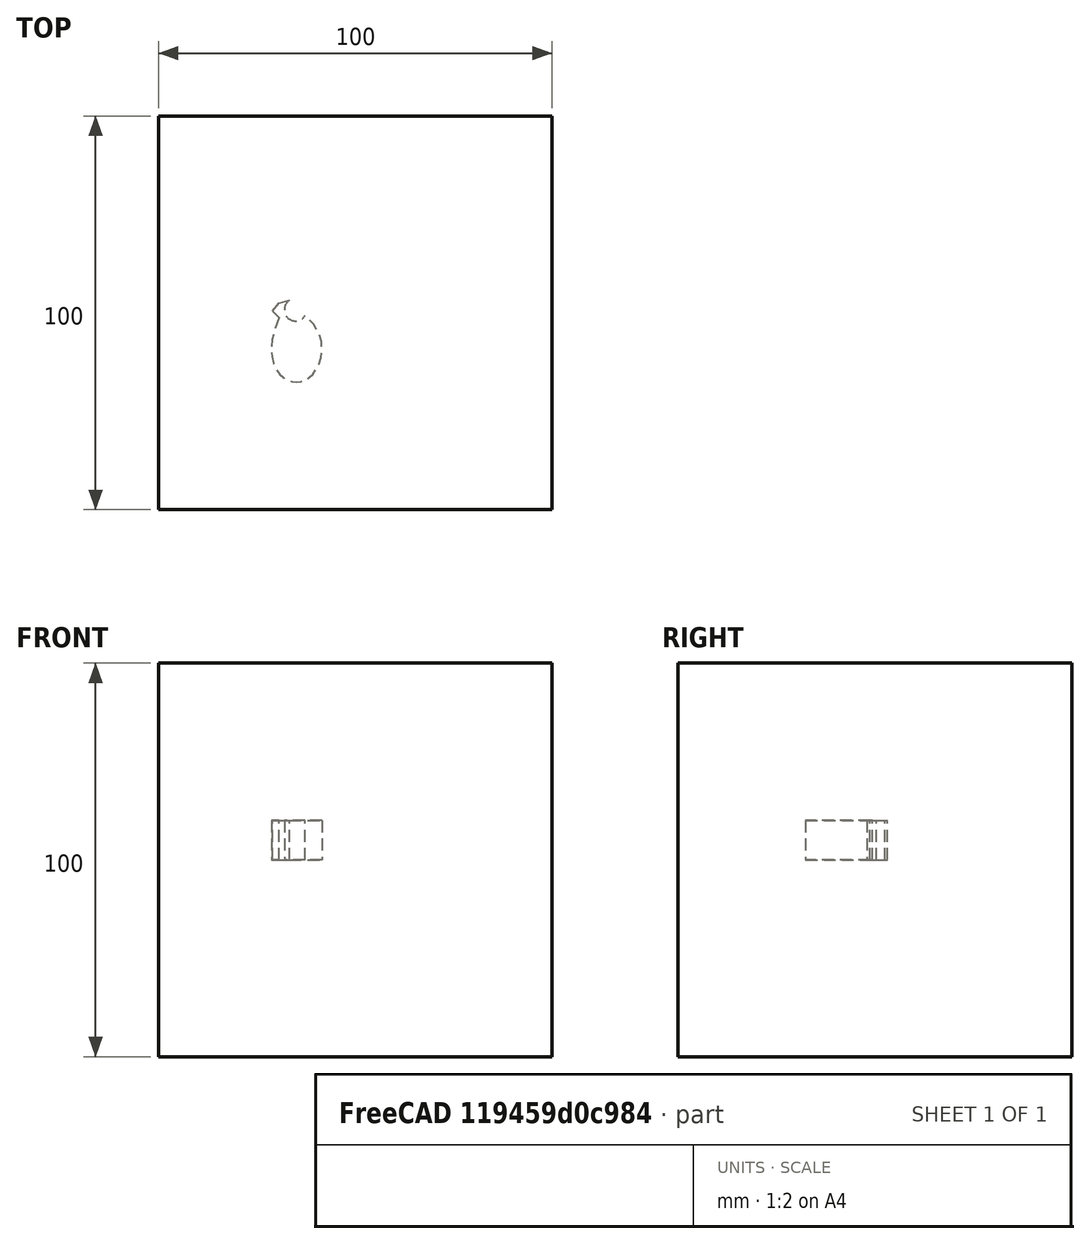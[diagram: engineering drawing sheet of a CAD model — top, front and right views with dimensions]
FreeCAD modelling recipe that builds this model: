
FCSTD DOCUMENT  (FreeCAD 1.0R39109 (Git))
Label: mirrorTest-1c
License: All rights reserved
LicenseURL: http://en.wikipedia.org/wiki/All_rights_reserved
objects: App::DocumentObjectGroupPython×1248, App::Part×2, Part::FeaturePython×1, Sketcher::SketchObject×1, Part::Extrusion×1, Part::Mirroring×1
note: 5 computed .brp shape members not serialized (recipe doc carries the construction recipe); baked Part::Feature solids carry a one-line shape summary decoded from their .brp

FEATURE [App::DocumentObjectGroupPython] HALFPI  # scripted group (container) (typed FeaturePython)
  name = HALFPI
  value = pi/2.
FEATURE [App::DocumentObjectGroupPython] PI  # scripted group (container) (typed FeaturePython)
  name = PI
  value = 1.*pi
FEATURE [App::DocumentObjectGroupPython] TWOPI  # scripted group (container) (typed FeaturePython)
  name = TWOPI
  value = 2.*pi
FEATURE [App::DocumentObjectGroupPython] Constants  # scripted group (container) (typed FeaturePython)
  Group = -> [HALFPI,PI,TWOPI]
FEATURE [App::DocumentObjectGroupPython] Variables  # scripted group (container) (typed FeaturePython)
FEATURE [App::DocumentObjectGroupPython] Quantities  # scripted group (container) (typed FeaturePython)
FEATURE [App::DocumentObjectGroupPython] Isotopes  # scripted group (container) (typed FeaturePython)
FEATURE [App::DocumentObjectGroupPython] Elements  # scripted group (container) (typed FeaturePython)
FEATURE [App::DocumentObjectGroupPython] G4Isotopes  # scripted group (container) (typed FeaturePython)
FEATURE [App::DocumentObjectGroupPython] H_element  # scripted group (container) (typed FeaturePython)
  Z = 1
  atom_value = 1.008
  formula = H
  name = H_element
FEATURE [App::DocumentObjectGroupPython] He_element  # scripted group (container) (typed FeaturePython)
  Z = 2
  atom_value = 4.0026
  formula = He
  name = He_element
FEATURE [App::DocumentObjectGroupPython] Li_element  # scripted group (container) (typed FeaturePython)
  Z = 3
  atom_value = 6.94
  formula = Li
  name = Li_element
FEATURE [App::DocumentObjectGroupPython] Be_element  # scripted group (container) (typed FeaturePython)
  Z = 4
  atom_value = 9.01218
  formula = Be
  name = Be_element
FEATURE [App::DocumentObjectGroupPython] B_element  # scripted group (container) (typed FeaturePython)
  Z = 5
  atom_value = 10.81
  formula = B
  name = B_element
FEATURE [App::DocumentObjectGroupPython] C_element  # scripted group (container) (typed FeaturePython)
  Z = 6
  atom_value = 12.011
  formula = C
  name = C_element
FEATURE [App::DocumentObjectGroupPython] N_element  # scripted group (container) (typed FeaturePython)
  Z = 7
  atom_value = 14.007
  formula = N
  name = N_element
FEATURE [App::DocumentObjectGroupPython] O_element  # scripted group (container) (typed FeaturePython)
  Z = 8
  atom_value = 15.999
  formula = O
  name = O_element
FEATURE [App::DocumentObjectGroupPython] F_element  # scripted group (container) (typed FeaturePython)
  Z = 9
  atom_value = 18.9984
  formula = F
  name = F_element
FEATURE [App::DocumentObjectGroupPython] Ne_element  # scripted group (container) (typed FeaturePython)
  Z = 10
  atom_value = 20.1797
  formula = Ne
  name = Ne_element
FEATURE [App::DocumentObjectGroupPython] Na_element  # scripted group (container) (typed FeaturePython)
  Z = 11
  atom_value = 22.9898
  formula = Na
  name = Na_element
FEATURE [App::DocumentObjectGroupPython] Mg_element  # scripted group (container) (typed FeaturePython)
  Z = 12
  atom_value = 24.305
  formula = Mg
  name = Mg_element
FEATURE [App::DocumentObjectGroupPython] Al_element  # scripted group (container) (typed FeaturePython)
  Z = 13
  atom_value = 26.9815
  formula = Al
  name = Al_element
FEATURE [App::DocumentObjectGroupPython] Si_element  # scripted group (container) (typed FeaturePython)
  Z = 14
  atom_value = 28.085
  formula = Si
  name = Si_element
FEATURE [App::DocumentObjectGroupPython] P_element  # scripted group (container) (typed FeaturePython)
  Z = 15
  atom_value = 30.9738
  formula = P
  name = P_element
FEATURE [App::DocumentObjectGroupPython] S_element  # scripted group (container) (typed FeaturePython)
  Z = 16
  atom_value = 32.06
  formula = S
  name = S_element
FEATURE [App::DocumentObjectGroupPython] Cl_element  # scripted group (container) (typed FeaturePython)
  Z = 17
  atom_value = 35.45
  formula = Cl
  name = Cl_element
FEATURE [App::DocumentObjectGroupPython] Ar_element  # scripted group (container) (typed FeaturePython)
  Z = 18
  atom_value = 39.95
  formula = Ar
  name = Ar_element
FEATURE [App::DocumentObjectGroupPython] K_element  # scripted group (container) (typed FeaturePython)
  Z = 19
  atom_value = 39.0983
  formula = K
  name = K_element
FEATURE [App::DocumentObjectGroupPython] Ca_element  # scripted group (container) (typed FeaturePython)
  Z = 20
  atom_value = 40.078
  formula = Ca
  name = Ca_element
FEATURE [App::DocumentObjectGroupPython] Sc_element  # scripted group (container) (typed FeaturePython)
  Z = 21
  atom_value = 44.9559
  formula = Sc
  name = Sc_element
FEATURE [App::DocumentObjectGroupPython] Ti_element  # scripted group (container) (typed FeaturePython)
  Z = 22
  atom_value = 47.867
  formula = Ti
  name = Ti_element
FEATURE [App::DocumentObjectGroupPython] V_element  # scripted group (container) (typed FeaturePython)
  Z = 23
  atom_value = 50.9415
  formula = V
  name = V_element
FEATURE [App::DocumentObjectGroupPython] Cr_element  # scripted group (container) (typed FeaturePython)
  Z = 24
  atom_value = 51.9961
  formula = Cr
  name = Cr_element
FEATURE [App::DocumentObjectGroupPython] Mn_element  # scripted group (container) (typed FeaturePython)
  Z = 25
  atom_value = 54.938
  formula = Mn
  name = Mn_element
FEATURE [App::DocumentObjectGroupPython] Fe_element  # scripted group (container) (typed FeaturePython)
  Z = 26
  atom_value = 55.845
  formula = Fe
  name = Fe_element
FEATURE [App::DocumentObjectGroupPython] Co_element  # scripted group (container) (typed FeaturePython)
  Z = 27
  atom_value = 58.9332
  formula = Co
  name = Co_element
FEATURE [App::DocumentObjectGroupPython] Ni_element  # scripted group (container) (typed FeaturePython)
  Z = 28
  atom_value = 58.6934
  formula = Ni
  name = Ni_element
FEATURE [App::DocumentObjectGroupPython] Cu_element  # scripted group (container) (typed FeaturePython)
  Z = 29
  atom_value = 63.546
  formula = Cu
  name = Cu_element
FEATURE [App::DocumentObjectGroupPython] Zn_element  # scripted group (container) (typed FeaturePython)
  Z = 30
  atom_value = 65.38
  formula = Zn
  name = Zn_element
FEATURE [App::DocumentObjectGroupPython] Ga_element  # scripted group (container) (typed FeaturePython)
  Z = 31
  atom_value = 69.723
  formula = Ga
  name = Ga_element
FEATURE [App::DocumentObjectGroupPython] Ge_element  # scripted group (container) (typed FeaturePython)
  Z = 32
  atom_value = 72.63
  formula = Ge
  name = Ge_element
FEATURE [App::DocumentObjectGroupPython] As_element  # scripted group (container) (typed FeaturePython)
  Z = 33
  atom_value = 74.9216
  formula = As
  name = As_element
FEATURE [App::DocumentObjectGroupPython] Se_element  # scripted group (container) (typed FeaturePython)
  Z = 34
  atom_value = 78.971
  formula = Se
  name = Se_element
FEATURE [App::DocumentObjectGroupPython] Br_element  # scripted group (container) (typed FeaturePython)
  Z = 35
  atom_value = 79.904
  formula = Br
  name = Br_element
FEATURE [App::DocumentObjectGroupPython] Kr_element  # scripted group (container) (typed FeaturePython)
  Z = 36
  atom_value = 83.798
  formula = Kr
  name = Kr_element
FEATURE [App::DocumentObjectGroupPython] Rb_element  # scripted group (container) (typed FeaturePython)
  Z = 37
  atom_value = 85.4678
  formula = Rb
  name = Rb_element
FEATURE [App::DocumentObjectGroupPython] Sr_element  # scripted group (container) (typed FeaturePython)
  Z = 38
  atom_value = 87.62
  formula = Sr
  name = Sr_element
FEATURE [App::DocumentObjectGroupPython] Y_element  # scripted group (container) (typed FeaturePython)
  Z = 39
  atom_value = 88.9058
  formula = Y
  name = Y_element
FEATURE [App::DocumentObjectGroupPython] Zr_element  # scripted group (container) (typed FeaturePython)
  Z = 40
  atom_value = 91.224
  formula = Zr
  name = Zr_element
FEATURE [App::DocumentObjectGroupPython] Nb_element  # scripted group (container) (typed FeaturePython)
  Z = 41
  atom_value = 92.9064
  formula = Nb
  name = Nb_element
FEATURE [App::DocumentObjectGroupPython] Mo_element  # scripted group (container) (typed FeaturePython)
  Z = 42
  atom_value = 95.95
  formula = Mo
  name = Mo_element
FEATURE [App::DocumentObjectGroupPython] Tc_element  # scripted group (container) (typed FeaturePython)
  Z = 43
  atom_value = 97
  formula = Tc
  name = Tc_element
FEATURE [App::DocumentObjectGroupPython] Ru_element  # scripted group (container) (typed FeaturePython)
  Z = 44
  atom_value = 101.07
  formula = Ru
  name = Ru_element
FEATURE [App::DocumentObjectGroupPython] Rh_element  # scripted group (container) (typed FeaturePython)
  Z = 45
  atom_value = 102.905
  formula = Rh
  name = Rh_element
FEATURE [App::DocumentObjectGroupPython] Pd_element  # scripted group (container) (typed FeaturePython)
  Z = 46
  atom_value = 106.42
  formula = Pd
  name = Pd_element
FEATURE [App::DocumentObjectGroupPython] Ag_element  # scripted group (container) (typed FeaturePython)
  Z = 47
  atom_value = 107.868
  formula = Ag
  name = Ag_element
FEATURE [App::DocumentObjectGroupPython] Cd_element  # scripted group (container) (typed FeaturePython)
  Z = 48
  atom_value = 112.414
  formula = Cd
  name = Cd_element
FEATURE [App::DocumentObjectGroupPython] In_element  # scripted group (container) (typed FeaturePython)
  Z = 49
  atom_value = 114.818
  formula = In
  name = In_element
FEATURE [App::DocumentObjectGroupPython] Sn_element  # scripted group (container) (typed FeaturePython)
  Z = 50
  atom_value = 118.71
  formula = Sn
  name = Sn_element
FEATURE [App::DocumentObjectGroupPython] Sb_element  # scripted group (container) (typed FeaturePython)
  Z = 51
  atom_value = 121.76
  formula = Sb
  name = Sb_element
FEATURE [App::DocumentObjectGroupPython] Te_element  # scripted group (container) (typed FeaturePython)
  Z = 52
  atom_value = 127.6
  formula = Te
  name = Te_element
FEATURE [App::DocumentObjectGroupPython] I_element  # scripted group (container) (typed FeaturePython)
  Z = 53
  atom_value = 126.904
  formula = I
  name = I_element
FEATURE [App::DocumentObjectGroupPython] Xe_element  # scripted group (container) (typed FeaturePython)
  Z = 54
  atom_value = 131.293
  formula = Xe
  name = Xe_element
FEATURE [App::DocumentObjectGroupPython] Cs_element  # scripted group (container) (typed FeaturePython)
  Z = 55
  atom_value = 132.905
  formula = Cs
  name = Cs_element
FEATURE [App::DocumentObjectGroupPython] Ba_element  # scripted group (container) (typed FeaturePython)
  Z = 56
  atom_value = 137.327
  formula = Ba
  name = Ba_element
FEATURE [App::DocumentObjectGroupPython] La_element  # scripted group (container) (typed FeaturePython)
  Z = 57
  atom_value = 138.905
  formula = La
  name = La_element
FEATURE [App::DocumentObjectGroupPython] Ce_element  # scripted group (container) (typed FeaturePython)
  Z = 58
  atom_value = 140.116
  formula = Ce
  name = Ce_element
FEATURE [App::DocumentObjectGroupPython] Pr_element  # scripted group (container) (typed FeaturePython)
  Z = 59
  atom_value = 140.908
  formula = Pr
  name = Pr_element
FEATURE [App::DocumentObjectGroupPython] Nd_element  # scripted group (container) (typed FeaturePython)
  Z = 60
  atom_value = 144.242
  formula = Nd
  name = Nd_element
FEATURE [App::DocumentObjectGroupPython] Pm_element  # scripted group (container) (typed FeaturePython)
  Z = 61
  atom_value = 145
  formula = Pm
  name = Pm_element
FEATURE [App::DocumentObjectGroupPython] Sm_element  # scripted group (container) (typed FeaturePython)
  Z = 62
  atom_value = 150.36
  formula = Sm
  name = Sm_element
FEATURE [App::DocumentObjectGroupPython] Eu_element  # scripted group (container) (typed FeaturePython)
  Z = 63
  atom_value = 151.964
  formula = Eu
  name = Eu_element
FEATURE [App::DocumentObjectGroupPython] Gd_element  # scripted group (container) (typed FeaturePython)
  Z = 64
  atom_value = 157.25
  formula = Gd
  name = Gd_element
FEATURE [App::DocumentObjectGroupPython] Tb_element  # scripted group (container) (typed FeaturePython)
  Z = 65
  atom_value = 158.925
  formula = Tb
  name = Tb_element
FEATURE [App::DocumentObjectGroupPython] Dy_element  # scripted group (container) (typed FeaturePython)
  Z = 66
  atom_value = 162.5
  formula = Dy
  name = Dy_element
FEATURE [App::DocumentObjectGroupPython] Ho_element  # scripted group (container) (typed FeaturePython)
  Z = 67
  atom_value = 164.93
  formula = Ho
  name = Ho_element
FEATURE [App::DocumentObjectGroupPython] Er_element  # scripted group (container) (typed FeaturePython)
  Z = 68
  atom_value = 167.259
  formula = Er
  name = Er_element
FEATURE [App::DocumentObjectGroupPython] Tm_element  # scripted group (container) (typed FeaturePython)
  Z = 69
  atom_value = 168.934
  formula = Tm
  name = Tm_element
FEATURE [App::DocumentObjectGroupPython] Yb_element  # scripted group (container) (typed FeaturePython)
  Z = 70
  atom_value = 173.045
  formula = Yb
  name = Yb_element
FEATURE [App::DocumentObjectGroupPython] Lu_element  # scripted group (container) (typed FeaturePython)
  Z = 71
  atom_value = 174.967
  formula = Lu
  name = Lu_element
FEATURE [App::DocumentObjectGroupPython] Hf_element  # scripted group (container) (typed FeaturePython)
  Z = 72
  atom_value = 178.49
  formula = Hf
  name = Hf_element
FEATURE [App::DocumentObjectGroupPython] Ta_element  # scripted group (container) (typed FeaturePython)
  Z = 73
  atom_value = 180.948
  formula = Ta
  name = Ta_element
FEATURE [App::DocumentObjectGroupPython] W_element  # scripted group (container) (typed FeaturePython)
  Z = 74
  atom_value = 183.84
  formula = W
  name = W_element
FEATURE [App::DocumentObjectGroupPython] Re_element  # scripted group (container) (typed FeaturePython)
  Z = 75
  atom_value = 186.207
  formula = Re
  name = Re_element
FEATURE [App::DocumentObjectGroupPython] Os_element  # scripted group (container) (typed FeaturePython)
  Z = 76
  atom_value = 190.23
  formula = Os
  name = Os_element
FEATURE [App::DocumentObjectGroupPython] Ir_element  # scripted group (container) (typed FeaturePython)
  Z = 77
  atom_value = 192.217
  formula = Ir
  name = Ir_element
FEATURE [App::DocumentObjectGroupPython] Pt_element  # scripted group (container) (typed FeaturePython)
  Z = 78
  atom_value = 195.084
  formula = Pt
  name = Pt_element
FEATURE [App::DocumentObjectGroupPython] Au_element  # scripted group (container) (typed FeaturePython)
  Z = 79
  atom_value = 196.967
  formula = Au
  name = Au_element
FEATURE [App::DocumentObjectGroupPython] Hg_element  # scripted group (container) (typed FeaturePython)
  Z = 80
  atom_value = 200.592
  formula = Hg
  name = Hg_element
FEATURE [App::DocumentObjectGroupPython] Tl_element  # scripted group (container) (typed FeaturePython)
  Z = 81
  atom_value = 204.38
  formula = Tl
  name = Tl_element
FEATURE [App::DocumentObjectGroupPython] Pb_element  # scripted group (container) (typed FeaturePython)
  Z = 82
  atom_value = 207.2
  formula = Pb
  name = Pb_element
FEATURE [App::DocumentObjectGroupPython] Bi_element  # scripted group (container) (typed FeaturePython)
  Z = 83
  atom_value = 208.98
  formula = Bi
  name = Bi_element
FEATURE [App::DocumentObjectGroupPython] Po_element  # scripted group (container) (typed FeaturePython)
  Z = 84
  atom_value = 209
  formula = Po
  name = Po_element
FEATURE [App::DocumentObjectGroupPython] At_element  # scripted group (container) (typed FeaturePython)
  Z = 85
  atom_value = 210
  formula = At
  name = At_element
FEATURE [App::DocumentObjectGroupPython] Rn_element  # scripted group (container) (typed FeaturePython)
  Z = 86
  atom_value = 222
  formula = Rn
  name = Rn_element
FEATURE [App::DocumentObjectGroupPython] Fr_element  # scripted group (container) (typed FeaturePython)
  Z = 87
  atom_value = 223
  formula = Fr
  name = Fr_element
FEATURE [App::DocumentObjectGroupPython] Ra_element  # scripted group (container) (typed FeaturePython)
  Z = 88
  atom_value = 226
  formula = Ra
  name = Ra_element
FEATURE [App::DocumentObjectGroupPython] Ac_element  # scripted group (container) (typed FeaturePython)
  Z = 89
  atom_value = 227
  formula = Ac
  name = Ac_element
FEATURE [App::DocumentObjectGroupPython] Th_element  # scripted group (container) (typed FeaturePython)
  Z = 90
  atom_value = 232.038
  formula = Th
  name = Th_element
FEATURE [App::DocumentObjectGroupPython] Pa_element  # scripted group (container) (typed FeaturePython)
  Z = 91
  atom_value = 231.036
  formula = Pa
  name = Pa_element
FEATURE [App::DocumentObjectGroupPython] U_element  # scripted group (container) (typed FeaturePython)
  Z = 92
  atom_value = 238.029
  formula = U
  name = U_element
FEATURE [App::DocumentObjectGroupPython] Np_element  # scripted group (container) (typed FeaturePython)
  Z = 93
  atom_value = 237
  formula = Np
  name = Np_element
FEATURE [App::DocumentObjectGroupPython] Pu_element  # scripted group (container) (typed FeaturePython)
  Z = 94
  atom_value = 244
  formula = Pu
  name = Pu_element
FEATURE [App::DocumentObjectGroupPython] Am_element  # scripted group (container) (typed FeaturePython)
  Z = 95
  atom_value = 243
  formula = Am
  name = Am_element
FEATURE [App::DocumentObjectGroupPython] Cm_element  # scripted group (container) (typed FeaturePython)
  Z = 96
  atom_value = 247
  formula = Cm
  name = Cm_element
FEATURE [App::DocumentObjectGroupPython] Bk_element  # scripted group (container) (typed FeaturePython)
  Z = 97
  atom_value = 247
  formula = Bk
  name = Bk_element
FEATURE [App::DocumentObjectGroupPython] Cf_element  # scripted group (container) (typed FeaturePython)
  Z = 98
  atom_value = 251
  formula = Cf
  name = Cf_element
FEATURE [App::DocumentObjectGroupPython] G4Elements  # scripted group (container) (typed FeaturePython)
  Group = -> [H_element,He_element,Li_element,Be_element,B_element,C_element,N_element,O_element,F_element,Ne_element,Na_element,Mg_element,Al_element,Si_element,P_element,S_element,Cl_element,Ar_element,K_element,Ca_element,Sc_element,Ti_element,V_element,Cr_element,Mn_element,Fe_element,Co_element,Ni_element,Cu_element,Zn_element,Ga_element,Ge_element,As_element,Se_element,Br_element,Kr_element,Rb_element,+61 more]
FEATURE [App::DocumentObjectGroupPython] H_element001  label="H_element : 0.101"  # scripted group (container) (typed FeaturePython)
  n = 0.101327
FEATURE [App::DocumentObjectGroupPython] C_element001  label="C_element : 0.775"  # scripted group (container) (typed FeaturePython)
  n = 0.7755
FEATURE [App::DocumentObjectGroupPython] N_element001  label="N_element : 0.035"  # scripted group (container) (typed FeaturePython)
  n = 0.035057
FEATURE [App::DocumentObjectGroupPython] O_element001  label="O_element : 0.052"  # scripted group (container) (typed FeaturePython)
  n = 0.0523159
FEATURE [App::DocumentObjectGroupPython] F_element001  label="F_element : 0.017"  # scripted group (container) (typed FeaturePython)
  n = 0.017422
FEATURE [App::DocumentObjectGroupPython] Ca_element001  label="Ca_element : 0.018"  # scripted group (container) (typed FeaturePython)
  n = 0.018378
FEATURE [App::DocumentObjectGroupPython] G4_A_150_TISSUE  label="G4_A-150_TISSUE"  # scripted group (container) (typed FeaturePython)
  Dunit = g/cm3
  Dvalue = 1.127
  Group = -> [H_element001,C_element001,N_element001,O_element001,F_element001,Ca_element001]
  conduct = 2
  density = 1
  expand = 3
  formula = G4_A-150_TISSUE
  name = G4_A-150_TISSUE
  specific = 4
FEATURE [App::DocumentObjectGroupPython] C_element002  label="C_element : 3"  # scripted group (container) (typed FeaturePython)
  n = 3
  ref = C_element
FEATURE [App::DocumentObjectGroupPython] H_element002  label="H_element : 6"  # scripted group (container) (typed FeaturePython)
  n = 6
  ref = H_element
FEATURE [App::DocumentObjectGroupPython] O_element002  label="O_element : 1"  # scripted group (container) (typed FeaturePython)
  n = 1
  ref = O_element
FEATURE [App::DocumentObjectGroupPython] G4_ACETONE  # scripted group (container) (typed FeaturePython)
  Dunit = g/cm3
  Dvalue = 0.7899
  Group = -> [C_element002,H_element002,O_element002]
  conduct = 2
  density = 1
  expand = 3
  formula = G4_ACETONE
  name = G4_ACETONE
  specific = 4
FEATURE [App::DocumentObjectGroupPython] C_element003  label="C_element : 2"  # scripted group (container) (typed FeaturePython)
  n = 2
  ref = C_element
FEATURE [App::DocumentObjectGroupPython] H_element003  label="H_element : 2"  # scripted group (container) (typed FeaturePython)
  n = 2
  ref = H_element
FEATURE [App::DocumentObjectGroupPython] G4_ACETYLENE  # scripted group (container) (typed FeaturePython)
  Dunit = g/cm3
  Dvalue = 0.0010967
  Group = -> [C_element003,H_element003]
  conduct = 2
  density = 1
  expand = 3
  formula = G4_ACETYLENE
  name = G4_ACETYLENE
  specific = 4
FEATURE [App::DocumentObjectGroupPython] C_element004  label="C_element : 5"  # scripted group (container) (typed FeaturePython)
  n = 5
  ref = C_element
FEATURE [App::DocumentObjectGroupPython] H_element004  label="H_element : 5"  # scripted group (container) (typed FeaturePython)
  n = 5
  ref = H_element
FEATURE [App::DocumentObjectGroupPython] N_element002  label="N_element : 5"  # scripted group (container) (typed FeaturePython)
  n = 5
  ref = N_element
FEATURE [App::DocumentObjectGroupPython] G4_ADENINE  # scripted group (container) (typed FeaturePython)
  Dunit = g/cm3
  Dvalue = 1.6
  Group = -> [C_element004,H_element004,N_element002]
  conduct = 2
  density = 1
  expand = 3
  formula = G4_ADENINE
  name = G4_ADENINE
  specific = 4
FEATURE [App::DocumentObjectGroupPython] H_element005  label="H_element : 0.114"  # scripted group (container) (typed FeaturePython)
  n = 0.114
FEATURE [App::DocumentObjectGroupPython] C_element005  label="C_element : 0.598"  # scripted group (container) (typed FeaturePython)
  n = 0.598
FEATURE [App::DocumentObjectGroupPython] N_element003  label="N_element : 0.007"  # scripted group (container) (typed FeaturePython)
  n = 0.007
FEATURE [App::DocumentObjectGroupPython] O_element003  label="O_element : 0.278"  # scripted group (container) (typed FeaturePython)
  n = 0.278
FEATURE [App::DocumentObjectGroupPython] Na_element001  label="Na_element : 0.001"  # scripted group (container) (typed FeaturePython)
  n = 0.001
FEATURE [App::DocumentObjectGroupPython] S_element001  label="S_element : 0.001"  # scripted group (container) (typed FeaturePython)
  n = 0.001
FEATURE [App::DocumentObjectGroupPython] Cl_element001  label="Cl_element : 0.001"  # scripted group (container) (typed FeaturePython)
  n = 0.001
FEATURE [App::DocumentObjectGroupPython] G4_ADIPOSE_TISSUE_ICRP  # scripted group (container) (typed FeaturePython)
  Dunit = g/cm3
  Dvalue = 0.95
  Group = -> [H_element005,C_element005,N_element003,O_element003,Na_element001,S_element001,Cl_element001]
  conduct = 2
  density = 1
  expand = 3
  formula = G4_ADIPOSE_TISSUE_ICRP
  name = G4_ADIPOSE_TISSUE_ICRP
  specific = 4
FEATURE [App::DocumentObjectGroupPython] C_element006  label="C_element : 0.000"  # scripted group (container) (typed FeaturePython)
  n = 0.000124
FEATURE [App::DocumentObjectGroupPython] N_element004  label="N_element : 0.755"  # scripted group (container) (typed FeaturePython)
  n = 0.755268
FEATURE [App::DocumentObjectGroupPython] O_element004  label="O_element : 0.232"  # scripted group (container) (typed FeaturePython)
  n = 0.231781
FEATURE [App::DocumentObjectGroupPython] Ar_element001  label="Ar_element : 0.013"  # scripted group (container) (typed FeaturePython)
  n = 0.012827
FEATURE [App::DocumentObjectGroupPython] G4_AIR  # scripted group (container) (typed FeaturePython)
  Dunit = g/cm3
  Dvalue = 0.00120479
  Group = -> [C_element006,N_element004,O_element004,Ar_element001]
  conduct = 2
  density = 1
  expand = 3
  formula = G4_AIR
  name = G4_AIR
  specific = 4
FEATURE [App::DocumentObjectGroupPython] C_element007  label="C_element : 006"  # scripted group (container) (typed FeaturePython)
  n = 3
  ref = C_element
FEATURE [App::DocumentObjectGroupPython] H_element006  label="H_element : 7"  # scripted group (container) (typed FeaturePython)
  n = 7
  ref = H_element
FEATURE [App::DocumentObjectGroupPython] N_element005  label="N_element : 1"  # scripted group (container) (typed FeaturePython)
  n = 1
  ref = N_element
FEATURE [App::DocumentObjectGroupPython] O_element005  label="O_element : 2"  # scripted group (container) (typed FeaturePython)
  n = 2
  ref = O_element
FEATURE [App::DocumentObjectGroupPython] G4_ALANINE  # scripted group (container) (typed FeaturePython)
  Dunit = g/cm3
  Dvalue = 1.42
  Group = -> [C_element007,H_element006,N_element005,O_element005]
  conduct = 2
  density = 1
  expand = 3
  formula = G4_ALANINE
  name = G4_ALANINE
  specific = 4
FEATURE [App::DocumentObjectGroupPython] Al_element001  label="Al_element : 2"  # scripted group (container) (typed FeaturePython)
  n = 2
  ref = Al_element
FEATURE [App::DocumentObjectGroupPython] O_element006  label="O_element : 3"  # scripted group (container) (typed FeaturePython)
  n = 3
  ref = O_element
FEATURE [App::DocumentObjectGroupPython] G4_ALUMINUM_OXIDE  # scripted group (container) (typed FeaturePython)
  Dunit = g/cm3
  Dvalue = 3.97
  Group = -> [Al_element001,O_element006]
  conduct = 2
  density = 1
  expand = 3
  formula = G4_ALUMINUM_OXIDE
  name = G4_ALUMINUM_OXIDE
  specific = 4
FEATURE [App::DocumentObjectGroupPython] H_element007  label="H_element : 0.106"  # scripted group (container) (typed FeaturePython)
  n = 0.10593
FEATURE [App::DocumentObjectGroupPython] C_element008  label="C_element : 0.789"  # scripted group (container) (typed FeaturePython)
  n = 0.788974
FEATURE [App::DocumentObjectGroupPython] O_element007  label="O_element : 0.105"  # scripted group (container) (typed FeaturePython)
  n = 0.105096
FEATURE [App::DocumentObjectGroupPython] G4_AMBER  # scripted group (container) (typed FeaturePython)
  Dunit = g/cm3
  Dvalue = 1.1
  Group = -> [H_element007,C_element008,O_element007]
  conduct = 2
  density = 1
  expand = 3
  formula = G4_AMBER
  name = G4_AMBER
  specific = 4
FEATURE [App::DocumentObjectGroupPython] N_element006  label="N_element : 006"  # scripted group (container) (typed FeaturePython)
  n = 1
  ref = N_element
FEATURE [App::DocumentObjectGroupPython] H_element008  label="H_element : 3"  # scripted group (container) (typed FeaturePython)
  n = 3
  ref = H_element
FEATURE [App::DocumentObjectGroupPython] G4_AMMONIA  # scripted group (container) (typed FeaturePython)
  Dunit = g/cm3
  Dvalue = 0.000826019
  Group = -> [N_element006,H_element008]
  conduct = 2
  density = 1
  expand = 3
  formula = G4_AMMONIA
  name = G4_AMMONIA
  specific = 4
FEATURE [App::DocumentObjectGroupPython] C_element009  label="C_element : 6"  # scripted group (container) (typed FeaturePython)
  n = 6
  ref = C_element
FEATURE [App::DocumentObjectGroupPython] H_element009  label="H_element : 008"  # scripted group (container) (typed FeaturePython)
  n = 7
  ref = H_element
FEATURE [App::DocumentObjectGroupPython] N_element007  label="N_element : 007"  # scripted group (container) (typed FeaturePython)
  n = 1
  ref = N_element
FEATURE [App::DocumentObjectGroupPython] G4_ANILINE  # scripted group (container) (typed FeaturePython)
  Dunit = g/cm3
  Dvalue = 1.0235
  Group = -> [C_element009,H_element009,N_element007]
  conduct = 2
  density = 1
  expand = 3
  formula = G4_ANILINE
  name = G4_ANILINE
  specific = 4
FEATURE [App::DocumentObjectGroupPython] C_element010  label="C_element : 14"  # scripted group (container) (typed FeaturePython)
  n = 14
  ref = C_element
FEATURE [App::DocumentObjectGroupPython] H_element010  label="H_element : 10"  # scripted group (container) (typed FeaturePython)
  n = 10
  ref = H_element
FEATURE [App::DocumentObjectGroupPython] G4_ANTHRACENE  # scripted group (container) (typed FeaturePython)
  Dunit = g/cm3
  Dvalue = 1.283
  Group = -> [C_element010,H_element010]
  conduct = 2
  density = 1
  expand = 3
  formula = G4_ANTHRACENE
  name = G4_ANTHRACENE
  specific = 4
FEATURE [App::DocumentObjectGroupPython] H_element011  label="H_element : 0.065"  # scripted group (container) (typed FeaturePython)
  n = 0.0654709
FEATURE [App::DocumentObjectGroupPython] C_element011  label="C_element : 0.537"  # scripted group (container) (typed FeaturePython)
  n = 0.536944
FEATURE [App::DocumentObjectGroupPython] N_element008  label="N_element : 0.021"  # scripted group (container) (typed FeaturePython)
  n = 0.0215
FEATURE [App::DocumentObjectGroupPython] O_element008  label="O_element : 0.032"  # scripted group (container) (typed FeaturePython)
  n = 0.032085
FEATURE [App::DocumentObjectGroupPython] F_element002  label="F_element : 0.167"  # scripted group (container) (typed FeaturePython)
  n = 0.167411
FEATURE [App::DocumentObjectGroupPython] Ca_element002  label="Ca_element : 0.177"  # scripted group (container) (typed FeaturePython)
  n = 0.176589
FEATURE [App::DocumentObjectGroupPython] G4_B_100_BONE  label="G4_B-100_BONE"  # scripted group (container) (typed FeaturePython)
  Dunit = g/cm3
  Dvalue = 1.45
  Group = -> [H_element011,C_element011,N_element008,O_element008,F_element002,Ca_element002]
  conduct = 2
  density = 1
  expand = 3
  formula = G4_B-100_BONE
  name = G4_B-100_BONE
  specific = 4
FEATURE [App::DocumentObjectGroupPython] H_element012  label="H_element : 0.057"  # scripted group (container) (typed FeaturePython)
  n = 0.057441
FEATURE [App::DocumentObjectGroupPython] C_element012  label="C_element : 0.790"  # scripted group (container) (typed FeaturePython)
  n = 0.774591
FEATURE [App::DocumentObjectGroupPython] O_element009  label="O_element : 0.168"  # scripted group (container) (typed FeaturePython)
  n = 0.167968
FEATURE [App::DocumentObjectGroupPython] G4_BAKELITE  # scripted group (container) (typed FeaturePython)
  Dunit = g/cm3
  Dvalue = 1.25
  Group = -> [H_element012,C_element012,O_element009]
  conduct = 2
  density = 1
  expand = 3
  formula = G4_BAKELITE
  name = G4_BAKELITE
  specific = 4
FEATURE [App::DocumentObjectGroupPython] Ba_element001  label="Ba_element : 1"  # scripted group (container) (typed FeaturePython)
  n = 1
  ref = Ba_element
FEATURE [App::DocumentObjectGroupPython] F_element003  label="F_element : 2"  # scripted group (container) (typed FeaturePython)
  n = 2
  ref = F_element
FEATURE [App::DocumentObjectGroupPython] G4_BARIUM_FLUORIDE  # scripted group (container) (typed FeaturePython)
  Dunit = g/cm3
  Dvalue = 4.89
  Group = -> [Ba_element001,F_element003]
  conduct = 2
  density = 1
  expand = 3
  formula = G4_BARIUM_FLUORIDE
  name = G4_BARIUM_FLUORIDE
  specific = 4
FEATURE [App::DocumentObjectGroupPython] Ba_element002  label="Ba_element : 002"  # scripted group (container) (typed FeaturePython)
  n = 1
  ref = Ba_element
FEATURE [App::DocumentObjectGroupPython] S_element002  label="S_element : 1"  # scripted group (container) (typed FeaturePython)
  n = 1
  ref = S_element
FEATURE [App::DocumentObjectGroupPython] O_element010  label="O_element : 4"  # scripted group (container) (typed FeaturePython)
  n = 4
  ref = O_element
FEATURE [App::DocumentObjectGroupPython] G4_BARIUM_SULFATE  # scripted group (container) (typed FeaturePython)
  Dunit = g/cm3
  Dvalue = 4.5
  Group = -> [Ba_element002,S_element002,O_element010]
  conduct = 2
  density = 1
  expand = 3
  formula = G4_BARIUM_SULFATE
  name = G4_BARIUM_SULFATE
  specific = 4
FEATURE [App::DocumentObjectGroupPython] C_element013  label="C_element : 007"  # scripted group (container) (typed FeaturePython)
  n = 6
  ref = C_element
FEATURE [App::DocumentObjectGroupPython] H_element013  label="H_element : 009"  # scripted group (container) (typed FeaturePython)
  n = 6
  ref = H_element
FEATURE [App::DocumentObjectGroupPython] G4_BENZENE  # scripted group (container) (typed FeaturePython)
  Dunit = g/cm3
  Dvalue = 0.87865
  Group = -> [C_element013,H_element013]
  conduct = 2
  density = 1
  expand = 3
  formula = G4_BENZENE
  name = G4_BENZENE
  specific = 4
FEATURE [App::DocumentObjectGroupPython] Be_element001  label="Be_element : 1"  # scripted group (container) (typed FeaturePython)
  n = 1
  ref = Be_element
FEATURE [App::DocumentObjectGroupPython] O_element011  label="O_element : 005"  # scripted group (container) (typed FeaturePython)
  n = 1
  ref = O_element
FEATURE [App::DocumentObjectGroupPython] G4_BERYLLIUM_OXIDE  # scripted group (container) (typed FeaturePython)
  Dunit = g/cm3
  Dvalue = 3.01
  Group = -> [Be_element001,O_element011]
  conduct = 2
  density = 1
  expand = 3
  formula = G4_BERYLLIUM_OXIDE
  name = G4_BERYLLIUM_OXIDE
  specific = 4
FEATURE [App::DocumentObjectGroupPython] Bi_element001  label="Bi_element : 4"  # scripted group (container) (typed FeaturePython)
  n = 4
  ref = Bi_element
FEATURE [App::DocumentObjectGroupPython] Ge_element001  label="Ge_element : 3"  # scripted group (container) (typed FeaturePython)
  n = 3
  ref = Ge_element
FEATURE [App::DocumentObjectGroupPython] O_element012  label="O_element : 12"  # scripted group (container) (typed FeaturePython)
  n = 12
  ref = O_element
FEATURE [App::DocumentObjectGroupPython] G4_BGO  # scripted group (container) (typed FeaturePython)
  Dunit = g/cm3
  Dvalue = 7.13
  Group = -> [Bi_element001,Ge_element001,O_element012]
  conduct = 2
  density = 1
  expand = 3
  formula = G4_BGO
  name = G4_BGO
  specific = 4
FEATURE [App::DocumentObjectGroupPython] H_element014  label="H_element : 0.102"  # scripted group (container) (typed FeaturePython)
  n = 0.102
FEATURE [App::DocumentObjectGroupPython] C_element014  label="C_element : 0.110"  # scripted group (container) (typed FeaturePython)
  n = 0.11
FEATURE [App::DocumentObjectGroupPython] N_element009  label="N_element : 0.033"  # scripted group (container) (typed FeaturePython)
  n = 0.033
FEATURE [App::DocumentObjectGroupPython] O_element013  label="O_element : 0.745"  # scripted group (container) (typed FeaturePython)
  n = 0.745
FEATURE [App::DocumentObjectGroupPython] Na_element002  label="Na_element : 0.002"  # scripted group (container) (typed FeaturePython)
  n = 0.001
FEATURE [App::DocumentObjectGroupPython] P_element001  label="P_element : 0.001"  # scripted group (container) (typed FeaturePython)
  n = 0.001
FEATURE [App::DocumentObjectGroupPython] S_element003  label="S_element : 0.002"  # scripted group (container) (typed FeaturePython)
  n = 0.002
FEATURE [App::DocumentObjectGroupPython] Cl_element002  label="Cl_element : 0.003"  # scripted group (container) (typed FeaturePython)
  n = 0.003
FEATURE [App::DocumentObjectGroupPython] K_element001  label="K_element : 0.002"  # scripted group (container) (typed FeaturePython)
  n = 0.002
FEATURE [App::DocumentObjectGroupPython] Fe_element001  label="Fe_element : 0.001"  # scripted group (container) (typed FeaturePython)
  n = 0.001
FEATURE [App::DocumentObjectGroupPython] G4_BLOOD_ICRP  # scripted group (container) (typed FeaturePython)
  Dunit = g/cm3
  Dvalue = 1.06
  Group = -> [H_element014,C_element014,N_element009,O_element013,Na_element002,P_element001,S_element003,Cl_element002,K_element001,Fe_element001]
  conduct = 2
  density = 1
  expand = 3
  formula = G4_BLOOD_ICRP
  name = G4_BLOOD_ICRP
  specific = 4
FEATURE [App::DocumentObjectGroupPython] H_element015  label="H_element : 0.064"  # scripted group (container) (typed FeaturePython)
  n = 0.064
FEATURE [App::DocumentObjectGroupPython] C_element015  label="C_element : 0.278"  # scripted group (container) (typed FeaturePython)
  n = 0.278
FEATURE [App::DocumentObjectGroupPython] N_element010  label="N_element : 0.027"  # scripted group (container) (typed FeaturePython)
  n = 0.027
FEATURE [App::DocumentObjectGroupPython] O_element014  label="O_element : 0.410"  # scripted group (container) (typed FeaturePython)
  n = 0.41
FEATURE [App::DocumentObjectGroupPython] Mg_element001  label="Mg_element : 0.002"  # scripted group (container) (typed FeaturePython)
  n = 0.002
FEATURE [App::DocumentObjectGroupPython] P_element002  label="P_element : 0.070"  # scripted group (container) (typed FeaturePython)
  n = 0.07
FEATURE [App::DocumentObjectGroupPython] S_element004  label="S_element : 0.003"  # scripted group (container) (typed FeaturePython)
  n = 0.002
FEATURE [App::DocumentObjectGroupPython] Ca_element003  label="Ca_element : 0.147"  # scripted group (container) (typed FeaturePython)
  n = 0.147
FEATURE [App::DocumentObjectGroupPython] G4_BONE_COMPACT_ICRU  # scripted group (container) (typed FeaturePython)
  Dunit = g/cm3
  Dvalue = 1.85
  Group = -> [H_element015,C_element015,N_element010,O_element014,Mg_element001,P_element002,S_element004,Ca_element003]
  conduct = 2
  density = 1
  expand = 3
  formula = G4_BONE_COMPACT_ICRU
  name = G4_BONE_COMPACT_ICRU
  specific = 4
FEATURE [App::DocumentObjectGroupPython] H_element016  label="H_element : 0.034"  # scripted group (container) (typed FeaturePython)
  n = 0.034
FEATURE [App::DocumentObjectGroupPython] C_element016  label="C_element : 0.155"  # scripted group (container) (typed FeaturePython)
  n = 0.155
FEATURE [App::DocumentObjectGroupPython] N_element011  label="N_element : 0.042"  # scripted group (container) (typed FeaturePython)
  n = 0.042
FEATURE [App::DocumentObjectGroupPython] O_element015  label="O_element : 0.435"  # scripted group (container) (typed FeaturePython)
  n = 0.435
FEATURE [App::DocumentObjectGroupPython] Na_element003  label="Na_element : 0.003"  # scripted group (container) (typed FeaturePython)
  n = 0.001
FEATURE [App::DocumentObjectGroupPython] Mg_element002  label="Mg_element : 0.003"  # scripted group (container) (typed FeaturePython)
  n = 0.002
FEATURE [App::DocumentObjectGroupPython] P_element003  label="P_element : 0.103"  # scripted group (container) (typed FeaturePython)
  n = 0.103
FEATURE [App::DocumentObjectGroupPython] S_element005  label="S_element : 0.004"  # scripted group (container) (typed FeaturePython)
  n = 0.003
FEATURE [App::DocumentObjectGroupPython] Ca_element004  label="Ca_element : 0.225"  # scripted group (container) (typed FeaturePython)
  n = 0.225
FEATURE [App::DocumentObjectGroupPython] G4_BONE_CORTICAL_ICRP  # scripted group (container) (typed FeaturePython)
  Dunit = g/cm3
  Dvalue = 1.92
  Group = -> [H_element016,C_element016,N_element011,O_element015,Na_element003,Mg_element002,P_element003,S_element005,Ca_element004]
  conduct = 2
  density = 1
  expand = 3
  formula = G4_BONE_CORTICAL_ICRP
  name = G4_BONE_CORTICAL_ICRP
  specific = 4
FEATURE [App::DocumentObjectGroupPython] B_element001  label="B_element : 4"  # scripted group (container) (typed FeaturePython)
  n = 4
  ref = B_element
FEATURE [App::DocumentObjectGroupPython] C_element017  label="C_element : 1"  # scripted group (container) (typed FeaturePython)
  n = 1
  ref = C_element
FEATURE [App::DocumentObjectGroupPython] G4_BORON_CARBIDE  # scripted group (container) (typed FeaturePython)
  Dunit = g/cm3
  Dvalue = 2.52
  Group = -> [B_element001,C_element017]
  conduct = 2
  density = 1
  expand = 3
  formula = G4_BORON_CARBIDE
  name = G4_BORON_CARBIDE
  specific = 4
FEATURE [App::DocumentObjectGroupPython] B_element002  label="B_element : 2"  # scripted group (container) (typed FeaturePython)
  n = 2
  ref = B_element
FEATURE [App::DocumentObjectGroupPython] O_element016  label="O_element : 006"  # scripted group (container) (typed FeaturePython)
  n = 3
  ref = O_element
FEATURE [App::DocumentObjectGroupPython] G4_BORON_OXIDE  # scripted group (container) (typed FeaturePython)
  Dunit = g/cm3
  Dvalue = 1.812
  Group = -> [B_element002,O_element016]
  conduct = 2
  density = 1
  expand = 3
  formula = G4_BORON_OXIDE
  name = G4_BORON_OXIDE
  specific = 4
FEATURE [App::DocumentObjectGroupPython] H_element017  label="H_element : 0.107"  # scripted group (container) (typed FeaturePython)
  n = 0.107
FEATURE [App::DocumentObjectGroupPython] C_element018  label="C_element : 0.145"  # scripted group (container) (typed FeaturePython)
  n = 0.145
FEATURE [App::DocumentObjectGroupPython] N_element012  label="N_element : 0.022"  # scripted group (container) (typed FeaturePython)
  n = 0.022
FEATURE [App::DocumentObjectGroupPython] O_element017  label="O_element : 0.712"  # scripted group (container) (typed FeaturePython)
  n = 0.712
FEATURE [App::DocumentObjectGroupPython] Na_element004  label="Na_element : 0.004"  # scripted group (container) (typed FeaturePython)
  n = 0.002
FEATURE [App::DocumentObjectGroupPython] P_element004  label="P_element : 0.004"  # scripted group (container) (typed FeaturePython)
  n = 0.004
FEATURE [App::DocumentObjectGroupPython] S_element006  label="S_element : 0.005"  # scripted group (container) (typed FeaturePython)
  n = 0.002
FEATURE [App::DocumentObjectGroupPython] Cl_element003  label="Cl_element : 0.004"  # scripted group (container) (typed FeaturePython)
  n = 0.003
FEATURE [App::DocumentObjectGroupPython] K_element002  label="K_element : 0.003"  # scripted group (container) (typed FeaturePython)
  n = 0.003
FEATURE [App::DocumentObjectGroupPython] G4_BRAIN_ICRP  # scripted group (container) (typed FeaturePython)
  Dunit = g/cm3
  Dvalue = 1.04
  Group = -> [H_element017,C_element018,N_element012,O_element017,Na_element004,P_element004,S_element006,Cl_element003,K_element002]
  conduct = 2
  density = 1
  expand = 3
  formula = G4_BRAIN_ICRP
  name = G4_BRAIN_ICRP
  specific = 4
FEATURE [App::DocumentObjectGroupPython] C_element019  label="C_element : 4"  # scripted group (container) (typed FeaturePython)
  n = 4
  ref = C_element
FEATURE [App::DocumentObjectGroupPython] H_element018  label="H_element : 010"  # scripted group (container) (typed FeaturePython)
  n = 10
  ref = H_element
FEATURE [App::DocumentObjectGroupPython] G4_BUTANE  # scripted group (container) (typed FeaturePython)
  Dunit = g/cm3
  Dvalue = 0.00249343
  Group = -> [C_element019,H_element018]
  conduct = 2
  density = 1
  expand = 3
  formula = G4_BUTANE
  name = G4_BUTANE
  specific = 4
FEATURE [App::DocumentObjectGroupPython] C_element020  label="C_element : 008"  # scripted group (container) (typed FeaturePython)
  n = 4
  ref = C_element
FEATURE [App::DocumentObjectGroupPython] H_element019  label="H_element : 011"  # scripted group (container) (typed FeaturePython)
  n = 10
  ref = H_element
FEATURE [App::DocumentObjectGroupPython] O_element018  label="O_element : 007"  # scripted group (container) (typed FeaturePython)
  n = 1
  ref = O_element
FEATURE [App::DocumentObjectGroupPython] G4_N_BUTYL_ALCOHOL  label="G4_N-BUTYL_ALCOHOL"  # scripted group (container) (typed FeaturePython)
  Dunit = g/cm3
  Dvalue = 0.8098
  Group = -> [C_element020,H_element019,O_element018]
  conduct = 2
  density = 1
  expand = 3
  formula = G4_N-BUTYL_ALCOHOL
  name = G4_N-BUTYL_ALCOHOL
  specific = 4
FEATURE [App::DocumentObjectGroupPython] H_element020  label="H_element : 0.025"  # scripted group (container) (typed FeaturePython)
  n = 0.02468
FEATURE [App::DocumentObjectGroupPython] C_element021  label="C_element : 0.502"  # scripted group (container) (typed FeaturePython)
  n = 0.501611
FEATURE [App::DocumentObjectGroupPython] O_element019  label="O_element : 0.005"  # scripted group (container) (typed FeaturePython)
  n = 0.004527
FEATURE [App::DocumentObjectGroupPython] F_element004  label="F_element : 0.465"  # scripted group (container) (typed FeaturePython)
  n = 0.465209
FEATURE [App::DocumentObjectGroupPython] Si_element001  label="Si_element : 0.004"  # scripted group (container) (typed FeaturePython)
  n = 0.003973
FEATURE [App::DocumentObjectGroupPython] G4_C_552  label="G4_C-552"  # scripted group (container) (typed FeaturePython)
  Dunit = g/cm3
  Dvalue = 1.76
  Group = -> [H_element020,C_element021,O_element019,F_element004,Si_element001]
  conduct = 2
  density = 1
  expand = 3
  formula = G4_C-552
  name = G4_C-552
  specific = 4
FEATURE [App::DocumentObjectGroupPython] Cd_element001  label="Cd_element : 1"  # scripted group (container) (typed FeaturePython)
  n = 1
  ref = Cd_element
FEATURE [App::DocumentObjectGroupPython] Te_element001  label="Te_element : 1"  # scripted group (container) (typed FeaturePython)
  n = 1
  ref = Te_element
FEATURE [App::DocumentObjectGroupPython] G4_CADMIUM_TELLURIDE  # scripted group (container) (typed FeaturePython)
  Dunit = g/cm3
  Dvalue = 6.2
  Group = -> [Cd_element001,Te_element001]
  conduct = 2
  density = 1
  expand = 3
  formula = G4_CADMIUM_TELLURIDE
  name = G4_CADMIUM_TELLURIDE
  specific = 4
FEATURE [App::DocumentObjectGroupPython] Cd_element002  label="Cd_element : 002"  # scripted group (container) (typed FeaturePython)
  n = 1
  ref = Cd_element
FEATURE [App::DocumentObjectGroupPython] W_element001  label="W_element : 1"  # scripted group (container) (typed FeaturePython)
  n = 1
  ref = W_element
FEATURE [App::DocumentObjectGroupPython] O_element020  label="O_element : 008"  # scripted group (container) (typed FeaturePython)
  n = 4
  ref = O_element
FEATURE [App::DocumentObjectGroupPython] G4_CADMIUM_TUNGSTATE  # scripted group (container) (typed FeaturePython)
  Dunit = g/cm3
  Dvalue = 7.9
  Group = -> [Cd_element002,W_element001,O_element020]
  conduct = 2
  density = 1
  expand = 3
  formula = G4_CADMIUM_TUNGSTATE
  name = G4_CADMIUM_TUNGSTATE
  specific = 4
FEATURE [App::DocumentObjectGroupPython] Ca_element005  label="Ca_element : 1"  # scripted group (container) (typed FeaturePython)
  n = 1
  ref = Ca_element
FEATURE [App::DocumentObjectGroupPython] C_element022  label="C_element : 009"  # scripted group (container) (typed FeaturePython)
  n = 1
  ref = C_element
FEATURE [App::DocumentObjectGroupPython] O_element021  label="O_element : 009"  # scripted group (container) (typed FeaturePython)
  n = 3
  ref = O_element
FEATURE [App::DocumentObjectGroupPython] G4_CALCIUM_CARBONATE  # scripted group (container) (typed FeaturePython)
  Dunit = g/cm3
  Dvalue = 2.8
  Group = -> [Ca_element005,C_element022,O_element021]
  conduct = 2
  density = 1
  expand = 3
  formula = G4_CALCIUM_CARBONATE
  name = G4_CALCIUM_CARBONATE
  specific = 4
FEATURE [App::DocumentObjectGroupPython] Ca_element006  label="Ca_element : 002"  # scripted group (container) (typed FeaturePython)
  n = 1
  ref = Ca_element
FEATURE [App::DocumentObjectGroupPython] F_element005  label="F_element : 003"  # scripted group (container) (typed FeaturePython)
  n = 2
  ref = F_element
FEATURE [App::DocumentObjectGroupPython] G4_CALCIUM_FLUORIDE  # scripted group (container) (typed FeaturePython)
  Dunit = g/cm3
  Dvalue = 3.18
  Group = -> [Ca_element006,F_element005]
  conduct = 2
  density = 1
  expand = 3
  formula = G4_CALCIUM_FLUORIDE
  name = G4_CALCIUM_FLUORIDE
  specific = 4
FEATURE [App::DocumentObjectGroupPython] Ca_element007  label="Ca_element : 003"  # scripted group (container) (typed FeaturePython)
  n = 1
  ref = Ca_element
FEATURE [App::DocumentObjectGroupPython] O_element022  label="O_element : 010"  # scripted group (container) (typed FeaturePython)
  n = 1
  ref = O_element
FEATURE [App::DocumentObjectGroupPython] G4_CALCIUM_OXIDE  # scripted group (container) (typed FeaturePython)
  Dunit = g/cm3
  Dvalue = 3.3
  Group = -> [Ca_element007,O_element022]
  conduct = 2
  density = 1
  expand = 3
  formula = G4_CALCIUM_OXIDE
  name = G4_CALCIUM_OXIDE
  specific = 4
FEATURE [App::DocumentObjectGroupPython] Ca_element008  label="Ca_element : 004"  # scripted group (container) (typed FeaturePython)
  n = 1
  ref = Ca_element
FEATURE [App::DocumentObjectGroupPython] S_element007  label="S_element : 002"  # scripted group (container) (typed FeaturePython)
  n = 1
  ref = S_element
FEATURE [App::DocumentObjectGroupPython] O_element023  label="O_element : 011"  # scripted group (container) (typed FeaturePython)
  n = 4
  ref = O_element
FEATURE [App::DocumentObjectGroupPython] G4_CALCIUM_SULFATE  # scripted group (container) (typed FeaturePython)
  Dunit = g/cm3
  Dvalue = 2.96
  Group = -> [Ca_element008,S_element007,O_element023]
  conduct = 2
  density = 1
  expand = 3
  formula = G4_CALCIUM_SULFATE
  name = G4_CALCIUM_SULFATE
  specific = 4
FEATURE [App::DocumentObjectGroupPython] Ca_element009  label="Ca_element : 005"  # scripted group (container) (typed FeaturePython)
  n = 1
  ref = Ca_element
FEATURE [App::DocumentObjectGroupPython] W_element002  label="W_element : 002"  # scripted group (container) (typed FeaturePython)
  n = 1
  ref = W_element
FEATURE [App::DocumentObjectGroupPython] O_element024  label="O_element : 012"  # scripted group (container) (typed FeaturePython)
  n = 4
  ref = O_element
FEATURE [App::DocumentObjectGroupPython] G4_CALCIUM_TUNGSTATE  # scripted group (container) (typed FeaturePython)
  Dunit = g/cm3
  Dvalue = 6.062
  Group = -> [Ca_element009,W_element002,O_element024]
  conduct = 2
  density = 1
  expand = 3
  formula = G4_CALCIUM_TUNGSTATE
  name = G4_CALCIUM_TUNGSTATE
  specific = 4
FEATURE [App::DocumentObjectGroupPython] C_element023  label="C_element : 010"  # scripted group (container) (typed FeaturePython)
  n = 1
  ref = C_element
FEATURE [App::DocumentObjectGroupPython] O_element025  label="O_element : 013"  # scripted group (container) (typed FeaturePython)
  n = 2
  ref = O_element
FEATURE [App::DocumentObjectGroupPython] G4_CARBON_DIOXIDE  # scripted group (container) (typed FeaturePython)
  Dunit = g/cm3
  Dvalue = 0.00184212
  Group = -> [C_element023,O_element025]
  conduct = 2
  density = 1
  expand = 3
  formula = G4_CARBON_DIOXIDE
  name = G4_CARBON_DIOXIDE
  specific = 4
FEATURE [App::DocumentObjectGroupPython] C_element024  label="C_element : 011"  # scripted group (container) (typed FeaturePython)
  n = 1
  ref = C_element
FEATURE [App::DocumentObjectGroupPython] Cl_element004  label="Cl_element : 4"  # scripted group (container) (typed FeaturePython)
  n = 4
  ref = Cl_element
FEATURE [App::DocumentObjectGroupPython] G4_CARBON_TETRACHLORIDE  # scripted group (container) (typed FeaturePython)
  Dunit = g/cm3
  Dvalue = 1.594
  Group = -> [C_element024,Cl_element004]
  conduct = 2
  density = 1
  expand = 3
  formula = G4_CARBON_TETRACHLORIDE
  name = G4_CARBON_TETRACHLORIDE
  specific = 4
FEATURE [App::DocumentObjectGroupPython] C_element025  label="C_element : 012"  # scripted group (container) (typed FeaturePython)
  n = 6
  ref = C_element
FEATURE [App::DocumentObjectGroupPython] H_element021  label="H_element : 012"  # scripted group (container) (typed FeaturePython)
  n = 10
  ref = H_element
FEATURE [App::DocumentObjectGroupPython] O_element026  label="O_element : 5"  # scripted group (container) (typed FeaturePython)
  n = 5
  ref = O_element
FEATURE [App::DocumentObjectGroupPython] G4_CELLULOSE_CELLOPHANE  # scripted group (container) (typed FeaturePython)
  Dunit = g/cm3
  Dvalue = 1.42
  Group = -> [C_element025,H_element021,O_element026]
  conduct = 2
  density = 1
  expand = 3
  formula = G4_CELLULOSE_CELLOPHANE
  name = G4_CELLULOSE_CELLOPHANE
  specific = 4
FEATURE [App::DocumentObjectGroupPython] H_element022  label="H_element : 0.067"  # scripted group (container) (typed FeaturePython)
  n = 0.067125
FEATURE [App::DocumentObjectGroupPython] C_element026  label="C_element : 0.545"  # scripted group (container) (typed FeaturePython)
  n = 0.545403
FEATURE [App::DocumentObjectGroupPython] O_element027  label="O_element : 0.387"  # scripted group (container) (typed FeaturePython)
  n = 0.387472
FEATURE [App::DocumentObjectGroupPython] G4_CELLULOSE_BUTYRATE  # scripted group (container) (typed FeaturePython)
  Dunit = g/cm3
  Dvalue = 1.2
  Group = -> [H_element022,C_element026,O_element027]
  conduct = 2
  density = 1
  expand = 3
  formula = G4_CELLULOSE_BUTYRATE
  name = G4_CELLULOSE_BUTYRATE
  specific = 4
FEATURE [App::DocumentObjectGroupPython] H_element023  label="H_element : 0.029"  # scripted group (container) (typed FeaturePython)
  n = 0.029216
FEATURE [App::DocumentObjectGroupPython] C_element027  label="C_element : 0.271"  # scripted group (container) (typed FeaturePython)
  n = 0.271296
FEATURE [App::DocumentObjectGroupPython] N_element013  label="N_element : 0.121"  # scripted group (container) (typed FeaturePython)
  n = 0.121276
FEATURE [App::DocumentObjectGroupPython] O_element028  label="O_element : 0.578"  # scripted group (container) (typed FeaturePython)
  n = 0.578212
FEATURE [App::DocumentObjectGroupPython] G4_CELLULOSE_NITRATE  # scripted group (container) (typed FeaturePython)
  Dunit = g/cm3
  Dvalue = 1.49
  Group = -> [H_element023,C_element027,N_element013,O_element028]
  conduct = 2
  density = 1
  expand = 3
  formula = G4_CELLULOSE_NITRATE
  name = G4_CELLULOSE_NITRATE
  specific = 4
FEATURE [App::DocumentObjectGroupPython] H_element024  label="H_element : 0.108"  # scripted group (container) (typed FeaturePython)
  n = 0.107596
FEATURE [App::DocumentObjectGroupPython] N_element014  label="N_element : 0.001"  # scripted group (container) (typed FeaturePython)
  n = 0.0008
FEATURE [App::DocumentObjectGroupPython] O_element029  label="O_element : 0.875"  # scripted group (container) (typed FeaturePython)
  n = 0.874976
FEATURE [App::DocumentObjectGroupPython] S_element008  label="S_element : 0.015"  # scripted group (container) (typed FeaturePython)
  n = 0.014627
FEATURE [App::DocumentObjectGroupPython] Ce_element001  label="Ce_element : 0.002"  # scripted group (container) (typed FeaturePython)
  n = 0.002001
FEATURE [App::DocumentObjectGroupPython] G4_CERIC_SULFATE  # scripted group (container) (typed FeaturePython)
  Dunit = g/cm3
  Dvalue = 1.03
  Group = -> [H_element024,N_element014,O_element029,S_element008,Ce_element001]
  conduct = 2
  density = 1
  expand = 3
  formula = G4_CERIC_SULFATE
  name = G4_CERIC_SULFATE
  specific = 4
FEATURE [App::DocumentObjectGroupPython] Cs_element001  label="Cs_element : 1"  # scripted group (container) (typed FeaturePython)
  n = 1
  ref = Cs_element
FEATURE [App::DocumentObjectGroupPython] F_element006  label="F_element : 1"  # scripted group (container) (typed FeaturePython)
  n = 1
  ref = F_element
FEATURE [App::DocumentObjectGroupPython] G4_CESIUM_FLUORIDE  # scripted group (container) (typed FeaturePython)
  Dunit = g/cm3
  Dvalue = 4.115
  Group = -> [Cs_element001,F_element006]
  conduct = 2
  density = 1
  expand = 3
  formula = G4_CESIUM_FLUORIDE
  name = G4_CESIUM_FLUORIDE
  specific = 4
FEATURE [App::DocumentObjectGroupPython] Cs_element002  label="Cs_element : 002"  # scripted group (container) (typed FeaturePython)
  n = 1
  ref = Cs_element
FEATURE [App::DocumentObjectGroupPython] I_element001  label="I_element : 1"  # scripted group (container) (typed FeaturePython)
  n = 1
  ref = I_element
FEATURE [App::DocumentObjectGroupPython] G4_CESIUM_IODIDE  # scripted group (container) (typed FeaturePython)
  Dunit = g/cm3
  Dvalue = 4.51
  Group = -> [Cs_element002,I_element001]
  conduct = 2
  density = 1
  expand = 3
  formula = G4_CESIUM_IODIDE
  name = G4_CESIUM_IODIDE
  specific = 4
FEATURE [App::DocumentObjectGroupPython] C_element028  label="C_element : 013"  # scripted group (container) (typed FeaturePython)
  n = 6
  ref = C_element
FEATURE [App::DocumentObjectGroupPython] H_element025  label="H_element : 013"  # scripted group (container) (typed FeaturePython)
  n = 5
  ref = H_element
FEATURE [App::DocumentObjectGroupPython] Cl_element005  label="Cl_element : 1"  # scripted group (container) (typed FeaturePython)
  n = 1
  ref = Cl_element
FEATURE [App::DocumentObjectGroupPython] G4_CHLOROBENZENE  # scripted group (container) (typed FeaturePython)
  Dunit = g/cm3
  Dvalue = 1.1058
  Group = -> [C_element028,H_element025,Cl_element005]
  conduct = 2
  density = 1
  expand = 3
  formula = G4_CHLOROBENZENE
  name = G4_CHLOROBENZENE
  specific = 4
FEATURE [App::DocumentObjectGroupPython] C_element029  label="C_element : 014"  # scripted group (container) (typed FeaturePython)
  n = 1
  ref = C_element
FEATURE [App::DocumentObjectGroupPython] H_element026  label="H_element : 1"  # scripted group (container) (typed FeaturePython)
  n = 1
  ref = H_element
FEATURE [App::DocumentObjectGroupPython] Cl_element006  label="Cl_element : 3"  # scripted group (container) (typed FeaturePython)
  n = 3
  ref = Cl_element
FEATURE [App::DocumentObjectGroupPython] G4_CHLOROFORM  # scripted group (container) (typed FeaturePython)
  Dunit = g/cm3
  Dvalue = 1.4832
  Group = -> [C_element029,H_element026,Cl_element006]
  conduct = 2
  density = 1
  expand = 3
  formula = G4_CHLOROFORM
  name = G4_CHLOROFORM
  specific = 4
FEATURE [App::DocumentObjectGroupPython] H_element027  label="H_element : 0.010"  # scripted group (container) (typed FeaturePython)
  n = 0.01
FEATURE [App::DocumentObjectGroupPython] C_element030  label="C_element : 0.001"  # scripted group (container) (typed FeaturePython)
  n = 0.001
FEATURE [App::DocumentObjectGroupPython] O_element030  label="O_element : 0.529"  # scripted group (container) (typed FeaturePython)
  n = 0.529107
FEATURE [App::DocumentObjectGroupPython] Na_element005  label="Na_element : 0.016"  # scripted group (container) (typed FeaturePython)
  n = 0.016
FEATURE [App::DocumentObjectGroupPython] Mg_element003  label="Mg_element : 0.004"  # scripted group (container) (typed FeaturePython)
  n = 0.002
FEATURE [App::DocumentObjectGroupPython] Al_element002  label="Al_element : 0.034"  # scripted group (container) (typed FeaturePython)
  n = 0.033872
FEATURE [App::DocumentObjectGroupPython] Si_element002  label="Si_element : 0.337"  # scripted group (container) (typed FeaturePython)
  n = 0.337021
FEATURE [App::DocumentObjectGroupPython] K_element003  label="K_element : 0.013"  # scripted group (container) (typed FeaturePython)
  n = 0.013
FEATURE [App::DocumentObjectGroupPython] Ca_element010  label="Ca_element : 0.044"  # scripted group (container) (typed FeaturePython)
  n = 0.044
FEATURE [App::DocumentObjectGroupPython] Fe_element002  label="Fe_element : 0.014"  # scripted group (container) (typed FeaturePython)
  n = 0.014
FEATURE [App::DocumentObjectGroupPython] G4_CONCRETE  # scripted group (container) (typed FeaturePython)
  Dunit = g/cm3
  Dvalue = 2.3
  Group = -> [H_element027,C_element030,O_element030,Na_element005,Mg_element003,Al_element002,Si_element002,K_element003,Ca_element010,Fe_element002]
  conduct = 2
  density = 1
  expand = 3
  formula = G4_CONCRETE
  name = G4_CONCRETE
  specific = 4
FEATURE [App::DocumentObjectGroupPython] C_element031  label="C_element : 015"  # scripted group (container) (typed FeaturePython)
  n = 6
  ref = C_element
FEATURE [App::DocumentObjectGroupPython] H_element028  label="H_element : 12"  # scripted group (container) (typed FeaturePython)
  n = 12
  ref = H_element
FEATURE [App::DocumentObjectGroupPython] G4_CYCLOHEXANE  # scripted group (container) (typed FeaturePython)
  Dunit = g/cm3
  Dvalue = 0.779
  Group = -> [C_element031,H_element028]
  conduct = 2
  density = 1
  expand = 3
  formula = G4_CYCLOHEXANE
  name = G4_CYCLOHEXANE
  specific = 4
FEATURE [App::DocumentObjectGroupPython] C_element032  label="C_element : 016"  # scripted group (container) (typed FeaturePython)
  n = 6
  ref = C_element
FEATURE [App::DocumentObjectGroupPython] H_element029  label="H_element : 4"  # scripted group (container) (typed FeaturePython)
  n = 4
  ref = H_element
FEATURE [App::DocumentObjectGroupPython] Cl_element007  label="Cl_element : 2"  # scripted group (container) (typed FeaturePython)
  n = 2
  ref = Cl_element
FEATURE [App::DocumentObjectGroupPython] G4_1_2_DICHLOROBENZENE  label="G4_1.2-DICHLOROBENZENE"  # scripted group (container) (typed FeaturePython)
  Dunit = g/cm3
  Dvalue = 1.3048
  Group = -> [C_element032,H_element029,Cl_element007]
  conduct = 2
  density = 1
  expand = 3
  formula = G4_1.2-DICHLOROBENZENE
  name = G4_1.2-DICHLOROBENZENE
  specific = 4
FEATURE [App::DocumentObjectGroupPython] C_element033  label="C_element : 017"  # scripted group (container) (typed FeaturePython)
  n = 4
  ref = C_element
FEATURE [App::DocumentObjectGroupPython] H_element030  label="H_element : 8"  # scripted group (container) (typed FeaturePython)
  n = 8
  ref = H_element
FEATURE [App::DocumentObjectGroupPython] O_element031  label="O_element : 014"  # scripted group (container) (typed FeaturePython)
  n = 1
  ref = O_element
FEATURE [App::DocumentObjectGroupPython] Cl_element008  label="Cl_element : 005"  # scripted group (container) (typed FeaturePython)
  n = 2
  ref = Cl_element
FEATURE [App::DocumentObjectGroupPython] G4_DICHLORODIETHYL_ETHER  # scripted group (container) (typed FeaturePython)
  Dunit = g/cm3
  Dvalue = 1.2199
  Group = -> [C_element033,H_element030,O_element031,Cl_element008]
  conduct = 2
  density = 1
  expand = 3
  formula = G4_DICHLORODIETHYL_ETHER
  name = G4_DICHLORODIETHYL_ETHER
  specific = 4
FEATURE [App::DocumentObjectGroupPython] C_element034  label="C_element : 018"  # scripted group (container) (typed FeaturePython)
  n = 2
  ref = C_element
FEATURE [App::DocumentObjectGroupPython] H_element031  label="H_element : 014"  # scripted group (container) (typed FeaturePython)
  n = 4
  ref = H_element
FEATURE [App::DocumentObjectGroupPython] Cl_element009  label="Cl_element : 006"  # scripted group (container) (typed FeaturePython)
  n = 2
  ref = Cl_element
FEATURE [App::DocumentObjectGroupPython] G4_1_2_DICHLOROETHANE  label="G4_1.2-DICHLOROETHANE"  # scripted group (container) (typed FeaturePython)
  Dunit = g/cm3
  Dvalue = 1.2351
  Group = -> [C_element034,H_element031,Cl_element009]
  conduct = 2
  density = 1
  expand = 3
  formula = G4_1.2-DICHLOROETHANE
  name = G4_1.2-DICHLOROETHANE
  specific = 4
FEATURE [App::DocumentObjectGroupPython] C_element035  label="C_element : 019"  # scripted group (container) (typed FeaturePython)
  n = 4
  ref = C_element
FEATURE [App::DocumentObjectGroupPython] H_element032  label="H_element : 015"  # scripted group (container) (typed FeaturePython)
  n = 10
  ref = H_element
FEATURE [App::DocumentObjectGroupPython] O_element032  label="O_element : 015"  # scripted group (container) (typed FeaturePython)
  n = 1
  ref = O_element
FEATURE [App::DocumentObjectGroupPython] G4_DIETHYL_ETHER  # scripted group (container) (typed FeaturePython)
  Dunit = g/cm3
  Dvalue = 0.71378
  Group = -> [C_element035,H_element032,O_element032]
  conduct = 2
  density = 1
  expand = 3
  formula = G4_DIETHYL_ETHER
  name = G4_DIETHYL_ETHER
  specific = 4
FEATURE [App::DocumentObjectGroupPython] C_element036  label="C_element : 020"  # scripted group (container) (typed FeaturePython)
  n = 3
  ref = C_element
FEATURE [App::DocumentObjectGroupPython] H_element033  label="H_element : 016"  # scripted group (container) (typed FeaturePython)
  n = 7
  ref = H_element
FEATURE [App::DocumentObjectGroupPython] N_element015  label="N_element : 008"  # scripted group (container) (typed FeaturePython)
  n = 1
  ref = N_element
FEATURE [App::DocumentObjectGroupPython] O_element033  label="O_element : 016"  # scripted group (container) (typed FeaturePython)
  n = 1
  ref = O_element
FEATURE [App::DocumentObjectGroupPython] G4_N_N_DIMETHYL_FORMAMIDE  label="G4_N.N-DIMETHYL_FORMAMIDE"  # scripted group (container) (typed FeaturePython)
  Dunit = g/cm3
  Dvalue = 0.9487
  Group = -> [C_element036,H_element033,N_element015,O_element033]
  conduct = 2
  density = 1
  expand = 3
  formula = G4_N.N-DIMETHYL_FORMAMIDE
  name = G4_N.N-DIMETHYL_FORMAMIDE
  specific = 4
FEATURE [App::DocumentObjectGroupPython] C_element037  label="C_element : 021"  # scripted group (container) (typed FeaturePython)
  n = 2
  ref = C_element
FEATURE [App::DocumentObjectGroupPython] H_element034  label="H_element : 017"  # scripted group (container) (typed FeaturePython)
  n = 6
  ref = H_element
FEATURE [App::DocumentObjectGroupPython] O_element034  label="O_element : 017"  # scripted group (container) (typed FeaturePython)
  n = 1
  ref = O_element
FEATURE [App::DocumentObjectGroupPython] S_element009  label="S_element : 003"  # scripted group (container) (typed FeaturePython)
  n = 1
  ref = S_element
FEATURE [App::DocumentObjectGroupPython] G4_DIMETHYL_SULFOXIDE  # scripted group (container) (typed FeaturePython)
  Dunit = g/cm3
  Dvalue = 1.1014
  Group = -> [C_element037,H_element034,O_element034,S_element009]
  conduct = 2
  density = 1
  expand = 3
  formula = G4_DIMETHYL_SULFOXIDE
  name = G4_DIMETHYL_SULFOXIDE
  specific = 4
FEATURE [App::DocumentObjectGroupPython] C_element038  label="C_element : 022"  # scripted group (container) (typed FeaturePython)
  n = 2
  ref = C_element
FEATURE [App::DocumentObjectGroupPython] H_element035  label="H_element : 018"  # scripted group (container) (typed FeaturePython)
  n = 6
  ref = H_element
FEATURE [App::DocumentObjectGroupPython] G4_ETHANE  # scripted group (container) (typed FeaturePython)
  Dunit = g/cm3
  Dvalue = 0.00125324
  Group = -> [C_element038,H_element035]
  conduct = 2
  density = 1
  expand = 3
  formula = G4_ETHANE
  name = G4_ETHANE
  specific = 4
FEATURE [App::DocumentObjectGroupPython] C_element039  label="C_element : 023"  # scripted group (container) (typed FeaturePython)
  n = 2
  ref = C_element
FEATURE [App::DocumentObjectGroupPython] H_element036  label="H_element : 019"  # scripted group (container) (typed FeaturePython)
  n = 6
  ref = H_element
FEATURE [App::DocumentObjectGroupPython] O_element035  label="O_element : 018"  # scripted group (container) (typed FeaturePython)
  n = 1
  ref = O_element
FEATURE [App::DocumentObjectGroupPython] G4_ETHYL_ALCOHOL  # scripted group (container) (typed FeaturePython)
  Dunit = g/cm3
  Dvalue = 0.7893
  Group = -> [C_element039,H_element036,O_element035]
  conduct = 2
  density = 1
  expand = 3
  formula = G4_ETHYL_ALCOHOL
  name = G4_ETHYL_ALCOHOL
  specific = 4
FEATURE [App::DocumentObjectGroupPython] H_element037  label="H_element : 0.090"  # scripted group (container) (typed FeaturePython)
  n = 0.090027
FEATURE [App::DocumentObjectGroupPython] C_element040  label="C_element : 0.585"  # scripted group (container) (typed FeaturePython)
  n = 0.585182
FEATURE [App::DocumentObjectGroupPython] O_element036  label="O_element : 0.325"  # scripted group (container) (typed FeaturePython)
  n = 0.324791
FEATURE [App::DocumentObjectGroupPython] G4_ETHYL_CELLULOSE  # scripted group (container) (typed FeaturePython)
  Dunit = g/cm3
  Dvalue = 1.13
  Group = -> [H_element037,C_element040,O_element036]
  conduct = 2
  density = 1
  expand = 3
  formula = G4_ETHYL_CELLULOSE
  name = G4_ETHYL_CELLULOSE
  specific = 4
FEATURE [App::DocumentObjectGroupPython] C_element041  label="C_element : 024"  # scripted group (container) (typed FeaturePython)
  n = 2
  ref = C_element
FEATURE [App::DocumentObjectGroupPython] H_element038  label="H_element : 020"  # scripted group (container) (typed FeaturePython)
  n = 4
  ref = H_element
FEATURE [App::DocumentObjectGroupPython] G4_ETHYLENE  # scripted group (container) (typed FeaturePython)
  Dunit = g/cm3
  Dvalue = 0.00117497
  Group = -> [C_element041,H_element038]
  conduct = 2
  density = 1
  expand = 3
  formula = G4_ETHYLENE
  name = G4_ETHYLENE
  specific = 4
FEATURE [App::DocumentObjectGroupPython] H_element039  label="H_element : 0.096"  # scripted group (container) (typed FeaturePython)
  n = 0.096
FEATURE [App::DocumentObjectGroupPython] C_element042  label="C_element : 0.195"  # scripted group (container) (typed FeaturePython)
  n = 0.195
FEATURE [App::DocumentObjectGroupPython] N_element016  label="N_element : 0.057"  # scripted group (container) (typed FeaturePython)
  n = 0.057
FEATURE [App::DocumentObjectGroupPython] O_element037  label="O_element : 0.646"  # scripted group (container) (typed FeaturePython)
  n = 0.646
FEATURE [App::DocumentObjectGroupPython] Na_element006  label="Na_element : 0.017"  # scripted group (container) (typed FeaturePython)
  n = 0.001
FEATURE [App::DocumentObjectGroupPython] P_element005  label="P_element : 0.104"  # scripted group (container) (typed FeaturePython)
  n = 0.001
FEATURE [App::DocumentObjectGroupPython] S_element010  label="S_element : 0.016"  # scripted group (container) (typed FeaturePython)
  n = 0.003
FEATURE [App::DocumentObjectGroupPython] Cl_element010  label="Cl_element : 0.005"  # scripted group (container) (typed FeaturePython)
  n = 0.001
FEATURE [App::DocumentObjectGroupPython] G4_EYE_LENS_ICRP  # scripted group (container) (typed FeaturePython)
  Dunit = g/cm3
  Dvalue = 1.07
  Group = -> [H_element039,C_element042,N_element016,O_element037,Na_element006,P_element005,S_element010,Cl_element010]
  conduct = 2
  density = 1
  expand = 3
  formula = G4_EYE_LENS_ICRP
  name = G4_EYE_LENS_ICRP
  specific = 4
FEATURE [App::DocumentObjectGroupPython] Fe_element003  label="Fe_element : 2"  # scripted group (container) (typed FeaturePython)
  n = 2
  ref = Fe_element
FEATURE [App::DocumentObjectGroupPython] O_element038  label="O_element : 019"  # scripted group (container) (typed FeaturePython)
  n = 3
  ref = O_element
FEATURE [App::DocumentObjectGroupPython] G4_FERRIC_OXIDE  # scripted group (container) (typed FeaturePython)
  Dunit = g/cm3
  Dvalue = 5.2
  Group = -> [Fe_element003,O_element038]
  conduct = 2
  density = 1
  expand = 3
  formula = G4_FERRIC_OXIDE
  name = G4_FERRIC_OXIDE
  specific = 4
FEATURE [App::DocumentObjectGroupPython] Fe_element004  label="Fe_element : 1"  # scripted group (container) (typed FeaturePython)
  n = 1
  ref = Fe_element
FEATURE [App::DocumentObjectGroupPython] B_element003  label="B_element : 1"  # scripted group (container) (typed FeaturePython)
  n = 1
  ref = B_element
FEATURE [App::DocumentObjectGroupPython] G4_FERROBORIDE  # scripted group (container) (typed FeaturePython)
  Dunit = g/cm3
  Dvalue = 7.15
  Group = -> [Fe_element004,B_element003]
  conduct = 2
  density = 1
  expand = 3
  formula = G4_FERROBORIDE
  name = G4_FERROBORIDE
  specific = 4
FEATURE [App::DocumentObjectGroupPython] Fe_element005  label="Fe_element : 003"  # scripted group (container) (typed FeaturePython)
  n = 1
  ref = Fe_element
FEATURE [App::DocumentObjectGroupPython] O_element039  label="O_element : 020"  # scripted group (container) (typed FeaturePython)
  n = 1
  ref = O_element
FEATURE [App::DocumentObjectGroupPython] G4_FERROUS_OXIDE  # scripted group (container) (typed FeaturePython)
  Dunit = g/cm3
  Dvalue = 5.7
  Group = -> [Fe_element005,O_element039]
  conduct = 2
  density = 1
  expand = 3
  formula = G4_FERROUS_OXIDE
  name = G4_FERROUS_OXIDE
  specific = 4
FEATURE [App::DocumentObjectGroupPython] H_element040  label="H_element : 0.115"  # scripted group (container) (typed FeaturePython)
  n = 0.108259
FEATURE [App::DocumentObjectGroupPython] N_element017  label="N_element : 0.000"  # scripted group (container) (typed FeaturePython)
  n = 2.7e-05
FEATURE [App::DocumentObjectGroupPython] O_element040  label="O_element : 0.879"  # scripted group (container) (typed FeaturePython)
  n = 0.878636
FEATURE [App::DocumentObjectGroupPython] Na_element007  label="Na_element : 0.000"  # scripted group (container) (typed FeaturePython)
  n = 2.2e-05
FEATURE [App::DocumentObjectGroupPython] S_element011  label="S_element : 0.013"  # scripted group (container) (typed FeaturePython)
  n = 0.012968
FEATURE [App::DocumentObjectGroupPython] Cl_element011  label="Cl_element : 0.000"  # scripted group (container) (typed FeaturePython)
  n = 3.4e-05
FEATURE [App::DocumentObjectGroupPython] Fe_element006  label="Fe_element : 0.000"  # scripted group (container) (typed FeaturePython)
  n = 5.4e-05
FEATURE [App::DocumentObjectGroupPython] G4_FERROUS_SULFATE  # scripted group (container) (typed FeaturePython)
  Dunit = g/cm3
  Dvalue = 1.024
  Group = -> [H_element040,N_element017,O_element040,Na_element007,S_element011,Cl_element011,Fe_element006]
  conduct = 2
  density = 1
  expand = 3
  formula = G4_FERROUS_SULFATE
  name = G4_FERROUS_SULFATE
  specific = 4
FEATURE [App::DocumentObjectGroupPython] C_element043  label="C_element : 0.099"  # scripted group (container) (typed FeaturePython)
  n = 0.099335
FEATURE [App::DocumentObjectGroupPython] F_element007  label="F_element : 0.314"  # scripted group (container) (typed FeaturePython)
  n = 0.314247
FEATURE [App::DocumentObjectGroupPython] Cl_element012  label="Cl_element : 0.586"  # scripted group (container) (typed FeaturePython)
  n = 0.586418
FEATURE [App::DocumentObjectGroupPython] G4_FREON_12  label="G4_FREON-12"  # scripted group (container) (typed FeaturePython)
  Dunit = g/cm3
  Dvalue = 1.12
  Group = -> [C_element043,F_element007,Cl_element012]
  conduct = 2
  density = 1
  expand = 3
  formula = G4_FREON-12
  name = G4_FREON-12
  specific = 4
FEATURE [App::DocumentObjectGroupPython] C_element044  label="C_element : 0.057"  # scripted group (container) (typed FeaturePython)
  n = 0.057245
FEATURE [App::DocumentObjectGroupPython] F_element008  label="F_element : 0.181"  # scripted group (container) (typed FeaturePython)
  n = 0.181096
FEATURE [App::DocumentObjectGroupPython] Br_element001  label="Br_element : 0.762"  # scripted group (container) (typed FeaturePython)
  n = 0.761659
FEATURE [App::DocumentObjectGroupPython] G4_FREON_12B2  label="G4_FREON-12B2"  # scripted group (container) (typed FeaturePython)
  Dunit = g/cm3
  Dvalue = 1.8
  Group = -> [C_element044,F_element008,Br_element001]
  conduct = 2
  density = 1
  expand = 3
  formula = G4_FREON-12B2
  name = G4_FREON-12B2
  specific = 4
FEATURE [App::DocumentObjectGroupPython] C_element045  label="C_element : 0.115"  # scripted group (container) (typed FeaturePython)
  n = 0.114983
FEATURE [App::DocumentObjectGroupPython] F_element009  label="F_element : 0.546"  # scripted group (container) (typed FeaturePython)
  n = 0.545621
FEATURE [App::DocumentObjectGroupPython] Cl_element013  label="Cl_element : 0.339"  # scripted group (container) (typed FeaturePython)
  n = 0.339396
FEATURE [App::DocumentObjectGroupPython] G4_FREON_13  label="G4_FREON-13"  # scripted group (container) (typed FeaturePython)
  Dunit = g/cm3
  Dvalue = 0.95
  Group = -> [C_element045,F_element009,Cl_element013]
  conduct = 2
  density = 1
  expand = 3
  formula = G4_FREON-13
  name = G4_FREON-13
  specific = 4
FEATURE [App::DocumentObjectGroupPython] C_element046  label="C_element : 025"  # scripted group (container) (typed FeaturePython)
  n = 1
  ref = C_element
FEATURE [App::DocumentObjectGroupPython] F_element010  label="F_element : 3"  # scripted group (container) (typed FeaturePython)
  n = 3
  ref = F_element
FEATURE [App::DocumentObjectGroupPython] Br_element002  label="Br_element : 1"  # scripted group (container) (typed FeaturePython)
  n = 1
  ref = Br_element
FEATURE [App::DocumentObjectGroupPython] G4_FREON_13B1  label="G4_FREON-13B1"  # scripted group (container) (typed FeaturePython)
  Dunit = g/cm3
  Dvalue = 1.5
  Group = -> [C_element046,F_element010,Br_element002]
  conduct = 2
  density = 1
  expand = 3
  formula = G4_FREON-13B1
  name = G4_FREON-13B1
  specific = 4
FEATURE [App::DocumentObjectGroupPython] C_element047  label="C_element : 0.061"  # scripted group (container) (typed FeaturePython)
  n = 0.061309
FEATURE [App::DocumentObjectGroupPython] F_element011  label="F_element : 0.291"  # scripted group (container) (typed FeaturePython)
  n = 0.290924
FEATURE [App::DocumentObjectGroupPython] I_element002  label="I_element : 0.648"  # scripted group (container) (typed FeaturePython)
  n = 0.647767
FEATURE [App::DocumentObjectGroupPython] G4_FREON_13I1  label="G4_FREON-13I1"  # scripted group (container) (typed FeaturePython)
  Dunit = g/cm3
  Dvalue = 1.8
  Group = -> [C_element047,F_element011,I_element002]
  conduct = 2
  density = 1
  expand = 3
  formula = G4_FREON-13I1
  name = G4_FREON-13I1
  specific = 4
FEATURE [App::DocumentObjectGroupPython] Gd_element001  label="Gd_element : 2"  # scripted group (container) (typed FeaturePython)
  n = 2
  ref = Gd_element
FEATURE [App::DocumentObjectGroupPython] O_element041  label="O_element : 021"  # scripted group (container) (typed FeaturePython)
  n = 2
  ref = O_element
FEATURE [App::DocumentObjectGroupPython] S_element012  label="S_element : 004"  # scripted group (container) (typed FeaturePython)
  n = 1
  ref = S_element
FEATURE [App::DocumentObjectGroupPython] G4_GADOLINIUM_OXYSULFIDE  # scripted group (container) (typed FeaturePython)
  Dunit = g/cm3
  Dvalue = 7.44
  Group = -> [Gd_element001,O_element041,S_element012]
  conduct = 2
  density = 1
  expand = 3
  formula = G4_GADOLINIUM_OXYSULFIDE
  name = G4_GADOLINIUM_OXYSULFIDE
  specific = 4
FEATURE [App::DocumentObjectGroupPython] Ga_element001  label="Ga_element : 1"  # scripted group (container) (typed FeaturePython)
  n = 1
  ref = Ga_element
FEATURE [App::DocumentObjectGroupPython] As_element001  label="As_element : 1"  # scripted group (container) (typed FeaturePython)
  n = 1
  ref = As_element
FEATURE [App::DocumentObjectGroupPython] G4_GALLIUM_ARSENIDE  # scripted group (container) (typed FeaturePython)
  Dunit = g/cm3
  Dvalue = 5.31
  Group = -> [Ga_element001,As_element001]
  conduct = 2
  density = 1
  expand = 3
  formula = G4_GALLIUM_ARSENIDE
  name = G4_GALLIUM_ARSENIDE
  specific = 4
FEATURE [App::DocumentObjectGroupPython] H_element041  label="H_element : 0.081"  # scripted group (container) (typed FeaturePython)
  n = 0.08118
FEATURE [App::DocumentObjectGroupPython] C_element048  label="C_element : 0.416"  # scripted group (container) (typed FeaturePython)
  n = 0.41606
FEATURE [App::DocumentObjectGroupPython] N_element018  label="N_element : 0.111"  # scripted group (container) (typed FeaturePython)
  n = 0.11124
FEATURE [App::DocumentObjectGroupPython] O_element042  label="O_element : 0.381"  # scripted group (container) (typed FeaturePython)
  n = 0.38064
FEATURE [App::DocumentObjectGroupPython] S_element013  label="S_element : 0.011"  # scripted group (container) (typed FeaturePython)
  n = 0.01088
FEATURE [App::DocumentObjectGroupPython] G4_GEL_PHOTO_EMULSION  # scripted group (container) (typed FeaturePython)
  Dunit = g/cm3
  Dvalue = 1.2914
  Group = -> [H_element041,C_element048,N_element018,O_element042,S_element013]
  conduct = 2
  density = 1
  expand = 3
  formula = G4_GEL_PHOTO_EMULSION
  name = G4_GEL_PHOTO_EMULSION
  specific = 4
FEATURE [App::DocumentObjectGroupPython] B_element004  label="B_element : 0.040"  # scripted group (container) (typed FeaturePython)
  n = 0.0400639
FEATURE [App::DocumentObjectGroupPython] O_element043  label="O_element : 0.540"  # scripted group (container) (typed FeaturePython)
  n = 0.539561
FEATURE [App::DocumentObjectGroupPython] Na_element008  label="Na_element : 0.028"  # scripted group (container) (typed FeaturePython)
  n = 0.0281909
FEATURE [App::DocumentObjectGroupPython] Al_element003  label="Al_element : 0.012"  # scripted group (container) (typed FeaturePython)
  n = 0.011644
FEATURE [App::DocumentObjectGroupPython] Si_element003  label="Si_element : 0.377"  # scripted group (container) (typed FeaturePython)
  n = 0.377219
FEATURE [App::DocumentObjectGroupPython] K_element004  label="K_element : 0.014"  # scripted group (container) (typed FeaturePython)
  n = 0.00332099
FEATURE [App::DocumentObjectGroupPython] G4_Pyrex_Glass  # scripted group (container) (typed FeaturePython)
  Dunit = g/cm3
  Dvalue = 2.23
  Group = -> [B_element004,O_element043,Na_element008,Al_element003,Si_element003,K_element004]
  conduct = 2
  density = 1
  expand = 3
  formula = G4_Pyrex_Glass
  name = G4_Pyrex_Glass
  specific = 4
FEATURE [App::DocumentObjectGroupPython] O_element044  label="O_element : 0.156"  # scripted group (container) (typed FeaturePython)
  n = 0.156453
FEATURE [App::DocumentObjectGroupPython] Si_element004  label="Si_element : 0.081"  # scripted group (container) (typed FeaturePython)
  n = 0.080866
FEATURE [App::DocumentObjectGroupPython] Ti_element001  label="Ti_element : 0.008"  # scripted group (container) (typed FeaturePython)
  n = 0.008092
FEATURE [App::DocumentObjectGroupPython] As_element002  label="As_element : 0.003"  # scripted group (container) (typed FeaturePython)
  n = 0.002651
FEATURE [App::DocumentObjectGroupPython] Pb_element001  label="Pb_element : 0.752"  # scripted group (container) (typed FeaturePython)
  n = 0.751938
FEATURE [App::DocumentObjectGroupPython] G4_GLASS_LEAD  # scripted group (container) (typed FeaturePython)
  Dunit = g/cm3
  Dvalue = 6.22
  Group = -> [O_element044,Si_element004,Ti_element001,As_element002,Pb_element001]
  conduct = 2
  density = 1
  expand = 3
  formula = G4_GLASS_LEAD
  name = G4_GLASS_LEAD
  specific = 4
FEATURE [App::DocumentObjectGroupPython] O_element045  label="O_element : 0.460"  # scripted group (container) (typed FeaturePython)
  n = 0.4598
FEATURE [App::DocumentObjectGroupPython] Na_element009  label="Na_element : 0.096"  # scripted group (container) (typed FeaturePython)
  n = 0.0964411
FEATURE [App::DocumentObjectGroupPython] Si_element005  label="Si_element : 0.378"  # scripted group (container) (typed FeaturePython)
  n = 0.336553
FEATURE [App::DocumentObjectGroupPython] Ca_element011  label="Ca_element : 0.107"  # scripted group (container) (typed FeaturePython)
  n = 0.107205
FEATURE [App::DocumentObjectGroupPython] G4_GLASS_PLATE  # scripted group (container) (typed FeaturePython)
  Dunit = g/cm3
  Dvalue = 2.4
  Group = -> [O_element045,Na_element009,Si_element005,Ca_element011]
  conduct = 2
  density = 1
  expand = 3
  formula = G4_GLASS_PLATE
  name = G4_GLASS_PLATE
  specific = 4
FEATURE [App::DocumentObjectGroupPython] C_element049  label="C_element : 026"  # scripted group (container) (typed FeaturePython)
  n = 5
  ref = C_element
FEATURE [App::DocumentObjectGroupPython] H_element042  label="H_element : 021"  # scripted group (container) (typed FeaturePython)
  n = 10
  ref = H_element
FEATURE [App::DocumentObjectGroupPython] N_element019  label="N_element : 2"  # scripted group (container) (typed FeaturePython)
  n = 2
  ref = N_element
FEATURE [App::DocumentObjectGroupPython] O_element046  label="O_element : 022"  # scripted group (container) (typed FeaturePython)
  n = 3
  ref = O_element
FEATURE [App::DocumentObjectGroupPython] G4_GLUTAMINE  # scripted group (container) (typed FeaturePython)
  Dunit = g/cm3
  Dvalue = 1.46
  Group = -> [C_element049,H_element042,N_element019,O_element046]
  conduct = 2
  density = 1
  expand = 3
  formula = G4_GLUTAMINE
  name = G4_GLUTAMINE
  specific = 4
FEATURE [App::DocumentObjectGroupPython] C_element050  label="C_element : 027"  # scripted group (container) (typed FeaturePython)
  n = 3
  ref = C_element
FEATURE [App::DocumentObjectGroupPython] H_element043  label="H_element : 022"  # scripted group (container) (typed FeaturePython)
  n = 8
  ref = H_element
FEATURE [App::DocumentObjectGroupPython] O_element047  label="O_element : 023"  # scripted group (container) (typed FeaturePython)
  n = 3
  ref = O_element
FEATURE [App::DocumentObjectGroupPython] G4_GLYCEROL  # scripted group (container) (typed FeaturePython)
  Dunit = g/cm3
  Dvalue = 1.2613
  Group = -> [C_element050,H_element043,O_element047]
  conduct = 2
  density = 1
  expand = 3
  formula = G4_GLYCEROL
  name = G4_GLYCEROL
  specific = 4
FEATURE [App::DocumentObjectGroupPython] C_element051  label="C_element : 028"  # scripted group (container) (typed FeaturePython)
  n = 5
  ref = C_element
FEATURE [App::DocumentObjectGroupPython] H_element044  label="H_element : 023"  # scripted group (container) (typed FeaturePython)
  n = 5
  ref = H_element
FEATURE [App::DocumentObjectGroupPython] N_element020  label="N_element : 009"  # scripted group (container) (typed FeaturePython)
  n = 5
  ref = N_element
FEATURE [App::DocumentObjectGroupPython] O_element048  label="O_element : 024"  # scripted group (container) (typed FeaturePython)
  n = 1
  ref = O_element
FEATURE [App::DocumentObjectGroupPython] G4_GUANINE  # scripted group (container) (typed FeaturePython)
  Dunit = g/cm3
  Dvalue = 2.2
  Group = -> [C_element051,H_element044,N_element020,O_element048]
  conduct = 2
  density = 1
  expand = 3
  formula = G4_GUANINE
  name = G4_GUANINE
  specific = 4
FEATURE [App::DocumentObjectGroupPython] Ca_element012  label="Ca_element : 006"  # scripted group (container) (typed FeaturePython)
  n = 1
  ref = Ca_element
FEATURE [App::DocumentObjectGroupPython] S_element014  label="S_element : 005"  # scripted group (container) (typed FeaturePython)
  n = 1
  ref = S_element
FEATURE [App::DocumentObjectGroupPython] O_element049  label="O_element : 6"  # scripted group (container) (typed FeaturePython)
  n = 6
  ref = O_element
FEATURE [App::DocumentObjectGroupPython] H_element045  label="H_element : 024"  # scripted group (container) (typed FeaturePython)
  n = 4
  ref = H_element
FEATURE [App::DocumentObjectGroupPython] G4_GYPSUM  # scripted group (container) (typed FeaturePython)
  Dunit = g/cm3
  Dvalue = 2.32
  Group = -> [Ca_element012,S_element014,O_element049,H_element045]
  conduct = 2
  density = 1
  expand = 3
  formula = G4_GYPSUM
  name = G4_GYPSUM
  specific = 4
FEATURE [App::DocumentObjectGroupPython] C_element052  label="C_element : 7"  # scripted group (container) (typed FeaturePython)
  n = 7
  ref = C_element
FEATURE [App::DocumentObjectGroupPython] H_element046  label="H_element : 16"  # scripted group (container) (typed FeaturePython)
  n = 16
  ref = H_element
FEATURE [App::DocumentObjectGroupPython] G4_N_HEPTANE  label="G4_N-HEPTANE"  # scripted group (container) (typed FeaturePython)
  Dunit = g/cm3
  Dvalue = 0.68376
  Group = -> [C_element052,H_element046]
  conduct = 2
  density = 1
  expand = 3
  formula = G4_N-HEPTANE
  name = G4_N-HEPTANE
  specific = 4
FEATURE [App::DocumentObjectGroupPython] C_element053  label="C_element : 029"  # scripted group (container) (typed FeaturePython)
  n = 6
  ref = C_element
FEATURE [App::DocumentObjectGroupPython] H_element047  label="H_element : 14"  # scripted group (container) (typed FeaturePython)
  n = 14
  ref = H_element
FEATURE [App::DocumentObjectGroupPython] G4_N_HEXANE  label="G4_N-HEXANE"  # scripted group (container) (typed FeaturePython)
  Dunit = g/cm3
  Dvalue = 0.6603
  Group = -> [C_element053,H_element047]
  conduct = 2
  density = 1
  expand = 3
  formula = G4_N-HEXANE
  name = G4_N-HEXANE
  specific = 4
FEATURE [App::DocumentObjectGroupPython] C_element054  label="C_element : 22"  # scripted group (container) (typed FeaturePython)
  n = 22
  ref = C_element
FEATURE [App::DocumentObjectGroupPython] H_element048  label="H_element : 025"  # scripted group (container) (typed FeaturePython)
  n = 10
  ref = H_element
FEATURE [App::DocumentObjectGroupPython] N_element021  label="N_element : 010"  # scripted group (container) (typed FeaturePython)
  n = 2
  ref = N_element
FEATURE [App::DocumentObjectGroupPython] O_element050  label="O_element : 025"  # scripted group (container) (typed FeaturePython)
  n = 5
  ref = O_element
FEATURE [App::DocumentObjectGroupPython] G4_KAPTON  # scripted group (container) (typed FeaturePython)
  Dunit = g/cm3
  Dvalue = 1.42
  Group = -> [C_element054,H_element048,N_element021,O_element050]
  conduct = 2
  density = 1
  expand = 3
  formula = G4_KAPTON
  name = G4_KAPTON
  specific = 4
FEATURE [App::DocumentObjectGroupPython] La_element001  label="La_element : 1"  # scripted group (container) (typed FeaturePython)
  n = 1
  ref = La_element
FEATURE [App::DocumentObjectGroupPython] Br_element003  label="Br_element : 002"  # scripted group (container) (typed FeaturePython)
  n = 1
  ref = Br_element
FEATURE [App::DocumentObjectGroupPython] O_element051  label="O_element : 026"  # scripted group (container) (typed FeaturePython)
  n = 1
  ref = O_element
FEATURE [App::DocumentObjectGroupPython] G4_LANTHANUM_OXYBROMIDE  # scripted group (container) (typed FeaturePython)
  Dunit = g/cm3
  Dvalue = 6.28
  Group = -> [La_element001,Br_element003,O_element051]
  conduct = 2
  density = 1
  expand = 3
  formula = G4_LANTHANUM_OXYBROMIDE
  name = G4_LANTHANUM_OXYBROMIDE
  specific = 4
FEATURE [App::DocumentObjectGroupPython] La_element002  label="La_element : 2"  # scripted group (container) (typed FeaturePython)
  n = 2
  ref = La_element
FEATURE [App::DocumentObjectGroupPython] O_element052  label="O_element : 027"  # scripted group (container) (typed FeaturePython)
  n = 2
  ref = O_element
FEATURE [App::DocumentObjectGroupPython] S_element015  label="S_element : 006"  # scripted group (container) (typed FeaturePython)
  n = 1
  ref = S_element
FEATURE [App::DocumentObjectGroupPython] G4_LANTHANUM_OXYSULFIDE  # scripted group (container) (typed FeaturePython)
  Dunit = g/cm3
  Dvalue = 5.86
  Group = -> [La_element002,O_element052,S_element015]
  conduct = 2
  density = 1
  expand = 3
  formula = G4_LANTHANUM_OXYSULFIDE
  name = G4_LANTHANUM_OXYSULFIDE
  specific = 4
FEATURE [App::DocumentObjectGroupPython] O_element053  label="O_element : 0.072"  # scripted group (container) (typed FeaturePython)
  n = 0.071682
FEATURE [App::DocumentObjectGroupPython] Pb_element002  label="Pb_element : 0.928"  # scripted group (container) (typed FeaturePython)
  n = 0.928318
FEATURE [App::DocumentObjectGroupPython] G4_LEAD_OXIDE  # scripted group (container) (typed FeaturePython)
  Dunit = g/cm3
  Dvalue = 9.53
  Group = -> [O_element053,Pb_element002]
  conduct = 2
  density = 1
  expand = 3
  formula = G4_LEAD_OXIDE
  name = G4_LEAD_OXIDE
  specific = 4
FEATURE [App::DocumentObjectGroupPython] Li_element001  label="Li_element : 1"  # scripted group (container) (typed FeaturePython)
  n = 1
  ref = Li_element
FEATURE [App::DocumentObjectGroupPython] N_element022  label="N_element : 011"  # scripted group (container) (typed FeaturePython)
  n = 1
  ref = N_element
FEATURE [App::DocumentObjectGroupPython] H_element049  label="H_element : 026"  # scripted group (container) (typed FeaturePython)
  n = 2
  ref = H_element
FEATURE [App::DocumentObjectGroupPython] G4_LITHIUM_AMIDE  # scripted group (container) (typed FeaturePython)
  Dunit = g/cm3
  Dvalue = 1.178
  Group = -> [Li_element001,N_element022,H_element049]
  conduct = 2
  density = 1
  expand = 3
  formula = G4_LITHIUM_AMIDE
  name = G4_LITHIUM_AMIDE
  specific = 4
FEATURE [App::DocumentObjectGroupPython] Li_element002  label="Li_element : 2"  # scripted group (container) (typed FeaturePython)
  n = 2
  ref = Li_element
FEATURE [App::DocumentObjectGroupPython] C_element055  label="C_element : 030"  # scripted group (container) (typed FeaturePython)
  n = 1
  ref = C_element
FEATURE [App::DocumentObjectGroupPython] O_element054  label="O_element : 028"  # scripted group (container) (typed FeaturePython)
  n = 3
  ref = O_element
FEATURE [App::DocumentObjectGroupPython] G4_LITHIUM_CARBONATE  # scripted group (container) (typed FeaturePython)
  Dunit = g/cm3
  Dvalue = 2.11
  Group = -> [Li_element002,C_element055,O_element054]
  conduct = 2
  density = 1
  expand = 3
  formula = G4_LITHIUM_CARBONATE
  name = G4_LITHIUM_CARBONATE
  specific = 4
FEATURE [App::DocumentObjectGroupPython] Li_element003  label="Li_element : 003"  # scripted group (container) (typed FeaturePython)
  n = 1
  ref = Li_element
FEATURE [App::DocumentObjectGroupPython] F_element012  label="F_element : 004"  # scripted group (container) (typed FeaturePython)
  n = 1
  ref = F_element
FEATURE [App::DocumentObjectGroupPython] G4_LITHIUM_FLUORIDE  # scripted group (container) (typed FeaturePython)
  Dunit = g/cm3
  Dvalue = 2.635
  Group = -> [Li_element003,F_element012]
  conduct = 2
  density = 1
  expand = 3
  formula = G4_LITHIUM_FLUORIDE
  name = G4_LITHIUM_FLUORIDE
  specific = 4
FEATURE [App::DocumentObjectGroupPython] Li_element004  label="Li_element : 004"  # scripted group (container) (typed FeaturePython)
  n = 1
  ref = Li_element
FEATURE [App::DocumentObjectGroupPython] H_element050  label="H_element : 027"  # scripted group (container) (typed FeaturePython)
  n = 1
  ref = H_element
FEATURE [App::DocumentObjectGroupPython] G4_LITHIUM_HYDRIDE  # scripted group (container) (typed FeaturePython)
  Dunit = g/cm3
  Dvalue = 0.82
  Group = -> [Li_element004,H_element050]
  conduct = 2
  density = 1
  expand = 3
  formula = G4_LITHIUM_HYDRIDE
  name = G4_LITHIUM_HYDRIDE
  specific = 4
FEATURE [App::DocumentObjectGroupPython] Li_element005  label="Li_element : 005"  # scripted group (container) (typed FeaturePython)
  n = 1
  ref = Li_element
FEATURE [App::DocumentObjectGroupPython] I_element003  label="I_element : 002"  # scripted group (container) (typed FeaturePython)
  n = 1
  ref = I_element
FEATURE [App::DocumentObjectGroupPython] G4_LITHIUM_IODIDE  # scripted group (container) (typed FeaturePython)
  Dunit = g/cm3
  Dvalue = 3.494
  Group = -> [Li_element005,I_element003]
  conduct = 2
  density = 1
  expand = 3
  formula = G4_LITHIUM_IODIDE
  name = G4_LITHIUM_IODIDE
  specific = 4
FEATURE [App::DocumentObjectGroupPython] Li_element006  label="Li_element : 006"  # scripted group (container) (typed FeaturePython)
  n = 2
  ref = Li_element
FEATURE [App::DocumentObjectGroupPython] O_element055  label="O_element : 029"  # scripted group (container) (typed FeaturePython)
  n = 1
  ref = O_element
FEATURE [App::DocumentObjectGroupPython] G4_LITHIUM_OXIDE  # scripted group (container) (typed FeaturePython)
  Dunit = g/cm3
  Dvalue = 2.013
  Group = -> [Li_element006,O_element055]
  conduct = 2
  density = 1
  expand = 3
  formula = G4_LITHIUM_OXIDE
  name = G4_LITHIUM_OXIDE
  specific = 4
FEATURE [App::DocumentObjectGroupPython] Li_element007  label="Li_element : 007"  # scripted group (container) (typed FeaturePython)
  n = 2
  ref = Li_element
FEATURE [App::DocumentObjectGroupPython] B_element005  label="B_element : 005"  # scripted group (container) (typed FeaturePython)
  n = 4
  ref = B_element
FEATURE [App::DocumentObjectGroupPython] O_element056  label="O_element : 7"  # scripted group (container) (typed FeaturePython)
  n = 7
  ref = O_element
FEATURE [App::DocumentObjectGroupPython] G4_LITHIUM_TETRABORATE  # scripted group (container) (typed FeaturePython)
  Dunit = g/cm3
  Dvalue = 2.44
  Group = -> [Li_element007,B_element005,O_element056]
  conduct = 2
  density = 1
  expand = 3
  formula = G4_LITHIUM_TETRABORATE
  name = G4_LITHIUM_TETRABORATE
  specific = 4
FEATURE [App::DocumentObjectGroupPython] H_element051  label="H_element : 0.105"  # scripted group (container) (typed FeaturePython)
  n = 0.105
FEATURE [App::DocumentObjectGroupPython] C_element056  label="C_element : 0.083"  # scripted group (container) (typed FeaturePython)
  n = 0.083
FEATURE [App::DocumentObjectGroupPython] N_element023  label="N_element : 0.023"  # scripted group (container) (typed FeaturePython)
  n = 0.023
FEATURE [App::DocumentObjectGroupPython] O_element057  label="O_element : 0.779"  # scripted group (container) (typed FeaturePython)
  n = 0.779
FEATURE [App::DocumentObjectGroupPython] Na_element010  label="Na_element : 0.097"  # scripted group (container) (typed FeaturePython)
  n = 0.002
FEATURE [App::DocumentObjectGroupPython] P_element006  label="P_element : 0.105"  # scripted group (container) (typed FeaturePython)
  n = 0.001
FEATURE [App::DocumentObjectGroupPython] S_element016  label="S_element : 0.017"  # scripted group (container) (typed FeaturePython)
  n = 0.002
FEATURE [App::DocumentObjectGroupPython] Cl_element014  label="Cl_element : 0.587"  # scripted group (container) (typed FeaturePython)
  n = 0.003
FEATURE [App::DocumentObjectGroupPython] K_element005  label="K_element : 0.015"  # scripted group (container) (typed FeaturePython)
  n = 0.002
FEATURE [App::DocumentObjectGroupPython] G4_LUNG_ICRP  # scripted group (container) (typed FeaturePython)
  Dunit = g/cm3
  Dvalue = 1.04
  Group = -> [H_element051,C_element056,N_element023,O_element057,Na_element010,P_element006,S_element016,Cl_element014,K_element005]
  conduct = 2
  density = 1
  expand = 3
  formula = G4_LUNG_ICRP
  name = G4_LUNG_ICRP
  specific = 4
FEATURE [App::DocumentObjectGroupPython] H_element052  label="H_element : 0.116"  # scripted group (container) (typed FeaturePython)
  n = 0.114318
FEATURE [App::DocumentObjectGroupPython] C_element057  label="C_element : 0.656"  # scripted group (container) (typed FeaturePython)
  n = 0.655824
FEATURE [App::DocumentObjectGroupPython] O_element058  label="O_element : 0.092"  # scripted group (container) (typed FeaturePython)
  n = 0.0921831
FEATURE [App::DocumentObjectGroupPython] Mg_element004  label="Mg_element : 0.135"  # scripted group (container) (typed FeaturePython)
  n = 0.134792
FEATURE [App::DocumentObjectGroupPython] Ca_element013  label="Ca_element : 0.003"  # scripted group (container) (typed FeaturePython)
  n = 0.002883
FEATURE [App::DocumentObjectGroupPython] G4_M3_WAX  # scripted group (container) (typed FeaturePython)
  Dunit = g/cm3
  Dvalue = 1.05
  Group = -> [H_element052,C_element057,O_element058,Mg_element004,Ca_element013]
  conduct = 2
  density = 1
  expand = 3
  formula = G4_M3_WAX
  name = G4_M3_WAX
  specific = 4
FEATURE [App::DocumentObjectGroupPython] Mg_element005  label="Mg_element : 1"  # scripted group (container) (typed FeaturePython)
  n = 1
  ref = Mg_element
FEATURE [App::DocumentObjectGroupPython] C_element058  label="C_element : 031"  # scripted group (container) (typed FeaturePython)
  n = 1
  ref = C_element
FEATURE [App::DocumentObjectGroupPython] O_element059  label="O_element : 030"  # scripted group (container) (typed FeaturePython)
  n = 3
  ref = O_element
FEATURE [App::DocumentObjectGroupPython] G4_MAGNESIUM_CARBONATE  # scripted group (container) (typed FeaturePython)
  Dunit = g/cm3
  Dvalue = 2.958
  Group = -> [Mg_element005,C_element058,O_element059]
  conduct = 2
  density = 1
  expand = 3
  formula = G4_MAGNESIUM_CARBONATE
  name = G4_MAGNESIUM_CARBONATE
  specific = 4
FEATURE [App::DocumentObjectGroupPython] Mg_element006  label="Mg_element : 002"  # scripted group (container) (typed FeaturePython)
  n = 1
  ref = Mg_element
FEATURE [App::DocumentObjectGroupPython] F_element013  label="F_element : 005"  # scripted group (container) (typed FeaturePython)
  n = 2
  ref = F_element
FEATURE [App::DocumentObjectGroupPython] G4_MAGNESIUM_FLUORIDE  # scripted group (container) (typed FeaturePython)
  Dunit = g/cm3
  Dvalue = 3
  Group = -> [Mg_element006,F_element013]
  conduct = 2
  density = 1
  expand = 3
  formula = G4_MAGNESIUM_FLUORIDE
  name = G4_MAGNESIUM_FLUORIDE
  specific = 4
FEATURE [App::DocumentObjectGroupPython] Mg_element007  label="Mg_element : 003"  # scripted group (container) (typed FeaturePython)
  n = 1
  ref = Mg_element
FEATURE [App::DocumentObjectGroupPython] O_element060  label="O_element : 031"  # scripted group (container) (typed FeaturePython)
  n = 1
  ref = O_element
FEATURE [App::DocumentObjectGroupPython] G4_MAGNESIUM_OXIDE  # scripted group (container) (typed FeaturePython)
  Dunit = g/cm3
  Dvalue = 3.58
  Group = -> [Mg_element007,O_element060]
  conduct = 2
  density = 1
  expand = 3
  formula = G4_MAGNESIUM_OXIDE
  name = G4_MAGNESIUM_OXIDE
  specific = 4
FEATURE [App::DocumentObjectGroupPython] Mg_element008  label="Mg_element : 004"  # scripted group (container) (typed FeaturePython)
  n = 1
  ref = Mg_element
FEATURE [App::DocumentObjectGroupPython] B_element006  label="B_element : 006"  # scripted group (container) (typed FeaturePython)
  n = 4
  ref = B_element
FEATURE [App::DocumentObjectGroupPython] O_element061  label="O_element : 032"  # scripted group (container) (typed FeaturePython)
  n = 7
  ref = O_element
FEATURE [App::DocumentObjectGroupPython] G4_MAGNESIUM_TETRABORATE  # scripted group (container) (typed FeaturePython)
  Dunit = g/cm3
  Dvalue = 2.53
  Group = -> [Mg_element008,B_element006,O_element061]
  conduct = 2
  density = 1
  expand = 3
  formula = G4_MAGNESIUM_TETRABORATE
  name = G4_MAGNESIUM_TETRABORATE
  specific = 4
FEATURE [App::DocumentObjectGroupPython] Hg_element001  label="Hg_element : 1"  # scripted group (container) (typed FeaturePython)
  n = 1
  ref = Hg_element
FEATURE [App::DocumentObjectGroupPython] I_element004  label="I_element : 2"  # scripted group (container) (typed FeaturePython)
  n = 2
  ref = I_element
FEATURE [App::DocumentObjectGroupPython] G4_MERCURIC_IODIDE  # scripted group (container) (typed FeaturePython)
  Dunit = g/cm3
  Dvalue = 6.36
  Group = -> [Hg_element001,I_element004]
  conduct = 2
  density = 1
  expand = 3
  formula = G4_MERCURIC_IODIDE
  name = G4_MERCURIC_IODIDE
  specific = 4
FEATURE [App::DocumentObjectGroupPython] C_element059  label="C_element : 032"  # scripted group (container) (typed FeaturePython)
  n = 1
  ref = C_element
FEATURE [App::DocumentObjectGroupPython] H_element053  label="H_element : 028"  # scripted group (container) (typed FeaturePython)
  n = 4
  ref = H_element
FEATURE [App::DocumentObjectGroupPython] G4_METHANE  # scripted group (container) (typed FeaturePython)
  Dunit = g/cm3
  Dvalue = 0.000667151
  Group = -> [C_element059,H_element053]
  conduct = 2
  density = 1
  expand = 3
  formula = G4_METHANE
  name = G4_METHANE
  specific = 4
FEATURE [App::DocumentObjectGroupPython] C_element060  label="C_element : 033"  # scripted group (container) (typed FeaturePython)
  n = 1
  ref = C_element
FEATURE [App::DocumentObjectGroupPython] H_element054  label="H_element : 029"  # scripted group (container) (typed FeaturePython)
  n = 4
  ref = H_element
FEATURE [App::DocumentObjectGroupPython] O_element062  label="O_element : 033"  # scripted group (container) (typed FeaturePython)
  n = 1
  ref = O_element
FEATURE [App::DocumentObjectGroupPython] G4_METHANOL  # scripted group (container) (typed FeaturePython)
  Dunit = g/cm3
  Dvalue = 0.7914
  Group = -> [C_element060,H_element054,O_element062]
  conduct = 2
  density = 1
  expand = 3
  formula = G4_METHANOL
  name = G4_METHANOL
  specific = 4
FEATURE [App::DocumentObjectGroupPython] H_element055  label="H_element : 0.134"  # scripted group (container) (typed FeaturePython)
  n = 0.13404
FEATURE [App::DocumentObjectGroupPython] C_element061  label="C_element : 0.778"  # scripted group (container) (typed FeaturePython)
  n = 0.77796
FEATURE [App::DocumentObjectGroupPython] O_element063  label="O_element : 0.035"  # scripted group (container) (typed FeaturePython)
  n = 0.03502
FEATURE [App::DocumentObjectGroupPython] Mg_element009  label="Mg_element : 0.039"  # scripted group (container) (typed FeaturePython)
  n = 0.038594
FEATURE [App::DocumentObjectGroupPython] Ti_element002  label="Ti_element : 0.014"  # scripted group (container) (typed FeaturePython)
  n = 0.014386
FEATURE [App::DocumentObjectGroupPython] G4_MIX_D_WAX  # scripted group (container) (typed FeaturePython)
  Dunit = g/cm3
  Dvalue = 0.99
  Group = -> [H_element055,C_element061,O_element063,Mg_element009,Ti_element002]
  conduct = 2
  density = 1
  expand = 3
  formula = G4_MIX_D_WAX
  name = G4_MIX_D_WAX
  specific = 4
FEATURE [App::DocumentObjectGroupPython] H_element056  label="H_element : 0.135"  # scripted group (container) (typed FeaturePython)
  n = 0.081192
FEATURE [App::DocumentObjectGroupPython] C_element062  label="C_element : 0.583"  # scripted group (container) (typed FeaturePython)
  n = 0.583442
FEATURE [App::DocumentObjectGroupPython] N_element024  label="N_element : 0.018"  # scripted group (container) (typed FeaturePython)
  n = 0.017798
FEATURE [App::DocumentObjectGroupPython] O_element064  label="O_element : 0.186"  # scripted group (container) (typed FeaturePython)
  n = 0.186381
FEATURE [App::DocumentObjectGroupPython] Mg_element010  label="Mg_element : 0.130"  # scripted group (container) (typed FeaturePython)
  n = 0.130287
FEATURE [App::DocumentObjectGroupPython] Cl_element015  label="Cl_element : 0.588"  # scripted group (container) (typed FeaturePython)
  n = 0.0009
FEATURE [App::DocumentObjectGroupPython] G4_MS20_TISSUE  # scripted group (container) (typed FeaturePython)
  Dunit = g/cm3
  Dvalue = 1
  Group = -> [H_element056,C_element062,N_element024,O_element064,Mg_element010,Cl_element015]
  conduct = 2
  density = 1
  expand = 3
  formula = G4_MS20_TISSUE
  name = G4_MS20_TISSUE
  specific = 4
FEATURE [App::DocumentObjectGroupPython] H_element057  label="H_element : 0.136"  # scripted group (container) (typed FeaturePython)
  n = 0.102
FEATURE [App::DocumentObjectGroupPython] C_element063  label="C_element : 0.143"  # scripted group (container) (typed FeaturePython)
  n = 0.143
FEATURE [App::DocumentObjectGroupPython] N_element025  label="N_element : 0.034"  # scripted group (container) (typed FeaturePython)
  n = 0.034
FEATURE [App::DocumentObjectGroupPython] O_element065  label="O_element : 0.710"  # scripted group (container) (typed FeaturePython)
  n = 0.71
FEATURE [App::DocumentObjectGroupPython] Na_element011  label="Na_element : 0.098"  # scripted group (container) (typed FeaturePython)
  n = 0.001
FEATURE [App::DocumentObjectGroupPython] P_element007  label="P_element : 0.002"  # scripted group (container) (typed FeaturePython)
  n = 0.002
FEATURE [App::DocumentObjectGroupPython] S_element017  label="S_element : 0.018"  # scripted group (container) (typed FeaturePython)
  n = 0.003
FEATURE [App::DocumentObjectGroupPython] Cl_element016  label="Cl_element : 0.589"  # scripted group (container) (typed FeaturePython)
  n = 0.001
FEATURE [App::DocumentObjectGroupPython] K_element006  label="K_element : 0.004"  # scripted group (container) (typed FeaturePython)
  n = 0.004
FEATURE [App::DocumentObjectGroupPython] G4_MUSCLE_SKELETAL_ICRP  # scripted group (container) (typed FeaturePython)
  Dunit = g/cm3
  Dvalue = 1.05
  Group = -> [H_element057,C_element063,N_element025,O_element065,Na_element011,P_element007,S_element017,Cl_element016,K_element006]
  conduct = 2
  density = 1
  expand = 3
  formula = G4_MUSCLE_SKELETAL_ICRP
  name = G4_MUSCLE_SKELETAL_ICRP
  specific = 4
FEATURE [App::DocumentObjectGroupPython] H_element058  label="H_element : 0.137"  # scripted group (container) (typed FeaturePython)
  n = 0.102102
FEATURE [App::DocumentObjectGroupPython] C_element064  label="C_element : 0.123"  # scripted group (container) (typed FeaturePython)
  n = 0.123123
FEATURE [App::DocumentObjectGroupPython] N_element026  label="N_element : 0.756"  # scripted group (container) (typed FeaturePython)
  n = 0.035035
FEATURE [App::DocumentObjectGroupPython] O_element066  label="O_element : 0.730"  # scripted group (container) (typed FeaturePython)
  n = 0.72973
FEATURE [App::DocumentObjectGroupPython] Na_element012  label="Na_element : 0.099"  # scripted group (container) (typed FeaturePython)
  n = 0.001001
FEATURE [App::DocumentObjectGroupPython] P_element008  label="P_element : 0.106"  # scripted group (container) (typed FeaturePython)
  n = 0.002002
FEATURE [App::DocumentObjectGroupPython] S_element018  label="S_element : 0.019"  # scripted group (container) (typed FeaturePython)
  n = 0.004004
FEATURE [App::DocumentObjectGroupPython] K_element007  label="K_element : 0.016"  # scripted group (container) (typed FeaturePython)
  n = 0.003003
FEATURE [App::DocumentObjectGroupPython] G4_MUSCLE_STRIATED_ICRU  # scripted group (container) (typed FeaturePython)
  Dunit = g/cm3
  Dvalue = 1.04
  Group = -> [H_element058,C_element064,N_element026,O_element066,Na_element012,P_element008,S_element018,K_element007]
  conduct = 2
  density = 1
  expand = 3
  formula = G4_MUSCLE_STRIATED_ICRU
  name = G4_MUSCLE_STRIATED_ICRU
  specific = 4
FEATURE [App::DocumentObjectGroupPython] H_element059  label="H_element : 0.098"  # scripted group (container) (typed FeaturePython)
  n = 0.0982341
FEATURE [App::DocumentObjectGroupPython] C_element065  label="C_element : 0.156"  # scripted group (container) (typed FeaturePython)
  n = 0.156214
FEATURE [App::DocumentObjectGroupPython] N_element027  label="N_element : 0.757"  # scripted group (container) (typed FeaturePython)
  n = 0.035451
FEATURE [App::DocumentObjectGroupPython] O_element067  label="O_element : 0.880"  # scripted group (container) (typed FeaturePython)
  n = 0.710101
FEATURE [App::DocumentObjectGroupPython] G4_MUSCLE_WITH_SUCROSE  # scripted group (container) (typed FeaturePython)
  Dunit = g/cm3
  Dvalue = 1.11
  Group = -> [H_element059,C_element065,N_element027,O_element067]
  conduct = 2
  density = 1
  expand = 3
  formula = G4_MUSCLE_WITH_SUCROSE
  name = G4_MUSCLE_WITH_SUCROSE
  specific = 4
FEATURE [App::DocumentObjectGroupPython] H_element060  label="H_element : 0.138"  # scripted group (container) (typed FeaturePython)
  n = 0.101969
FEATURE [App::DocumentObjectGroupPython] C_element066  label="C_element : 0.120"  # scripted group (container) (typed FeaturePython)
  n = 0.120058
FEATURE [App::DocumentObjectGroupPython] N_element028  label="N_element : 0.758"  # scripted group (container) (typed FeaturePython)
  n = 0.035451
FEATURE [App::DocumentObjectGroupPython] O_element068  label="O_element : 0.743"  # scripted group (container) (typed FeaturePython)
  n = 0.742522
FEATURE [App::DocumentObjectGroupPython] G4_MUSCLE_WITHOUT_SUCROSE  # scripted group (container) (typed FeaturePython)
  Dunit = g/cm3
  Dvalue = 1.07
  Group = -> [H_element060,C_element066,N_element028,O_element068]
  conduct = 2
  density = 1
  expand = 3
  formula = G4_MUSCLE_WITHOUT_SUCROSE
  name = G4_MUSCLE_WITHOUT_SUCROSE
  specific = 4
FEATURE [App::DocumentObjectGroupPython] C_element067  label="C_element : 10"  # scripted group (container) (typed FeaturePython)
  n = 10
  ref = C_element
FEATURE [App::DocumentObjectGroupPython] H_element061  label="H_element : 030"  # scripted group (container) (typed FeaturePython)
  n = 8
  ref = H_element
FEATURE [App::DocumentObjectGroupPython] G4_NAPHTHALENE  # scripted group (container) (typed FeaturePython)
  Dunit = g/cm3
  Dvalue = 1.145
  Group = -> [C_element067,H_element061]
  conduct = 2
  density = 1
  expand = 3
  formula = G4_NAPHTHALENE
  name = G4_NAPHTHALENE
  specific = 4
FEATURE [App::DocumentObjectGroupPython] C_element068  label="C_element : 034"  # scripted group (container) (typed FeaturePython)
  n = 6
  ref = C_element
FEATURE [App::DocumentObjectGroupPython] H_element062  label="H_element : 031"  # scripted group (container) (typed FeaturePython)
  n = 5
  ref = H_element
FEATURE [App::DocumentObjectGroupPython] N_element029  label="N_element : 012"  # scripted group (container) (typed FeaturePython)
  n = 1
  ref = N_element
FEATURE [App::DocumentObjectGroupPython] O_element069  label="O_element : 034"  # scripted group (container) (typed FeaturePython)
  n = 2
  ref = O_element
FEATURE [App::DocumentObjectGroupPython] G4_NITROBENZENE  # scripted group (container) (typed FeaturePython)
  Dunit = g/cm3
  Dvalue = 1.19867
  Group = -> [C_element068,H_element062,N_element029,O_element069]
  conduct = 2
  density = 1
  expand = 3
  formula = G4_NITROBENZENE
  name = G4_NITROBENZENE
  specific = 4
FEATURE [App::DocumentObjectGroupPython] N_element030  label="N_element : 013"  # scripted group (container) (typed FeaturePython)
  n = 2
  ref = N_element
FEATURE [App::DocumentObjectGroupPython] O_element070  label="O_element : 035"  # scripted group (container) (typed FeaturePython)
  n = 1
  ref = O_element
FEATURE [App::DocumentObjectGroupPython] G4_NITROUS_OXIDE  # scripted group (container) (typed FeaturePython)
  Dunit = g/cm3
  Dvalue = 0.00183094
  Group = -> [N_element030,O_element070]
  conduct = 2
  density = 1
  expand = 3
  formula = G4_NITROUS_OXIDE
  name = G4_NITROUS_OXIDE
  specific = 4
FEATURE [App::DocumentObjectGroupPython] H_element063  label="H_element : 0.104"  # scripted group (container) (typed FeaturePython)
  n = 0.103509
FEATURE [App::DocumentObjectGroupPython] C_element069  label="C_element : 0.648"  # scripted group (container) (typed FeaturePython)
  n = 0.648416
FEATURE [App::DocumentObjectGroupPython] N_element031  label="N_element : 0.100"  # scripted group (container) (typed FeaturePython)
  n = 0.0995361
FEATURE [App::DocumentObjectGroupPython] O_element071  label="O_element : 0.149"  # scripted group (container) (typed FeaturePython)
  n = 0.148539
FEATURE [App::DocumentObjectGroupPython] G4_NYLON_8062  label="G4_NYLON-8062"  # scripted group (container) (typed FeaturePython)
  Dunit = g/cm3
  Dvalue = 1.08
  Group = -> [H_element063,C_element069,N_element031,O_element071]
  conduct = 2
  density = 1
  expand = 3
  formula = G4_NYLON-8062
  name = G4_NYLON-8062
  specific = 4
FEATURE [App::DocumentObjectGroupPython] C_element070  label="C_element : 035"  # scripted group (container) (typed FeaturePython)
  n = 6
  ref = C_element
FEATURE [App::DocumentObjectGroupPython] H_element064  label="H_element : 11"  # scripted group (container) (typed FeaturePython)
  n = 11
  ref = H_element
FEATURE [App::DocumentObjectGroupPython] N_element032  label="N_element : 014"  # scripted group (container) (typed FeaturePython)
  n = 1
  ref = N_element
FEATURE [App::DocumentObjectGroupPython] O_element072  label="O_element : 036"  # scripted group (container) (typed FeaturePython)
  n = 1
  ref = O_element
FEATURE [App::DocumentObjectGroupPython] G4_NYLON_6_6  label="G4_NYLON-6-6"  # scripted group (container) (typed FeaturePython)
  Dunit = g/cm3
  Dvalue = 1.14
  Group = -> [C_element070,H_element064,N_element032,O_element072]
  conduct = 2
  density = 1
  expand = 3
  formula = G4_NYLON-6-6
  name = G4_NYLON-6-6
  specific = 4
FEATURE [App::DocumentObjectGroupPython] H_element065  label="H_element : 0.139"  # scripted group (container) (typed FeaturePython)
  n = 0.107062
FEATURE [App::DocumentObjectGroupPython] C_element071  label="C_element : 0.680"  # scripted group (container) (typed FeaturePython)
  n = 0.680449
FEATURE [App::DocumentObjectGroupPython] N_element033  label="N_element : 0.099"  # scripted group (container) (typed FeaturePython)
  n = 0.099189
FEATURE [App::DocumentObjectGroupPython] O_element073  label="O_element : 0.113"  # scripted group (container) (typed FeaturePython)
  n = 0.1133
FEATURE [App::DocumentObjectGroupPython] G4_NYLON_6_10  label="G4_NYLON-6-10"  # scripted group (container) (typed FeaturePython)
  Dunit = g/cm3
  Dvalue = 1.14
  Group = -> [H_element065,C_element071,N_element033,O_element073]
  conduct = 2
  density = 1
  expand = 3
  formula = G4_NYLON-6-10
  name = G4_NYLON-6-10
  specific = 4
FEATURE [App::DocumentObjectGroupPython] H_element066  label="H_element : 0.140"  # scripted group (container) (typed FeaturePython)
  n = 0.115476
FEATURE [App::DocumentObjectGroupPython] C_element072  label="C_element : 0.721"  # scripted group (container) (typed FeaturePython)
  n = 0.720818
FEATURE [App::DocumentObjectGroupPython] N_element034  label="N_element : 0.076"  # scripted group (container) (typed FeaturePython)
  n = 0.0764169
FEATURE [App::DocumentObjectGroupPython] O_element074  label="O_element : 0.087"  # scripted group (container) (typed FeaturePython)
  n = 0.0872889
FEATURE [App::DocumentObjectGroupPython] G4_NYLON_11_RILSAN  label="G4_NYLON-11_RILSAN"  # scripted group (container) (typed FeaturePython)
  Dunit = g/cm3
  Dvalue = 1.425
  Group = -> [H_element066,C_element072,N_element034,O_element074]
  conduct = 2
  density = 1
  expand = 3
  formula = G4_NYLON-11_RILSAN
  name = G4_NYLON-11_RILSAN
  specific = 4
FEATURE [App::DocumentObjectGroupPython] C_element073  label="C_element : 8"  # scripted group (container) (typed FeaturePython)
  n = 8
  ref = C_element
FEATURE [App::DocumentObjectGroupPython] H_element067  label="H_element : 18"  # scripted group (container) (typed FeaturePython)
  n = 18
  ref = H_element
FEATURE [App::DocumentObjectGroupPython] G4_OCTANE  # scripted group (container) (typed FeaturePython)
  Dunit = g/cm3
  Dvalue = 0.7026
  Group = -> [C_element073,H_element067]
  conduct = 2
  density = 1
  expand = 3
  formula = G4_OCTANE
  name = G4_OCTANE
  specific = 4
FEATURE [App::DocumentObjectGroupPython] C_element074  label="C_element : 25"  # scripted group (container) (typed FeaturePython)
  n = 25
  ref = C_element
FEATURE [App::DocumentObjectGroupPython] H_element068  label="H_element : 52"  # scripted group (container) (typed FeaturePython)
  n = 52
  ref = H_element
FEATURE [App::DocumentObjectGroupPython] G4_PARAFFIN  # scripted group (container) (typed FeaturePython)
  Dunit = g/cm3
  Dvalue = 0.93
  Group = -> [C_element074,H_element068]
  conduct = 2
  density = 1
  expand = 3
  formula = G4_PARAFFIN
  name = G4_PARAFFIN
  specific = 4
FEATURE [App::DocumentObjectGroupPython] C_element075  label="C_element : 036"  # scripted group (container) (typed FeaturePython)
  n = 5
  ref = C_element
FEATURE [App::DocumentObjectGroupPython] H_element069  label="H_element : 032"  # scripted group (container) (typed FeaturePython)
  n = 12
  ref = H_element
FEATURE [App::DocumentObjectGroupPython] G4_N_PENTANE  label="G4_N-PENTANE"  # scripted group (container) (typed FeaturePython)
  Dunit = g/cm3
  Dvalue = 0.6262
  Group = -> [C_element075,H_element069]
  conduct = 2
  density = 1
  expand = 3
  formula = G4_N-PENTANE
  name = G4_N-PENTANE
  specific = 4
FEATURE [App::DocumentObjectGroupPython] H_element070  label="H_element : 0.014"  # scripted group (container) (typed FeaturePython)
  n = 0.0141
FEATURE [App::DocumentObjectGroupPython] C_element076  label="C_element : 0.072"  # scripted group (container) (typed FeaturePython)
  n = 0.072261
FEATURE [App::DocumentObjectGroupPython] N_element035  label="N_element : 0.019"  # scripted group (container) (typed FeaturePython)
  n = 0.01932
FEATURE [App::DocumentObjectGroupPython] O_element075  label="O_element : 0.066"  # scripted group (container) (typed FeaturePython)
  n = 0.066101
FEATURE [App::DocumentObjectGroupPython] S_element019  label="S_element : 0.020"  # scripted group (container) (typed FeaturePython)
  n = 0.00189
FEATURE [App::DocumentObjectGroupPython] Br_element004  label="Br_element : 0.349"  # scripted group (container) (typed FeaturePython)
  n = 0.349103
FEATURE [App::DocumentObjectGroupPython] Ag_element001  label="Ag_element : 0.474"  # scripted group (container) (typed FeaturePython)
  n = 0.474105
FEATURE [App::DocumentObjectGroupPython] I_element005  label="I_element : 0.003"  # scripted group (container) (typed FeaturePython)
  n = 0.00312
FEATURE [App::DocumentObjectGroupPython] G4_PHOTO_EMULSION  # scripted group (container) (typed FeaturePython)
  Dunit = g/cm3
  Dvalue = 3.815
  Group = -> [H_element070,C_element076,N_element035,O_element075,S_element019,Br_element004,Ag_element001,I_element005]
  conduct = 2
  density = 1
  expand = 3
  formula = G4_PHOTO_EMULSION
  name = G4_PHOTO_EMULSION
  specific = 4
FEATURE [App::DocumentObjectGroupPython] C_element077  label="C_element : 9"  # scripted group (container) (typed FeaturePython)
  n = 9
  ref = C_element
FEATURE [App::DocumentObjectGroupPython] H_element071  label="H_element : 033"  # scripted group (container) (typed FeaturePython)
  n = 10
  ref = H_element
FEATURE [App::DocumentObjectGroupPython] G4_PLASTIC_SC_VINYLTOLUENE  # scripted group (container) (typed FeaturePython)
  Dunit = g/cm3
  Dvalue = 1.032
  Group = -> [C_element077,H_element071]
  conduct = 2
  density = 1
  expand = 3
  formula = G4_PLASTIC_SC_VINYLTOLUENE
  name = G4_PLASTIC_SC_VINYLTOLUENE
  specific = 4
FEATURE [App::DocumentObjectGroupPython] Pu_element001  label="Pu_element : 1"  # scripted group (container) (typed FeaturePython)
  n = 1
  ref = Pu_element
FEATURE [App::DocumentObjectGroupPython] O_element076  label="O_element : 037"  # scripted group (container) (typed FeaturePython)
  n = 2
  ref = O_element
FEATURE [App::DocumentObjectGroupPython] G4_PLUTONIUM_DIOXIDE  # scripted group (container) (typed FeaturePython)
  Dunit = g/cm3
  Dvalue = 11.46
  Group = -> [Pu_element001,O_element076]
  conduct = 2
  density = 1
  expand = 3
  formula = G4_PLUTONIUM_DIOXIDE
  name = G4_PLUTONIUM_DIOXIDE
  specific = 4
FEATURE [App::DocumentObjectGroupPython] C_element078  label="C_element : 037"  # scripted group (container) (typed FeaturePython)
  n = 3
  ref = C_element
FEATURE [App::DocumentObjectGroupPython] H_element072  label="H_element : 034"  # scripted group (container) (typed FeaturePython)
  n = 3
  ref = H_element
FEATURE [App::DocumentObjectGroupPython] N_element036  label="N_element : 015"  # scripted group (container) (typed FeaturePython)
  n = 1
  ref = N_element
FEATURE [App::DocumentObjectGroupPython] G4_POLYACRYLONITRILE  # scripted group (container) (typed FeaturePython)
  Dunit = g/cm3
  Dvalue = 1.17
  Group = -> [C_element078,H_element072,N_element036]
  conduct = 2
  density = 1
  expand = 3
  formula = G4_POLYACRYLONITRILE
  name = G4_POLYACRYLONITRILE
  specific = 4
FEATURE [App::DocumentObjectGroupPython] C_element079  label="C_element : 16"  # scripted group (container) (typed FeaturePython)
  n = 16
  ref = C_element
FEATURE [App::DocumentObjectGroupPython] H_element073  label="H_element : 035"  # scripted group (container) (typed FeaturePython)
  n = 14
  ref = H_element
FEATURE [App::DocumentObjectGroupPython] O_element077  label="O_element : 038"  # scripted group (container) (typed FeaturePython)
  n = 3
  ref = O_element
FEATURE [App::DocumentObjectGroupPython] G4_POLYCARBONATE  # scripted group (container) (typed FeaturePython)
  Dunit = g/cm3
  Dvalue = 1.2
  Group = -> [C_element079,H_element073,O_element077]
  conduct = 2
  density = 1
  expand = 3
  formula = G4_POLYCARBONATE
  name = G4_POLYCARBONATE
  specific = 4
FEATURE [App::DocumentObjectGroupPython] C_element080  label="C_element : 038"  # scripted group (container) (typed FeaturePython)
  n = 8
  ref = C_element
FEATURE [App::DocumentObjectGroupPython] H_element074  label="H_element : 036"  # scripted group (container) (typed FeaturePython)
  n = 7
  ref = H_element
FEATURE [App::DocumentObjectGroupPython] Cl_element017  label="Cl_element : 007"  # scripted group (container) (typed FeaturePython)
  n = 1
  ref = Cl_element
FEATURE [App::DocumentObjectGroupPython] G4_POLYCHLOROSTYRENE  # scripted group (container) (typed FeaturePython)
  Dunit = g/cm3
  Dvalue = 1.3
  Group = -> [C_element080,H_element074,Cl_element017]
  conduct = 2
  density = 1
  expand = 3
  formula = G4_POLYCHLOROSTYRENE
  name = G4_POLYCHLOROSTYRENE
  specific = 4
FEATURE [App::DocumentObjectGroupPython] C_element081  label="C_element : 039"  # scripted group (container) (typed FeaturePython)
  n = 1
  ref = C_element
FEATURE [App::DocumentObjectGroupPython] H_element075  label="H_element : 037"  # scripted group (container) (typed FeaturePython)
  n = 2
  ref = H_element
FEATURE [App::DocumentObjectGroupPython] G4_POLYETHYLENE  # scripted group (container) (typed FeaturePython)
  Dunit = g/cm3
  Dvalue = 0.94
  Group = -> [C_element081,H_element075]
  conduct = 2
  density = 1
  expand = 3
  formula = G4_POLYETHYLENE
  name = G4_POLYETHYLENE
  specific = 4
FEATURE [App::DocumentObjectGroupPython] C_element082  label="C_element : 040"  # scripted group (container) (typed FeaturePython)
  n = 10
  ref = C_element
FEATURE [App::DocumentObjectGroupPython] H_element076  label="H_element : 038"  # scripted group (container) (typed FeaturePython)
  n = 8
  ref = H_element
FEATURE [App::DocumentObjectGroupPython] O_element078  label="O_element : 039"  # scripted group (container) (typed FeaturePython)
  n = 4
  ref = O_element
FEATURE [App::DocumentObjectGroupPython] G4_MYLAR  # scripted group (container) (typed FeaturePython)
  Dunit = g/cm3
  Dvalue = 1.4
  Group = -> [C_element082,H_element076,O_element078]
  conduct = 2
  density = 1
  expand = 3
  formula = G4_MYLAR
  name = G4_MYLAR
  specific = 4
FEATURE [App::DocumentObjectGroupPython] C_element083  label="C_element : 041"  # scripted group (container) (typed FeaturePython)
  n = 5
  ref = C_element
FEATURE [App::DocumentObjectGroupPython] H_element077  label="H_element : 039"  # scripted group (container) (typed FeaturePython)
  n = 8
  ref = H_element
FEATURE [App::DocumentObjectGroupPython] O_element079  label="O_element : 040"  # scripted group (container) (typed FeaturePython)
  n = 2
  ref = O_element
FEATURE [App::DocumentObjectGroupPython] G4_PLEXIGLASS  # scripted group (container) (typed FeaturePython)
  Dunit = g/cm3
  Dvalue = 1.19
  Group = -> [C_element083,H_element077,O_element079]
  conduct = 2
  density = 1
  expand = 3
  formula = G4_PLEXIGLASS
  name = G4_PLEXIGLASS
  specific = 4
FEATURE [App::DocumentObjectGroupPython] C_element084  label="C_element : 042"  # scripted group (container) (typed FeaturePython)
  n = 1
  ref = C_element
FEATURE [App::DocumentObjectGroupPython] H_element078  label="H_element : 040"  # scripted group (container) (typed FeaturePython)
  n = 2
  ref = H_element
FEATURE [App::DocumentObjectGroupPython] O_element080  label="O_element : 041"  # scripted group (container) (typed FeaturePython)
  n = 1
  ref = O_element
FEATURE [App::DocumentObjectGroupPython] G4_POLYOXYMETHYLENE  # scripted group (container) (typed FeaturePython)
  Dunit = g/cm3
  Dvalue = 1.425
  Group = -> [C_element084,H_element078,O_element080]
  conduct = 2
  density = 1
  expand = 3
  formula = G4_POLYOXYMETHYLENE
  name = G4_POLYOXYMETHYLENE
  specific = 4
FEATURE [App::DocumentObjectGroupPython] C_element085  label="C_element : 043"  # scripted group (container) (typed FeaturePython)
  n = 2
  ref = C_element
FEATURE [App::DocumentObjectGroupPython] H_element079  label="H_element : 041"  # scripted group (container) (typed FeaturePython)
  n = 4
  ref = H_element
FEATURE [App::DocumentObjectGroupPython] G4_POLYPROPYLENE  # scripted group (container) (typed FeaturePython)
  Dunit = g/cm3
  Dvalue = 0.9
  Group = -> [C_element085,H_element079]
  conduct = 2
  density = 1
  expand = 3
  formula = G4_POLYPROPYLENE
  name = G4_POLYPROPYLENE
  specific = 4
FEATURE [App::DocumentObjectGroupPython] C_element086  label="C_element : 044"  # scripted group (container) (typed FeaturePython)
  n = 8
  ref = C_element
FEATURE [App::DocumentObjectGroupPython] H_element080  label="H_element : 042"  # scripted group (container) (typed FeaturePython)
  n = 8
  ref = H_element
FEATURE [App::DocumentObjectGroupPython] G4_POLYSTYRENE  # scripted group (container) (typed FeaturePython)
  Dunit = g/cm3
  Dvalue = 1.06
  Group = -> [C_element086,H_element080]
  conduct = 2
  density = 1
  expand = 3
  formula = G4_POLYSTYRENE
  name = G4_POLYSTYRENE
  specific = 4
FEATURE [App::DocumentObjectGroupPython] C_element087  label="C_element : 045"  # scripted group (container) (typed FeaturePython)
  n = 2
  ref = C_element
FEATURE [App::DocumentObjectGroupPython] F_element014  label="F_element : 4"  # scripted group (container) (typed FeaturePython)
  n = 4
  ref = F_element
FEATURE [App::DocumentObjectGroupPython] G4_TEFLON  # scripted group (container) (typed FeaturePython)
  Dunit = g/cm3
  Dvalue = 2.2
  Group = -> [C_element087,F_element014]
  conduct = 2
  density = 1
  expand = 3
  formula = G4_TEFLON
  name = G4_TEFLON
  specific = 4
FEATURE [App::DocumentObjectGroupPython] C_element088  label="C_element : 046"  # scripted group (container) (typed FeaturePython)
  n = 2
  ref = C_element
FEATURE [App::DocumentObjectGroupPython] F_element015  label="F_element : 006"  # scripted group (container) (typed FeaturePython)
  n = 3
  ref = F_element
FEATURE [App::DocumentObjectGroupPython] Cl_element018  label="Cl_element : 008"  # scripted group (container) (typed FeaturePython)
  n = 1
  ref = Cl_element
FEATURE [App::DocumentObjectGroupPython] G4_POLYTRIFLUOROCHLOROETHYLENE  # scripted group (container) (typed FeaturePython)
  Dunit = g/cm3
  Dvalue = 2.1
  Group = -> [C_element088,F_element015,Cl_element018]
  conduct = 2
  density = 1
  expand = 3
  formula = G4_POLYTRIFLUOROCHLOROETHYLENE
  name = G4_POLYTRIFLUOROCHLOROETHYLENE
  specific = 4
FEATURE [App::DocumentObjectGroupPython] C_element089  label="C_element : 047"  # scripted group (container) (typed FeaturePython)
  n = 4
  ref = C_element
FEATURE [App::DocumentObjectGroupPython] H_element081  label="H_element : 043"  # scripted group (container) (typed FeaturePython)
  n = 6
  ref = H_element
FEATURE [App::DocumentObjectGroupPython] O_element081  label="O_element : 042"  # scripted group (container) (typed FeaturePython)
  n = 2
  ref = O_element
FEATURE [App::DocumentObjectGroupPython] G4_POLYVINYL_ACETATE  # scripted group (container) (typed FeaturePython)
  Dunit = g/cm3
  Dvalue = 1.19
  Group = -> [C_element089,H_element081,O_element081]
  conduct = 2
  density = 1
  expand = 3
  formula = G4_POLYVINYL_ACETATE
  name = G4_POLYVINYL_ACETATE
  specific = 4
FEATURE [App::DocumentObjectGroupPython] C_element090  label="C_element : 048"  # scripted group (container) (typed FeaturePython)
  n = 2
  ref = C_element
FEATURE [App::DocumentObjectGroupPython] H_element082  label="H_element : 044"  # scripted group (container) (typed FeaturePython)
  n = 4
  ref = H_element
FEATURE [App::DocumentObjectGroupPython] O_element082  label="O_element : 043"  # scripted group (container) (typed FeaturePython)
  n = 1
  ref = O_element
FEATURE [App::DocumentObjectGroupPython] G4_POLYVINYL_ALCOHOL  # scripted group (container) (typed FeaturePython)
  Dunit = g/cm3
  Dvalue = 1.3
  Group = -> [C_element090,H_element082,O_element082]
  conduct = 2
  density = 1
  expand = 3
  formula = G4_POLYVINYL_ALCOHOL
  name = G4_POLYVINYL_ALCOHOL
  specific = 4
FEATURE [App::DocumentObjectGroupPython] C_element091  label="C_element : 049"  # scripted group (container) (typed FeaturePython)
  n = 8
  ref = C_element
FEATURE [App::DocumentObjectGroupPython] H_element083  label="H_element : 045"  # scripted group (container) (typed FeaturePython)
  n = 14
  ref = H_element
FEATURE [App::DocumentObjectGroupPython] O_element083  label="O_element : 044"  # scripted group (container) (typed FeaturePython)
  n = 2
  ref = O_element
FEATURE [App::DocumentObjectGroupPython] G4_POLYVINYL_BUTYRAL  # scripted group (container) (typed FeaturePython)
  Dunit = g/cm3
  Dvalue = 1.12
  Group = -> [C_element091,H_element083,O_element083]
  conduct = 2
  density = 1
  expand = 3
  formula = G4_POLYVINYL_BUTYRAL
  name = G4_POLYVINYL_BUTYRAL
  specific = 4
FEATURE [App::DocumentObjectGroupPython] C_element092  label="C_element : 050"  # scripted group (container) (typed FeaturePython)
  n = 2
  ref = C_element
FEATURE [App::DocumentObjectGroupPython] H_element084  label="H_element : 046"  # scripted group (container) (typed FeaturePython)
  n = 3
  ref = H_element
FEATURE [App::DocumentObjectGroupPython] Cl_element019  label="Cl_element : 009"  # scripted group (container) (typed FeaturePython)
  n = 1
  ref = Cl_element
FEATURE [App::DocumentObjectGroupPython] G4_POLYVINYL_CHLORIDE  # scripted group (container) (typed FeaturePython)
  Dunit = g/cm3
  Dvalue = 1.3
  Group = -> [C_element092,H_element084,Cl_element019]
  conduct = 2
  density = 1
  expand = 3
  formula = G4_POLYVINYL_CHLORIDE
  name = G4_POLYVINYL_CHLORIDE
  specific = 4
FEATURE [App::DocumentObjectGroupPython] C_element093  label="C_element : 051"  # scripted group (container) (typed FeaturePython)
  n = 2
  ref = C_element
FEATURE [App::DocumentObjectGroupPython] H_element085  label="H_element : 047"  # scripted group (container) (typed FeaturePython)
  n = 2
  ref = H_element
FEATURE [App::DocumentObjectGroupPython] Cl_element020  label="Cl_element : 010"  # scripted group (container) (typed FeaturePython)
  n = 2
  ref = Cl_element
FEATURE [App::DocumentObjectGroupPython] G4_POLYVINYLIDENE_CHLORIDE  # scripted group (container) (typed FeaturePython)
  Dunit = g/cm3
  Dvalue = 1.7
  Group = -> [C_element093,H_element085,Cl_element020]
  conduct = 2
  density = 1
  expand = 3
  formula = G4_POLYVINYLIDENE_CHLORIDE
  name = G4_POLYVINYLIDENE_CHLORIDE
  specific = 4
FEATURE [App::DocumentObjectGroupPython] C_element094  label="C_element : 052"  # scripted group (container) (typed FeaturePython)
  n = 2
  ref = C_element
FEATURE [App::DocumentObjectGroupPython] H_element086  label="H_element : 048"  # scripted group (container) (typed FeaturePython)
  n = 2
  ref = H_element
FEATURE [App::DocumentObjectGroupPython] F_element016  label="F_element : 007"  # scripted group (container) (typed FeaturePython)
  n = 2
  ref = F_element
FEATURE [App::DocumentObjectGroupPython] G4_POLYVINYLIDENE_FLUORIDE  # scripted group (container) (typed FeaturePython)
  Dunit = g/cm3
  Dvalue = 1.76
  Group = -> [C_element094,H_element086,F_element016]
  conduct = 2
  density = 1
  expand = 3
  formula = G4_POLYVINYLIDENE_FLUORIDE
  name = G4_POLYVINYLIDENE_FLUORIDE
  specific = 4
FEATURE [App::DocumentObjectGroupPython] C_element095  label="C_element : 053"  # scripted group (container) (typed FeaturePython)
  n = 6
  ref = C_element
FEATURE [App::DocumentObjectGroupPython] H_element087  label="H_element : 9"  # scripted group (container) (typed FeaturePython)
  n = 9
  ref = H_element
FEATURE [App::DocumentObjectGroupPython] N_element037  label="N_element : 016"  # scripted group (container) (typed FeaturePython)
  n = 1
  ref = N_element
FEATURE [App::DocumentObjectGroupPython] O_element084  label="O_element : 045"  # scripted group (container) (typed FeaturePython)
  n = 1
  ref = O_element
FEATURE [App::DocumentObjectGroupPython] G4_POLYVINYL_PYRROLIDONE  # scripted group (container) (typed FeaturePython)
  Dunit = g/cm3
  Dvalue = 1.25
  Group = -> [C_element095,H_element087,N_element037,O_element084]
  conduct = 2
  density = 1
  expand = 3
  formula = G4_POLYVINYL_PYRROLIDONE
  name = G4_POLYVINYL_PYRROLIDONE
  specific = 4
FEATURE [App::DocumentObjectGroupPython] K_element008  label="K_element : 1"  # scripted group (container) (typed FeaturePython)
  n = 1
  ref = K_element
FEATURE [App::DocumentObjectGroupPython] I_element006  label="I_element : 003"  # scripted group (container) (typed FeaturePython)
  n = 1
  ref = I_element
FEATURE [App::DocumentObjectGroupPython] G4_POTASSIUM_IODIDE  # scripted group (container) (typed FeaturePython)
  Dunit = g/cm3
  Dvalue = 3.13
  Group = -> [K_element008,I_element006]
  conduct = 2
  density = 1
  expand = 3
  formula = G4_POTASSIUM_IODIDE
  name = G4_POTASSIUM_IODIDE
  specific = 4
FEATURE [App::DocumentObjectGroupPython] K_element009  label="K_element : 2"  # scripted group (container) (typed FeaturePython)
  n = 2
  ref = K_element
FEATURE [App::DocumentObjectGroupPython] O_element085  label="O_element : 046"  # scripted group (container) (typed FeaturePython)
  n = 1
  ref = O_element
FEATURE [App::DocumentObjectGroupPython] G4_POTASSIUM_OXIDE  # scripted group (container) (typed FeaturePython)
  Dunit = g/cm3
  Dvalue = 2.32
  Group = -> [K_element009,O_element085]
  conduct = 2
  density = 1
  expand = 3
  formula = G4_POTASSIUM_OXIDE
  name = G4_POTASSIUM_OXIDE
  specific = 4
FEATURE [App::DocumentObjectGroupPython] C_element096  label="C_element : 054"  # scripted group (container) (typed FeaturePython)
  n = 3
  ref = C_element
FEATURE [App::DocumentObjectGroupPython] H_element088  label="H_element : 049"  # scripted group (container) (typed FeaturePython)
  n = 8
  ref = H_element
FEATURE [App::DocumentObjectGroupPython] G4_PROPANE  # scripted group (container) (typed FeaturePython)
  Dunit = g/cm3
  Dvalue = 0.00187939
  Group = -> [C_element096,H_element088]
  conduct = 2
  density = 1
  expand = 3
  formula = G4_PROPANE
  name = G4_PROPANE
  specific = 4
FEATURE [App::DocumentObjectGroupPython] C_element097  label="C_element : 055"  # scripted group (container) (typed FeaturePython)
  n = 3
  ref = C_element
FEATURE [App::DocumentObjectGroupPython] H_element089  label="H_element : 050"  # scripted group (container) (typed FeaturePython)
  n = 8
  ref = H_element
FEATURE [App::DocumentObjectGroupPython] G4_lPROPANE  # scripted group (container) (typed FeaturePython)
  Dunit = g/cm3
  Dvalue = 0.43
  Group = -> [C_element097,H_element089]
  conduct = 2
  density = 1
  expand = 3
  formula = G4_lPROPANE
  name = G4_lPROPANE
  specific = 4
FEATURE [App::DocumentObjectGroupPython] C_element098  label="C_element : 056"  # scripted group (container) (typed FeaturePython)
  n = 3
  ref = C_element
FEATURE [App::DocumentObjectGroupPython] H_element090  label="H_element : 051"  # scripted group (container) (typed FeaturePython)
  n = 8
  ref = H_element
FEATURE [App::DocumentObjectGroupPython] O_element086  label="O_element : 047"  # scripted group (container) (typed FeaturePython)
  n = 1
  ref = O_element
FEATURE [App::DocumentObjectGroupPython] G4_N_PROPYL_ALCOHOL  label="G4_N-PROPYL_ALCOHOL"  # scripted group (container) (typed FeaturePython)
  Dunit = g/cm3
  Dvalue = 0.8035
  Group = -> [C_element098,H_element090,O_element086]
  conduct = 2
  density = 1
  expand = 3
  formula = G4_N-PROPYL_ALCOHOL
  name = G4_N-PROPYL_ALCOHOL
  specific = 4
FEATURE [App::DocumentObjectGroupPython] C_element099  label="C_element : 057"  # scripted group (container) (typed FeaturePython)
  n = 5
  ref = C_element
FEATURE [App::DocumentObjectGroupPython] H_element091  label="H_element : 052"  # scripted group (container) (typed FeaturePython)
  n = 5
  ref = H_element
FEATURE [App::DocumentObjectGroupPython] N_element038  label="N_element : 017"  # scripted group (container) (typed FeaturePython)
  n = 1
  ref = N_element
FEATURE [App::DocumentObjectGroupPython] G4_PYRIDINE  # scripted group (container) (typed FeaturePython)
  Dunit = g/cm3
  Dvalue = 0.9819
  Group = -> [C_element099,H_element091,N_element038]
  conduct = 2
  density = 1
  expand = 3
  formula = G4_PYRIDINE
  name = G4_PYRIDINE
  specific = 4
FEATURE [App::DocumentObjectGroupPython] H_element092  label="H_element : 0.144"  # scripted group (container) (typed FeaturePython)
  n = 0.143711
FEATURE [App::DocumentObjectGroupPython] C_element100  label="C_element : 0.856"  # scripted group (container) (typed FeaturePython)
  n = 0.856289
FEATURE [App::DocumentObjectGroupPython] G4_RUBBER_BUTYL  # scripted group (container) (typed FeaturePython)
  Dunit = g/cm3
  Dvalue = 0.92
  Group = -> [H_element092,C_element100]
  conduct = 2
  density = 1
  expand = 3
  formula = G4_RUBBER_BUTYL
  name = G4_RUBBER_BUTYL
  specific = 4
FEATURE [App::DocumentObjectGroupPython] H_element093  label="H_element : 0.118"  # scripted group (container) (typed FeaturePython)
  n = 0.118371
FEATURE [App::DocumentObjectGroupPython] C_element101  label="C_element : 0.882"  # scripted group (container) (typed FeaturePython)
  n = 0.881629
FEATURE [App::DocumentObjectGroupPython] G4_RUBBER_NATURAL  # scripted group (container) (typed FeaturePython)
  Dunit = g/cm3
  Dvalue = 0.92
  Group = -> [H_element093,C_element101]
  conduct = 2
  density = 1
  expand = 3
  formula = G4_RUBBER_NATURAL
  name = G4_RUBBER_NATURAL
  specific = 4
FEATURE [App::DocumentObjectGroupPython] H_element094  label="H_element : 0.145"  # scripted group (container) (typed FeaturePython)
  n = 0.05692
FEATURE [App::DocumentObjectGroupPython] C_element102  label="C_element : 0.543"  # scripted group (container) (typed FeaturePython)
  n = 0.542646
FEATURE [App::DocumentObjectGroupPython] Cl_element021  label="Cl_element : 0.400"  # scripted group (container) (typed FeaturePython)
  n = 0.400434
FEATURE [App::DocumentObjectGroupPython] G4_RUBBER_NEOPRENE  # scripted group (container) (typed FeaturePython)
  Dunit = g/cm3
  Dvalue = 1.23
  Group = -> [H_element094,C_element102,Cl_element021]
  conduct = 2
  density = 1
  expand = 3
  formula = G4_RUBBER_NEOPRENE
  name = G4_RUBBER_NEOPRENE
  specific = 4
FEATURE [App::DocumentObjectGroupPython] Si_element006  label="Si_element : 1"  # scripted group (container) (typed FeaturePython)
  n = 1
  ref = Si_element
FEATURE [App::DocumentObjectGroupPython] O_element087  label="O_element : 048"  # scripted group (container) (typed FeaturePython)
  n = 2
  ref = O_element
FEATURE [App::DocumentObjectGroupPython] G4_SILICON_DIOXIDE  # scripted group (container) (typed FeaturePython)
  Dunit = g/cm3
  Dvalue = 2.32
  Group = -> [Si_element006,O_element087]
  conduct = 2
  density = 1
  expand = 3
  formula = G4_SILICON_DIOXIDE
  name = G4_SILICON_DIOXIDE
  specific = 4
FEATURE [App::DocumentObjectGroupPython] Ag_element002  label="Ag_element : 1"  # scripted group (container) (typed FeaturePython)
  n = 1
  ref = Ag_element
FEATURE [App::DocumentObjectGroupPython] Br_element005  label="Br_element : 003"  # scripted group (container) (typed FeaturePython)
  n = 1
  ref = Br_element
FEATURE [App::DocumentObjectGroupPython] G4_SILVER_BROMIDE  # scripted group (container) (typed FeaturePython)
  Dunit = g/cm3
  Dvalue = 6.473
  Group = -> [Ag_element002,Br_element005]
  conduct = 2
  density = 1
  expand = 3
  formula = G4_SILVER_BROMIDE
  name = G4_SILVER_BROMIDE
  specific = 4
FEATURE [App::DocumentObjectGroupPython] Ag_element003  label="Ag_element : 002"  # scripted group (container) (typed FeaturePython)
  n = 1
  ref = Ag_element
FEATURE [App::DocumentObjectGroupPython] Cl_element022  label="Cl_element : 011"  # scripted group (container) (typed FeaturePython)
  n = 1
  ref = Cl_element
FEATURE [App::DocumentObjectGroupPython] G4_SILVER_CHLORIDE  # scripted group (container) (typed FeaturePython)
  Dunit = g/cm3
  Dvalue = 5.56
  Group = -> [Ag_element003,Cl_element022]
  conduct = 2
  density = 1
  expand = 3
  formula = G4_SILVER_CHLORIDE
  name = G4_SILVER_CHLORIDE
  specific = 4
FEATURE [App::DocumentObjectGroupPython] Br_element006  label="Br_element : 0.423"  # scripted group (container) (typed FeaturePython)
  n = 0.422895
FEATURE [App::DocumentObjectGroupPython] Ag_element004  label="Ag_element : 0.574"  # scripted group (container) (typed FeaturePython)
  n = 0.573748
FEATURE [App::DocumentObjectGroupPython] I_element007  label="I_element : 0.649"  # scripted group (container) (typed FeaturePython)
  n = 0.003357
FEATURE [App::DocumentObjectGroupPython] G4_SILVER_HALIDES  # scripted group (container) (typed FeaturePython)
  Dunit = g/cm3
  Dvalue = 6.47
  Group = -> [Br_element006,Ag_element004,I_element007]
  conduct = 2
  density = 1
  expand = 3
  formula = G4_SILVER_HALIDES
  name = G4_SILVER_HALIDES
  specific = 4
FEATURE [App::DocumentObjectGroupPython] Ag_element005  label="Ag_element : 003"  # scripted group (container) (typed FeaturePython)
  n = 1
  ref = Ag_element
FEATURE [App::DocumentObjectGroupPython] I_element008  label="I_element : 004"  # scripted group (container) (typed FeaturePython)
  n = 1
  ref = I_element
FEATURE [App::DocumentObjectGroupPython] G4_SILVER_IODIDE  # scripted group (container) (typed FeaturePython)
  Dunit = g/cm3
  Dvalue = 6.01
  Group = -> [Ag_element005,I_element008]
  conduct = 2
  density = 1
  expand = 3
  formula = G4_SILVER_IODIDE
  name = G4_SILVER_IODIDE
  specific = 4
FEATURE [App::DocumentObjectGroupPython] H_element095  label="H_element : 0.100"  # scripted group (container) (typed FeaturePython)
  n = 0.1
FEATURE [App::DocumentObjectGroupPython] C_element103  label="C_element : 0.204"  # scripted group (container) (typed FeaturePython)
  n = 0.204
FEATURE [App::DocumentObjectGroupPython] N_element039  label="N_element : 0.759"  # scripted group (container) (typed FeaturePython)
  n = 0.042
FEATURE [App::DocumentObjectGroupPython] O_element088  label="O_element : 0.645"  # scripted group (container) (typed FeaturePython)
  n = 0.645
FEATURE [App::DocumentObjectGroupPython] Na_element013  label="Na_element : 0.100"  # scripted group (container) (typed FeaturePython)
  n = 0.002
FEATURE [App::DocumentObjectGroupPython] P_element009  label="P_element : 0.107"  # scripted group (container) (typed FeaturePython)
  n = 0.001
FEATURE [App::DocumentObjectGroupPython] S_element020  label="S_element : 0.021"  # scripted group (container) (typed FeaturePython)
  n = 0.002
FEATURE [App::DocumentObjectGroupPython] Cl_element023  label="Cl_element : 0.590"  # scripted group (container) (typed FeaturePython)
  n = 0.003
FEATURE [App::DocumentObjectGroupPython] K_element010  label="K_element : 0.001"  # scripted group (container) (typed FeaturePython)
  n = 0.001
FEATURE [App::DocumentObjectGroupPython] G4_SKIN_ICRP  # scripted group (container) (typed FeaturePython)
  Dunit = g/cm3
  Dvalue = 1.09
  Group = -> [H_element095,C_element103,N_element039,O_element088,Na_element013,P_element009,S_element020,Cl_element023,K_element010]
  conduct = 2
  density = 1
  expand = 3
  formula = G4_SKIN_ICRP
  name = G4_SKIN_ICRP
  specific = 4
FEATURE [App::DocumentObjectGroupPython] Na_element014  label="Na_element : 2"  # scripted group (container) (typed FeaturePython)
  n = 2
  ref = Na_element
FEATURE [App::DocumentObjectGroupPython] C_element104  label="C_element : 058"  # scripted group (container) (typed FeaturePython)
  n = 1
  ref = C_element
FEATURE [App::DocumentObjectGroupPython] O_element089  label="O_element : 049"  # scripted group (container) (typed FeaturePython)
  n = 3
  ref = O_element
FEATURE [App::DocumentObjectGroupPython] G4_SODIUM_CARBONATE  # scripted group (container) (typed FeaturePython)
  Dunit = g/cm3
  Dvalue = 2.532
  Group = -> [Na_element014,C_element104,O_element089]
  conduct = 2
  density = 1
  expand = 3
  formula = G4_SODIUM_CARBONATE
  name = G4_SODIUM_CARBONATE
  specific = 4
FEATURE [App::DocumentObjectGroupPython] Na_element015  label="Na_element : 1"  # scripted group (container) (typed FeaturePython)
  n = 1
  ref = Na_element
FEATURE [App::DocumentObjectGroupPython] I_element009  label="I_element : 005"  # scripted group (container) (typed FeaturePython)
  n = 1
  ref = I_element
FEATURE [App::DocumentObjectGroupPython] G4_SODIUM_IODIDE  # scripted group (container) (typed FeaturePython)
  Dunit = g/cm3
  Dvalue = 3.667
  Group = -> [Na_element015,I_element009]
  conduct = 2
  density = 1
  expand = 3
  formula = G4_SODIUM_IODIDE
  name = G4_SODIUM_IODIDE
  specific = 4
FEATURE [App::DocumentObjectGroupPython] Na_element016  label="Na_element : 003"  # scripted group (container) (typed FeaturePython)
  n = 2
  ref = Na_element
FEATURE [App::DocumentObjectGroupPython] O_element090  label="O_element : 050"  # scripted group (container) (typed FeaturePython)
  n = 1
  ref = O_element
FEATURE [App::DocumentObjectGroupPython] G4_SODIUM_MONOXIDE  # scripted group (container) (typed FeaturePython)
  Dunit = g/cm3
  Dvalue = 2.27
  Group = -> [Na_element016,O_element090]
  conduct = 2
  density = 1
  expand = 3
  formula = G4_SODIUM_MONOXIDE
  name = G4_SODIUM_MONOXIDE
  specific = 4
FEATURE [App::DocumentObjectGroupPython] Na_element017  label="Na_element : 004"  # scripted group (container) (typed FeaturePython)
  n = 1
  ref = Na_element
FEATURE [App::DocumentObjectGroupPython] N_element040  label="N_element : 018"  # scripted group (container) (typed FeaturePython)
  n = 1
  ref = N_element
FEATURE [App::DocumentObjectGroupPython] O_element091  label="O_element : 051"  # scripted group (container) (typed FeaturePython)
  n = 3
  ref = O_element
FEATURE [App::DocumentObjectGroupPython] G4_SODIUM_NITRATE  # scripted group (container) (typed FeaturePython)
  Dunit = g/cm3
  Dvalue = 2.261
  Group = -> [Na_element017,N_element040,O_element091]
  conduct = 2
  density = 1
  expand = 3
  formula = G4_SODIUM_NITRATE
  name = G4_SODIUM_NITRATE
  specific = 4
FEATURE [App::DocumentObjectGroupPython] C_element105  label="C_element : 059"  # scripted group (container) (typed FeaturePython)
  n = 14
  ref = C_element
FEATURE [App::DocumentObjectGroupPython] H_element096  label="H_element : 053"  # scripted group (container) (typed FeaturePython)
  n = 12
  ref = H_element
FEATURE [App::DocumentObjectGroupPython] G4_STILBENE  # scripted group (container) (typed FeaturePython)
  Dunit = g/cm3
  Dvalue = 0.9707
  Group = -> [C_element105,H_element096]
  conduct = 2
  density = 1
  expand = 3
  formula = G4_STILBENE
  name = G4_STILBENE
  specific = 4
FEATURE [App::DocumentObjectGroupPython] C_element106  label="C_element : 12"  # scripted group (container) (typed FeaturePython)
  n = 12
  ref = C_element
FEATURE [App::DocumentObjectGroupPython] H_element097  label="H_element : 22"  # scripted group (container) (typed FeaturePython)
  n = 22
  ref = H_element
FEATURE [App::DocumentObjectGroupPython] O_element092  label="O_element : 11"  # scripted group (container) (typed FeaturePython)
  n = 11
  ref = O_element
FEATURE [App::DocumentObjectGroupPython] G4_SUCROSE  # scripted group (container) (typed FeaturePython)
  Dunit = g/cm3
  Dvalue = 1.5805
  Group = -> [C_element106,H_element097,O_element092]
  conduct = 2
  density = 1
  expand = 3
  formula = G4_SUCROSE
  name = G4_SUCROSE
  specific = 4
FEATURE [App::DocumentObjectGroupPython] C_element107  label="C_element : 18"  # scripted group (container) (typed FeaturePython)
  n = 18
  ref = C_element
FEATURE [App::DocumentObjectGroupPython] H_element098  label="H_element : 054"  # scripted group (container) (typed FeaturePython)
  n = 14
  ref = H_element
FEATURE [App::DocumentObjectGroupPython] G4_TERPHENYL  # scripted group (container) (typed FeaturePython)
  Dunit = g/cm3
  Dvalue = 1.24
  Group = -> [C_element107,H_element098]
  conduct = 2
  density = 1
  expand = 3
  formula = G4_TERPHENYL
  name = G4_TERPHENYL
  specific = 4
FEATURE [App::DocumentObjectGroupPython] H_element099  label="H_element : 0.146"  # scripted group (container) (typed FeaturePython)
  n = 0.106
FEATURE [App::DocumentObjectGroupPython] C_element108  label="C_element : 0.883"  # scripted group (container) (typed FeaturePython)
  n = 0.099
FEATURE [App::DocumentObjectGroupPython] N_element041  label="N_element : 0.020"  # scripted group (container) (typed FeaturePython)
  n = 0.02
FEATURE [App::DocumentObjectGroupPython] O_element093  label="O_element : 0.766"  # scripted group (container) (typed FeaturePython)
  n = 0.766
FEATURE [App::DocumentObjectGroupPython] Na_element018  label="Na_element : 0.101"  # scripted group (container) (typed FeaturePython)
  n = 0.002
FEATURE [App::DocumentObjectGroupPython] P_element010  label="P_element : 0.108"  # scripted group (container) (typed FeaturePython)
  n = 0.001
FEATURE [App::DocumentObjectGroupPython] S_element021  label="S_element : 0.022"  # scripted group (container) (typed FeaturePython)
  n = 0.002
FEATURE [App::DocumentObjectGroupPython] Cl_element024  label="Cl_element : 0.002"  # scripted group (container) (typed FeaturePython)
  n = 0.002
FEATURE [App::DocumentObjectGroupPython] K_element011  label="K_element : 0.017"  # scripted group (container) (typed FeaturePython)
  n = 0.002
FEATURE [App::DocumentObjectGroupPython] G4_TESTIS_ICRP  # scripted group (container) (typed FeaturePython)
  Dunit = g/cm3
  Dvalue = 1.04
  Group = -> [H_element099,C_element108,N_element041,O_element093,Na_element018,P_element010,S_element021,Cl_element024,K_element011]
  conduct = 2
  density = 1
  expand = 3
  formula = G4_TESTIS_ICRP
  name = G4_TESTIS_ICRP
  specific = 4
FEATURE [App::DocumentObjectGroupPython] C_element109  label="C_element : 060"  # scripted group (container) (typed FeaturePython)
  n = 2
  ref = C_element
FEATURE [App::DocumentObjectGroupPython] Cl_element025  label="Cl_element : 012"  # scripted group (container) (typed FeaturePython)
  n = 4
  ref = Cl_element
FEATURE [App::DocumentObjectGroupPython] G4_TETRACHLOROETHYLENE  # scripted group (container) (typed FeaturePython)
  Dunit = g/cm3
  Dvalue = 1.625
  Group = -> [C_element109,Cl_element025]
  conduct = 2
  density = 1
  expand = 3
  formula = G4_TETRACHLOROETHYLENE
  name = G4_TETRACHLOROETHYLENE
  specific = 4
FEATURE [App::DocumentObjectGroupPython] Tl_element001  label="Tl_element : 1"  # scripted group (container) (typed FeaturePython)
  n = 1
  ref = Tl_element
FEATURE [App::DocumentObjectGroupPython] Cl_element026  label="Cl_element : 013"  # scripted group (container) (typed FeaturePython)
  n = 1
  ref = Cl_element
FEATURE [App::DocumentObjectGroupPython] G4_THALLIUM_CHLORIDE  # scripted group (container) (typed FeaturePython)
  Dunit = g/cm3
  Dvalue = 7.004
  Group = -> [Tl_element001,Cl_element026]
  conduct = 2
  density = 1
  expand = 3
  formula = G4_THALLIUM_CHLORIDE
  name = G4_THALLIUM_CHLORIDE
  specific = 4
FEATURE [App::DocumentObjectGroupPython] H_element100  label="H_element : 0.147"  # scripted group (container) (typed FeaturePython)
  n = 0.105
FEATURE [App::DocumentObjectGroupPython] C_element110  label="C_element : 0.256"  # scripted group (container) (typed FeaturePython)
  n = 0.256
FEATURE [App::DocumentObjectGroupPython] N_element042  label="N_element : 0.760"  # scripted group (container) (typed FeaturePython)
  n = 0.027
FEATURE [App::DocumentObjectGroupPython] O_element094  label="O_element : 0.602"  # scripted group (container) (typed FeaturePython)
  n = 0.602
FEATURE [App::DocumentObjectGroupPython] Na_element019  label="Na_element : 0.102"  # scripted group (container) (typed FeaturePython)
  n = 0.001
FEATURE [App::DocumentObjectGroupPython] P_element011  label="P_element : 0.109"  # scripted group (container) (typed FeaturePython)
  n = 0.002
FEATURE [App::DocumentObjectGroupPython] S_element022  label="S_element : 0.023"  # scripted group (container) (typed FeaturePython)
  n = 0.003
FEATURE [App::DocumentObjectGroupPython] Cl_element027  label="Cl_element : 0.591"  # scripted group (container) (typed FeaturePython)
  n = 0.002
FEATURE [App::DocumentObjectGroupPython] K_element012  label="K_element : 0.018"  # scripted group (container) (typed FeaturePython)
  n = 0.002
FEATURE [App::DocumentObjectGroupPython] G4_TISSUE_SOFT_ICRP  # scripted group (container) (typed FeaturePython)
  Dunit = g/cm3
  Dvalue = 1.03
  Group = -> [H_element100,C_element110,N_element042,O_element094,Na_element019,P_element011,S_element022,Cl_element027,K_element012]
  conduct = 2
  density = 1
  expand = 3
  formula = G4_TISSUE_SOFT_ICRP
  name = G4_TISSUE_SOFT_ICRP
  specific = 4
FEATURE [App::DocumentObjectGroupPython] H_element101  label="H_element : 0.148"  # scripted group (container) (typed FeaturePython)
  n = 0.101
FEATURE [App::DocumentObjectGroupPython] C_element111  label="C_element : 0.111"  # scripted group (container) (typed FeaturePython)
  n = 0.111
FEATURE [App::DocumentObjectGroupPython] N_element043  label="N_element : 0.026"  # scripted group (container) (typed FeaturePython)
  n = 0.026
FEATURE [App::DocumentObjectGroupPython] O_element095  label="O_element : 0.762"  # scripted group (container) (typed FeaturePython)
  n = 0.762
FEATURE [App::DocumentObjectGroupPython] G4_TISSUE_SOFT_ICRU_4  label="G4_TISSUE_SOFT_ICRU-4"  # scripted group (container) (typed FeaturePython)
  Dunit = g/cm3
  Dvalue = 1
  Group = -> [H_element101,C_element111,N_element043,O_element095]
  conduct = 2
  density = 1
  expand = 3
  formula = G4_TISSUE_SOFT_ICRU-4
  name = G4_TISSUE_SOFT_ICRU-4
  specific = 4
FEATURE [App::DocumentObjectGroupPython] H_element102  label="H_element : 0.149"  # scripted group (container) (typed FeaturePython)
  n = 0.101869
FEATURE [App::DocumentObjectGroupPython] C_element112  label="C_element : 0.456"  # scripted group (container) (typed FeaturePython)
  n = 0.456179
FEATURE [App::DocumentObjectGroupPython] N_element044  label="N_element : 0.761"  # scripted group (container) (typed FeaturePython)
  n = 0.035172
FEATURE [App::DocumentObjectGroupPython] O_element096  label="O_element : 0.407"  # scripted group (container) (typed FeaturePython)
  n = 0.40678
FEATURE [App::DocumentObjectGroupPython] G4_TISSUE_METHANE  label="G4_TISSUE-METHANE"  # scripted group (container) (typed FeaturePython)
  Dunit = g/cm3
  Dvalue = 0.00106409
  Group = -> [H_element102,C_element112,N_element044,O_element096]
  conduct = 2
  density = 1
  expand = 3
  formula = G4_TISSUE-METHANE
  name = G4_TISSUE-METHANE
  specific = 4
FEATURE [App::DocumentObjectGroupPython] H_element103  label="H_element : 0.103"  # scripted group (container) (typed FeaturePython)
  n = 0.102672
FEATURE [App::DocumentObjectGroupPython] C_element113  label="C_element : 0.569"  # scripted group (container) (typed FeaturePython)
  n = 0.56894
FEATURE [App::DocumentObjectGroupPython] N_element045  label="N_element : 0.762"  # scripted group (container) (typed FeaturePython)
  n = 0.035022
FEATURE [App::DocumentObjectGroupPython] O_element097  label="O_element : 0.293"  # scripted group (container) (typed FeaturePython)
  n = 0.293366
FEATURE [App::DocumentObjectGroupPython] G4_TISSUE_PROPANE  label="G4_TISSUE-PROPANE"  # scripted group (container) (typed FeaturePython)
  Dunit = g/cm3
  Dvalue = 0.00182628
  Group = -> [H_element103,C_element113,N_element045,O_element097]
  conduct = 2
  density = 1
  expand = 3
  formula = G4_TISSUE-PROPANE
  name = G4_TISSUE-PROPANE
  specific = 4
FEATURE [App::DocumentObjectGroupPython] Ti_element003  label="Ti_element : 1"  # scripted group (container) (typed FeaturePython)
  n = 1
  ref = Ti_element
FEATURE [App::DocumentObjectGroupPython] O_element098  label="O_element : 052"  # scripted group (container) (typed FeaturePython)
  n = 2
  ref = O_element
FEATURE [App::DocumentObjectGroupPython] G4_TITANIUM_DIOXIDE  # scripted group (container) (typed FeaturePython)
  Dunit = g/cm3
  Dvalue = 4.26
  Group = -> [Ti_element003,O_element098]
  conduct = 2
  density = 1
  expand = 3
  formula = G4_TITANIUM_DIOXIDE
  name = G4_TITANIUM_DIOXIDE
  specific = 4
FEATURE [App::DocumentObjectGroupPython] C_element114  label="C_element : 061"  # scripted group (container) (typed FeaturePython)
  n = 7
  ref = C_element
FEATURE [App::DocumentObjectGroupPython] H_element104  label="H_element : 055"  # scripted group (container) (typed FeaturePython)
  n = 8
  ref = H_element
FEATURE [App::DocumentObjectGroupPython] G4_TOLUENE  # scripted group (container) (typed FeaturePython)
  Dunit = g/cm3
  Dvalue = 0.8669
  Group = -> [C_element114,H_element104]
  conduct = 2
  density = 1
  expand = 3
  formula = G4_TOLUENE
  name = G4_TOLUENE
  specific = 4
FEATURE [App::DocumentObjectGroupPython] C_element115  label="C_element : 062"  # scripted group (container) (typed FeaturePython)
  n = 2
  ref = C_element
FEATURE [App::DocumentObjectGroupPython] H_element105  label="H_element : 056"  # scripted group (container) (typed FeaturePython)
  n = 1
  ref = H_element
FEATURE [App::DocumentObjectGroupPython] Cl_element028  label="Cl_element : 014"  # scripted group (container) (typed FeaturePython)
  n = 3
  ref = Cl_element
FEATURE [App::DocumentObjectGroupPython] G4_TRICHLOROETHYLENE  # scripted group (container) (typed FeaturePython)
  Dunit = g/cm3
  Dvalue = 1.46
  Group = -> [C_element115,H_element105,Cl_element028]
  conduct = 2
  density = 1
  expand = 3
  formula = G4_TRICHLOROETHYLENE
  name = G4_TRICHLOROETHYLENE
  specific = 4
FEATURE [App::DocumentObjectGroupPython] C_element116  label="C_element : 063"  # scripted group (container) (typed FeaturePython)
  n = 6
  ref = C_element
FEATURE [App::DocumentObjectGroupPython] H_element106  label="H_element : 15"  # scripted group (container) (typed FeaturePython)
  n = 15
  ref = H_element
FEATURE [App::DocumentObjectGroupPython] O_element099  label="O_element : 053"  # scripted group (container) (typed FeaturePython)
  n = 4
  ref = O_element
FEATURE [App::DocumentObjectGroupPython] P_element012  label="P_element : 1"  # scripted group (container) (typed FeaturePython)
  n = 1
  ref = P_element
FEATURE [App::DocumentObjectGroupPython] G4_TRIETHYL_PHOSPHATE  # scripted group (container) (typed FeaturePython)
  Dunit = g/cm3
  Dvalue = 1.07
  Group = -> [C_element116,H_element106,O_element099,P_element012]
  conduct = 2
  density = 1
  expand = 3
  formula = G4_TRIETHYL_PHOSPHATE
  name = G4_TRIETHYL_PHOSPHATE
  specific = 4
FEATURE [App::DocumentObjectGroupPython] W_element003  label="W_element : 003"  # scripted group (container) (typed FeaturePython)
  n = 1
  ref = W_element
FEATURE [App::DocumentObjectGroupPython] F_element017  label="F_element : 6"  # scripted group (container) (typed FeaturePython)
  n = 6
  ref = F_element
FEATURE [App::DocumentObjectGroupPython] G4_TUNGSTEN_HEXAFLUORIDE  # scripted group (container) (typed FeaturePython)
  Dunit = g/cm3
  Dvalue = 2.4
  Group = -> [W_element003,F_element017]
  conduct = 2
  density = 1
  expand = 3
  formula = G4_TUNGSTEN_HEXAFLUORIDE
  name = G4_TUNGSTEN_HEXAFLUORIDE
  specific = 4
FEATURE [App::DocumentObjectGroupPython] U_element001  label="U_element : 1"  # scripted group (container) (typed FeaturePython)
  n = 1
  ref = U_element
FEATURE [App::DocumentObjectGroupPython] C_element117  label="C_element : 064"  # scripted group (container) (typed FeaturePython)
  n = 2
  ref = C_element
FEATURE [App::DocumentObjectGroupPython] G4_URANIUM_DICARBIDE  # scripted group (container) (typed FeaturePython)
  Dunit = g/cm3
  Dvalue = 11.28
  Group = -> [U_element001,C_element117]
  conduct = 2
  density = 1
  expand = 3
  formula = G4_URANIUM_DICARBIDE
  name = G4_URANIUM_DICARBIDE
  specific = 4
FEATURE [App::DocumentObjectGroupPython] U_element002  label="U_element : 002"  # scripted group (container) (typed FeaturePython)
  n = 1
  ref = U_element
FEATURE [App::DocumentObjectGroupPython] C_element118  label="C_element : 065"  # scripted group (container) (typed FeaturePython)
  n = 1
  ref = C_element
FEATURE [App::DocumentObjectGroupPython] G4_URANIUM_MONOCARBIDE  # scripted group (container) (typed FeaturePython)
  Dunit = g/cm3
  Dvalue = 13.63
  Group = -> [U_element002,C_element118]
  conduct = 2
  density = 1
  expand = 3
  formula = G4_URANIUM_MONOCARBIDE
  name = G4_URANIUM_MONOCARBIDE
  specific = 4
FEATURE [App::DocumentObjectGroupPython] U_element003  label="U_element : 003"  # scripted group (container) (typed FeaturePython)
  n = 1
  ref = U_element
FEATURE [App::DocumentObjectGroupPython] O_element100  label="O_element : 054"  # scripted group (container) (typed FeaturePython)
  n = 2
  ref = O_element
FEATURE [App::DocumentObjectGroupPython] G4_URANIUM_OXIDE  # scripted group (container) (typed FeaturePython)
  Dunit = g/cm3
  Dvalue = 10.96
  Group = -> [U_element003,O_element100]
  conduct = 2
  density = 1
  expand = 3
  formula = G4_URANIUM_OXIDE
  name = G4_URANIUM_OXIDE
  specific = 4
FEATURE [App::DocumentObjectGroupPython] C_element119  label="C_element : 066"  # scripted group (container) (typed FeaturePython)
  n = 1
  ref = C_element
FEATURE [App::DocumentObjectGroupPython] H_element107  label="H_element : 057"  # scripted group (container) (typed FeaturePython)
  n = 4
  ref = H_element
FEATURE [App::DocumentObjectGroupPython] N_element046  label="N_element : 019"  # scripted group (container) (typed FeaturePython)
  n = 2
  ref = N_element
FEATURE [App::DocumentObjectGroupPython] O_element101  label="O_element : 055"  # scripted group (container) (typed FeaturePython)
  n = 1
  ref = O_element
FEATURE [App::DocumentObjectGroupPython] G4_UREA  # scripted group (container) (typed FeaturePython)
  Dunit = g/cm3
  Dvalue = 1.323
  Group = -> [C_element119,H_element107,N_element046,O_element101]
  conduct = 2
  density = 1
  expand = 3
  formula = G4_UREA
  name = G4_UREA
  specific = 4
FEATURE [App::DocumentObjectGroupPython] C_element120  label="C_element : 067"  # scripted group (container) (typed FeaturePython)
  n = 5
  ref = C_element
FEATURE [App::DocumentObjectGroupPython] H_element108  label="H_element : 058"  # scripted group (container) (typed FeaturePython)
  n = 11
  ref = H_element
FEATURE [App::DocumentObjectGroupPython] N_element047  label="N_element : 020"  # scripted group (container) (typed FeaturePython)
  n = 1
  ref = N_element
FEATURE [App::DocumentObjectGroupPython] O_element102  label="O_element : 056"  # scripted group (container) (typed FeaturePython)
  n = 2
  ref = O_element
FEATURE [App::DocumentObjectGroupPython] G4_VALINE  # scripted group (container) (typed FeaturePython)
  Dunit = g/cm3
  Dvalue = 1.23
  Group = -> [C_element120,H_element108,N_element047,O_element102]
  conduct = 2
  density = 1
  expand = 3
  formula = G4_VALINE
  name = G4_VALINE
  specific = 4
FEATURE [App::DocumentObjectGroupPython] H_element109  label="H_element : 0.009"  # scripted group (container) (typed FeaturePython)
  n = 0.009417
FEATURE [App::DocumentObjectGroupPython] C_element121  label="C_element : 0.281"  # scripted group (container) (typed FeaturePython)
  n = 0.280555
FEATURE [App::DocumentObjectGroupPython] F_element018  label="F_element : 0.710"  # scripted group (container) (typed FeaturePython)
  n = 0.710028
FEATURE [App::DocumentObjectGroupPython] G4_VITON  # scripted group (container) (typed FeaturePython)
  Dunit = g/cm3
  Dvalue = 1.8
  Group = -> [H_element109,C_element121,F_element018]
  conduct = 2
  density = 1
  expand = 3
  formula = G4_VITON
  name = G4_VITON
  specific = 4
FEATURE [App::DocumentObjectGroupPython] H_element110  label="H_element : 059"  # scripted group (container) (typed FeaturePython)
  n = 2
  ref = H_element
FEATURE [App::DocumentObjectGroupPython] O_element103  label="O_element : 057"  # scripted group (container) (typed FeaturePython)
  n = 1
  ref = O_element
FEATURE [App::DocumentObjectGroupPython] G4_WATER  # scripted group (container) (typed FeaturePython)
  Dunit = g/cm3
  Dvalue = 1
  Group = -> [H_element110,O_element103]
  conduct = 2
  density = 1
  expand = 3
  formula = G4_WATER
  name = G4_WATER
  specific = 4
FEATURE [App::DocumentObjectGroupPython] H_element111  label="H_element : 060"  # scripted group (container) (typed FeaturePython)
  n = 2
  ref = H_element
FEATURE [App::DocumentObjectGroupPython] O_element104  label="O_element : 058"  # scripted group (container) (typed FeaturePython)
  n = 1
  ref = O_element
FEATURE [App::DocumentObjectGroupPython] G4_WATER_VAPOR  # scripted group (container) (typed FeaturePython)
  Dunit = g/cm3
  Dvalue = 0.000756182
  Group = -> [H_element111,O_element104]
  conduct = 2
  density = 1
  expand = 3
  formula = G4_WATER_VAPOR
  name = G4_WATER_VAPOR
  specific = 4
FEATURE [App::DocumentObjectGroupPython] C_element122  label="C_element : 068"  # scripted group (container) (typed FeaturePython)
  n = 8
  ref = C_element
FEATURE [App::DocumentObjectGroupPython] H_element112  label="H_element : 061"  # scripted group (container) (typed FeaturePython)
  n = 10
  ref = H_element
FEATURE [App::DocumentObjectGroupPython] G4_XYLENE  # scripted group (container) (typed FeaturePython)
  Dunit = g/cm3
  Dvalue = 0.87
  Group = -> [C_element122,H_element112]
  conduct = 2
  density = 1
  expand = 3
  formula = G4_XYLENE
  name = G4_XYLENE
  specific = 4
FEATURE [App::DocumentObjectGroupPython] C_element123  label="C_element : 069"  # scripted group (container) (typed FeaturePython)
  n = 1
  ref = C_element
FEATURE [App::DocumentObjectGroupPython] G4_GRAPHITE  # scripted group (container) (typed FeaturePython)
  Dunit = g/cm3
  Dvalue = 2.21
  Group = -> [C_element123]
  conduct = 2
  density = 1
  expand = 3
  formula = G4_GRAPHITE
  name = G4_GRAPHITE
  specific = 4
FEATURE [App::DocumentObjectGroupPython] NIST  # scripted group (container) (typed FeaturePython)
  Group = -> [G4_A_150_TISSUE,G4_ACETONE,G4_ACETYLENE,G4_ADENINE,G4_ADIPOSE_TISSUE_ICRP,G4_AIR,G4_ALANINE,G4_ALUMINUM_OXIDE,G4_AMBER,G4_AMMONIA,G4_ANILINE,G4_ANTHRACENE,G4_B_100_BONE,G4_BAKELITE,G4_BARIUM_FLUORIDE,G4_BARIUM_SULFATE,G4_BENZENE,G4_BERYLLIUM_OXIDE,G4_BGO,G4_BLOOD_ICRP,G4_BONE_COMPACT_ICRU,G4_BONE_CORTICAL_ICRP,G4_BORON_CARBIDE,G4_BORON_OXIDE,G4_BRAIN_ICRP,G4_BUTANE,G4_N_BUTYL_ALCOHOL,G4_C_552,+152 more]
FEATURE [App::DocumentObjectGroupPython] H_element113  label="H_element : 062"  # scripted group (container) (typed FeaturePython)
  n = 1
  ref = H_element
FEATURE [App::DocumentObjectGroupPython] G4_H  # scripted group (container) (typed FeaturePython)
  Dunit = g/cm3
  Dvalue = 8.3748e-05
  Group = -> [H_element113]
  conduct = 2
  density = 1
  expand = 3
  formula = H
  name = G4_H
  specific = 4
FEATURE [App::DocumentObjectGroupPython] He_element001  label="He_element : 1"  # scripted group (container) (typed FeaturePython)
  n = 1
  ref = He_element
FEATURE [App::DocumentObjectGroupPython] G4_He  # scripted group (container) (typed FeaturePython)
  Dunit = g/cm3
  Dvalue = 0.000166322
  Group = -> [He_element001]
  conduct = 2
  density = 1
  expand = 3
  formula = He
  name = G4_He
  specific = 4
FEATURE [App::DocumentObjectGroupPython] Li_element008  label="Li_element : 008"  # scripted group (container) (typed FeaturePython)
  n = 1
  ref = Li_element
FEATURE [App::DocumentObjectGroupPython] G4_Li  # scripted group (container) (typed FeaturePython)
  Dunit = g/cm3
  Dvalue = 0.534
  Group = -> [Li_element008]
  conduct = 2
  density = 1
  expand = 3
  formula = Li
  name = G4_Li
  specific = 4
FEATURE [App::DocumentObjectGroupPython] Be_element002  label="Be_element : 002"  # scripted group (container) (typed FeaturePython)
  n = 1
  ref = Be_element
FEATURE [App::DocumentObjectGroupPython] G4_Be  # scripted group (container) (typed FeaturePython)
  Dunit = g/cm3
  Dvalue = 1.848
  Group = -> [Be_element002]
  conduct = 2
  density = 1
  expand = 3
  formula = Be
  name = G4_Be
  specific = 4
FEATURE [App::DocumentObjectGroupPython] B_element007  label="B_element : 007"  # scripted group (container) (typed FeaturePython)
  n = 1
  ref = B_element
FEATURE [App::DocumentObjectGroupPython] G4_B  # scripted group (container) (typed FeaturePython)
  Dunit = g/cm3
  Dvalue = 2.37
  Group = -> [B_element007]
  conduct = 2
  density = 1
  expand = 3
  formula = B
  name = G4_B
  specific = 4
FEATURE [App::DocumentObjectGroupPython] C_element124  label="C_element : 070"  # scripted group (container) (typed FeaturePython)
  n = 1
  ref = C_element
FEATURE [App::DocumentObjectGroupPython] G4_C  # scripted group (container) (typed FeaturePython)
  Dunit = g/cm3
  Dvalue = 2
  Group = -> [C_element124]
  conduct = 2
  density = 1
  expand = 3
  formula = C
  name = G4_C
  specific = 4
FEATURE [App::DocumentObjectGroupPython] N_element048  label="N_element : 021"  # scripted group (container) (typed FeaturePython)
  n = 1
  ref = N_element
FEATURE [App::DocumentObjectGroupPython] G4_N  # scripted group (container) (typed FeaturePython)
  Dunit = g/cm3
  Dvalue = 0.0011652
  Group = -> [N_element048]
  conduct = 2
  density = 1
  expand = 3
  formula = N
  name = G4_N
  specific = 4
FEATURE [App::DocumentObjectGroupPython] O_element105  label="O_element : 059"  # scripted group (container) (typed FeaturePython)
  n = 1
  ref = O_element
FEATURE [App::DocumentObjectGroupPython] G4_O  # scripted group (container) (typed FeaturePython)
  Dunit = g/cm3
  Dvalue = 0.00133151
  Group = -> [O_element105]
  conduct = 2
  density = 1
  expand = 3
  formula = O
  name = G4_O
  specific = 4
FEATURE [App::DocumentObjectGroupPython] F_element019  label="F_element : 008"  # scripted group (container) (typed FeaturePython)
  n = 1
  ref = F_element
FEATURE [App::DocumentObjectGroupPython] G4_F  # scripted group (container) (typed FeaturePython)
  Dunit = g/cm3
  Dvalue = 0.00158029
  Group = -> [F_element019]
  conduct = 2
  density = 1
  expand = 3
  formula = F
  name = G4_F
  specific = 4
FEATURE [App::DocumentObjectGroupPython] Ne_element001  label="Ne_element : 1"  # scripted group (container) (typed FeaturePython)
  n = 1
  ref = Ne_element
FEATURE [App::DocumentObjectGroupPython] G4_Ne  # scripted group (container) (typed FeaturePython)
  Dunit = g/cm3
  Dvalue = 0.000838505
  Group = -> [Ne_element001]
  conduct = 2
  density = 1
  expand = 3
  formula = Ne
  name = G4_Ne
  specific = 4
FEATURE [App::DocumentObjectGroupPython] Na_element020  label="Na_element : 005"  # scripted group (container) (typed FeaturePython)
  n = 1
  ref = Na_element
FEATURE [App::DocumentObjectGroupPython] G4_Na  # scripted group (container) (typed FeaturePython)
  Dunit = g/cm3
  Dvalue = 0.971
  Group = -> [Na_element020]
  conduct = 2
  density = 1
  expand = 3
  formula = Na
  name = G4_Na
  specific = 4
FEATURE [App::DocumentObjectGroupPython] Mg_element011  label="Mg_element : 005"  # scripted group (container) (typed FeaturePython)
  n = 1
  ref = Mg_element
FEATURE [App::DocumentObjectGroupPython] G4_Mg  # scripted group (container) (typed FeaturePython)
  Dunit = g/cm3
  Dvalue = 1.74
  Group = -> [Mg_element011]
  conduct = 2
  density = 1
  expand = 3
  formula = Mg
  name = G4_Mg
  specific = 4
FEATURE [App::DocumentObjectGroupPython] Al_element004  label="Al_element : 1"  # scripted group (container) (typed FeaturePython)
  n = 1
  ref = Al_element
FEATURE [App::DocumentObjectGroupPython] G4_Al  # scripted group (container) (typed FeaturePython)
  Dunit = g/cm3
  Dvalue = 2.699
  Group = -> [Al_element004]
  conduct = 2
  density = 1
  expand = 3
  formula = Al
  name = G4_Al
  specific = 4
FEATURE [App::DocumentObjectGroupPython] Si_element007  label="Si_element : 002"  # scripted group (container) (typed FeaturePython)
  n = 1
  ref = Si_element
FEATURE [App::DocumentObjectGroupPython] G4_Si  # scripted group (container) (typed FeaturePython)
  Dunit = g/cm3
  Dvalue = 2.33
  Group = -> [Si_element007]
  conduct = 2
  density = 1
  expand = 3
  formula = Si
  name = G4_Si
  specific = 4
FEATURE [App::DocumentObjectGroupPython] P_element013  label="P_element : 002"  # scripted group (container) (typed FeaturePython)
  n = 1
  ref = P_element
FEATURE [App::DocumentObjectGroupPython] G4_P  # scripted group (container) (typed FeaturePython)
  Dunit = g/cm3
  Dvalue = 2.2
  Group = -> [P_element013]
  conduct = 2
  density = 1
  expand = 3
  formula = P
  name = G4_P
  specific = 4
FEATURE [App::DocumentObjectGroupPython] S_element023  label="S_element : 007"  # scripted group (container) (typed FeaturePython)
  n = 1
  ref = S_element
FEATURE [App::DocumentObjectGroupPython] G4_S  # scripted group (container) (typed FeaturePython)
  Dunit = g/cm3
  Dvalue = 2
  Group = -> [S_element023]
  conduct = 2
  density = 1
  expand = 3
  formula = S
  name = G4_S
  specific = 4
FEATURE [App::DocumentObjectGroupPython] Cl_element029  label="Cl_element : 015"  # scripted group (container) (typed FeaturePython)
  n = 1
  ref = Cl_element
FEATURE [App::DocumentObjectGroupPython] G4_Cl  # scripted group (container) (typed FeaturePython)
  Dunit = g/cm3
  Dvalue = 0.00299473
  Group = -> [Cl_element029]
  conduct = 2
  density = 1
  expand = 3
  formula = Cl
  name = G4_Cl
  specific = 4
FEATURE [App::DocumentObjectGroupPython] Ar_element002  label="Ar_element : 1"  # scripted group (container) (typed FeaturePython)
  n = 1
  ref = Ar_element
FEATURE [App::DocumentObjectGroupPython] G4_Ar  # scripted group (container) (typed FeaturePython)
  Dunit = g/cm3
  Dvalue = 0.00166201
  Group = -> [Ar_element002]
  conduct = 2
  density = 1
  expand = 3
  formula = Ar
  name = G4_Ar
  specific = 4
FEATURE [App::DocumentObjectGroupPython] K_element013  label="K_element : 003"  # scripted group (container) (typed FeaturePython)
  n = 1
  ref = K_element
FEATURE [App::DocumentObjectGroupPython] G4_K  # scripted group (container) (typed FeaturePython)
  Dunit = g/cm3
  Dvalue = 0.862
  Group = -> [K_element013]
  conduct = 2
  density = 1
  expand = 3
  formula = K
  name = G4_K
  specific = 4
FEATURE [App::DocumentObjectGroupPython] Ca_element014  label="Ca_element : 007"  # scripted group (container) (typed FeaturePython)
  n = 1
  ref = Ca_element
FEATURE [App::DocumentObjectGroupPython] G4_Ca  # scripted group (container) (typed FeaturePython)
  Dunit = g/cm3
  Dvalue = 1.55
  Group = -> [Ca_element014]
  conduct = 2
  density = 1
  expand = 3
  formula = Ca
  name = G4_Ca
  specific = 4
FEATURE [App::DocumentObjectGroupPython] Sc_element001  label="Sc_element : 1"  # scripted group (container) (typed FeaturePython)
  n = 1
  ref = Sc_element
FEATURE [App::DocumentObjectGroupPython] G4_Sc  # scripted group (container) (typed FeaturePython)
  Dunit = g/cm3
  Dvalue = 2.989
  Group = -> [Sc_element001]
  conduct = 2
  density = 1
  expand = 3
  formula = Sc
  name = G4_Sc
  specific = 4
FEATURE [App::DocumentObjectGroupPython] Ti_element004  label="Ti_element : 002"  # scripted group (container) (typed FeaturePython)
  n = 1
  ref = Ti_element
FEATURE [App::DocumentObjectGroupPython] G4_Ti  # scripted group (container) (typed FeaturePython)
  Dunit = g/cm3
  Dvalue = 4.54
  Group = -> [Ti_element004]
  conduct = 2
  density = 1
  expand = 3
  formula = Ti
  name = G4_Ti
  specific = 4
FEATURE [App::DocumentObjectGroupPython] V_element001  label="V_element : 1"  # scripted group (container) (typed FeaturePython)
  n = 1
  ref = V_element
FEATURE [App::DocumentObjectGroupPython] G4_V  # scripted group (container) (typed FeaturePython)
  Dunit = g/cm3
  Dvalue = 6.11
  Group = -> [V_element001]
  conduct = 2
  density = 1
  expand = 3
  formula = V
  name = G4_V
  specific = 4
FEATURE [App::DocumentObjectGroupPython] Cr_element001  label="Cr_element : 1"  # scripted group (container) (typed FeaturePython)
  n = 1
  ref = Cr_element
FEATURE [App::DocumentObjectGroupPython] G4_Cr  # scripted group (container) (typed FeaturePython)
  Dunit = g/cm3
  Dvalue = 7.18
  Group = -> [Cr_element001]
  conduct = 2
  density = 1
  expand = 3
  formula = Cr
  name = G4_Cr
  specific = 4
FEATURE [App::DocumentObjectGroupPython] Mn_element001  label="Mn_element : 1"  # scripted group (container) (typed FeaturePython)
  n = 1
  ref = Mn_element
FEATURE [App::DocumentObjectGroupPython] G4_Mn  # scripted group (container) (typed FeaturePython)
  Dunit = g/cm3
  Dvalue = 7.44
  Group = -> [Mn_element001]
  conduct = 2
  density = 1
  expand = 3
  formula = Mn
  name = G4_Mn
  specific = 4
FEATURE [App::DocumentObjectGroupPython] Fe_element007  label="Fe_element : 004"  # scripted group (container) (typed FeaturePython)
  n = 1
  ref = Fe_element
FEATURE [App::DocumentObjectGroupPython] G4_Fe  # scripted group (container) (typed FeaturePython)
  Dunit = g/cm3
  Dvalue = 7.874
  Group = -> [Fe_element007]
  conduct = 2
  density = 1
  expand = 3
  formula = Fe
  name = G4_Fe
  specific = 4
FEATURE [App::DocumentObjectGroupPython] Co_element001  label="Co_element : 1"  # scripted group (container) (typed FeaturePython)
  n = 1
  ref = Co_element
FEATURE [App::DocumentObjectGroupPython] G4_Co  # scripted group (container) (typed FeaturePython)
  Dunit = g/cm3
  Dvalue = 8.9
  Group = -> [Co_element001]
  conduct = 2
  density = 1
  expand = 3
  formula = Co
  name = G4_Co
  specific = 4
FEATURE [App::DocumentObjectGroupPython] Ni_element001  label="Ni_element : 1"  # scripted group (container) (typed FeaturePython)
  n = 1
  ref = Ni_element
FEATURE [App::DocumentObjectGroupPython] G4_Ni  # scripted group (container) (typed FeaturePython)
  Dunit = g/cm3
  Dvalue = 8.902
  Group = -> [Ni_element001]
  conduct = 2
  density = 1
  expand = 3
  formula = Ni
  name = G4_Ni
  specific = 4
FEATURE [App::DocumentObjectGroupPython] Cu_element001  label="Cu_element : 1"  # scripted group (container) (typed FeaturePython)
  n = 1
  ref = Cu_element
FEATURE [App::DocumentObjectGroupPython] G4_Cu  # scripted group (container) (typed FeaturePython)
  Dunit = g/cm3
  Dvalue = 8.96
  Group = -> [Cu_element001]
  conduct = 2
  density = 1
  expand = 3
  formula = Cu
  name = G4_Cu
  specific = 4
FEATURE [App::DocumentObjectGroupPython] Zn_element001  label="Zn_element : 1"  # scripted group (container) (typed FeaturePython)
  n = 1
  ref = Zn_element
FEATURE [App::DocumentObjectGroupPython] G4_Zn  # scripted group (container) (typed FeaturePython)
  Dunit = g/cm3
  Dvalue = 7.133
  Group = -> [Zn_element001]
  conduct = 2
  density = 1
  expand = 3
  formula = Zn
  name = G4_Zn
  specific = 4
FEATURE [App::DocumentObjectGroupPython] Ga_element002  label="Ga_element : 002"  # scripted group (container) (typed FeaturePython)
  n = 1
  ref = Ga_element
FEATURE [App::DocumentObjectGroupPython] G4_Ga  # scripted group (container) (typed FeaturePython)
  Dunit = g/cm3
  Dvalue = 5.904
  Group = -> [Ga_element002]
  conduct = 2
  density = 1
  expand = 3
  formula = Ga
  name = G4_Ga
  specific = 4
FEATURE [App::DocumentObjectGroupPython] Ge_element002  label="Ge_element : 1"  # scripted group (container) (typed FeaturePython)
  n = 1
  ref = Ge_element
FEATURE [App::DocumentObjectGroupPython] G4_Ge  # scripted group (container) (typed FeaturePython)
  Dunit = g/cm3
  Dvalue = 5.323
  Group = -> [Ge_element002]
  conduct = 2
  density = 1
  expand = 3
  formula = Ge
  name = G4_Ge
  specific = 4
FEATURE [App::DocumentObjectGroupPython] As_element003  label="As_element : 002"  # scripted group (container) (typed FeaturePython)
  n = 1
  ref = As_element
FEATURE [App::DocumentObjectGroupPython] G4_As  # scripted group (container) (typed FeaturePython)
  Dunit = g/cm3
  Dvalue = 5.73
  Group = -> [As_element003]
  conduct = 2
  density = 1
  expand = 3
  formula = As
  name = G4_As
  specific = 4
FEATURE [App::DocumentObjectGroupPython] Se_element001  label="Se_element : 1"  # scripted group (container) (typed FeaturePython)
  n = 1
  ref = Se_element
FEATURE [App::DocumentObjectGroupPython] G4_Se  # scripted group (container) (typed FeaturePython)
  Dunit = g/cm3
  Dvalue = 4.5
  Group = -> [Se_element001]
  conduct = 2
  density = 1
  expand = 3
  formula = Se
  name = G4_Se
  specific = 4
FEATURE [App::DocumentObjectGroupPython] Br_element007  label="Br_element : 004"  # scripted group (container) (typed FeaturePython)
  n = 1
  ref = Br_element
FEATURE [App::DocumentObjectGroupPython] G4_Br  # scripted group (container) (typed FeaturePython)
  Dunit = g/cm3
  Dvalue = 0.0070721
  Group = -> [Br_element007]
  conduct = 2
  density = 1
  expand = 3
  formula = Br
  name = G4_Br
  specific = 4
FEATURE [App::DocumentObjectGroupPython] Kr_element001  label="Kr_element : 1"  # scripted group (container) (typed FeaturePython)
  n = 1
  ref = Kr_element
FEATURE [App::DocumentObjectGroupPython] G4_Kr  # scripted group (container) (typed FeaturePython)
  Dunit = g/cm3
  Dvalue = 0.00347832
  Group = -> [Kr_element001]
  conduct = 2
  density = 1
  expand = 3
  formula = Kr
  name = G4_Kr
  specific = 4
FEATURE [App::DocumentObjectGroupPython] Rb_element001  label="Rb_element : 1"  # scripted group (container) (typed FeaturePython)
  n = 1
  ref = Rb_element
FEATURE [App::DocumentObjectGroupPython] G4_Rb  # scripted group (container) (typed FeaturePython)
  Dunit = g/cm3
  Dvalue = 1.532
  Group = -> [Rb_element001]
  conduct = 2
  density = 1
  expand = 3
  formula = Rb
  name = G4_Rb
  specific = 4
FEATURE [App::DocumentObjectGroupPython] Sr_element001  label="Sr_element : 1"  # scripted group (container) (typed FeaturePython)
  n = 1
  ref = Sr_element
FEATURE [App::DocumentObjectGroupPython] G4_Sr  # scripted group (container) (typed FeaturePython)
  Dunit = g/cm3
  Dvalue = 2.54
  Group = -> [Sr_element001]
  conduct = 2
  density = 1
  expand = 3
  formula = Sr
  name = G4_Sr
  specific = 4
FEATURE [App::DocumentObjectGroupPython] Y_element001  label="Y_element : 1"  # scripted group (container) (typed FeaturePython)
  n = 1
  ref = Y_element
FEATURE [App::DocumentObjectGroupPython] G4_Y  # scripted group (container) (typed FeaturePython)
  Dunit = g/cm3
  Dvalue = 4.469
  Group = -> [Y_element001]
  conduct = 2
  density = 1
  expand = 3
  formula = Y
  name = G4_Y
  specific = 4
FEATURE [App::DocumentObjectGroupPython] Zr_element001  label="Zr_element : 1"  # scripted group (container) (typed FeaturePython)
  n = 1
  ref = Zr_element
FEATURE [App::DocumentObjectGroupPython] G4_Zr  # scripted group (container) (typed FeaturePython)
  Dunit = g/cm3
  Dvalue = 6.506
  Group = -> [Zr_element001]
  conduct = 2
  density = 1
  expand = 3
  formula = Zr
  name = G4_Zr
  specific = 4
FEATURE [App::DocumentObjectGroupPython] Nb_element001  label="Nb_element : 1"  # scripted group (container) (typed FeaturePython)
  n = 1
  ref = Nb_element
FEATURE [App::DocumentObjectGroupPython] G4_Nb  # scripted group (container) (typed FeaturePython)
  Dunit = g/cm3
  Dvalue = 8.57
  Group = -> [Nb_element001]
  conduct = 2
  density = 1
  expand = 3
  formula = Nb
  name = G4_Nb
  specific = 4
FEATURE [App::DocumentObjectGroupPython] Mo_element001  label="Mo_element : 1"  # scripted group (container) (typed FeaturePython)
  n = 1
  ref = Mo_element
FEATURE [App::DocumentObjectGroupPython] G4_Mo  # scripted group (container) (typed FeaturePython)
  Dunit = g/cm3
  Dvalue = 10.22
  Group = -> [Mo_element001]
  conduct = 2
  density = 1
  expand = 3
  formula = Mo
  name = G4_Mo
  specific = 4
FEATURE [App::DocumentObjectGroupPython] Tc_element001  label="Tc_element : 1"  # scripted group (container) (typed FeaturePython)
  n = 1
  ref = Tc_element
FEATURE [App::DocumentObjectGroupPython] G4_Tc  # scripted group (container) (typed FeaturePython)
  Dunit = g/cm3
  Dvalue = 11.5
  Group = -> [Tc_element001]
  conduct = 2
  density = 1
  expand = 3
  formula = Tc
  name = G4_Tc
  specific = 4
FEATURE [App::DocumentObjectGroupPython] Ru_element001  label="Ru_element : 1"  # scripted group (container) (typed FeaturePython)
  n = 1
  ref = Ru_element
FEATURE [App::DocumentObjectGroupPython] G4_Ru  # scripted group (container) (typed FeaturePython)
  Dunit = g/cm3
  Dvalue = 12.41
  Group = -> [Ru_element001]
  conduct = 2
  density = 1
  expand = 3
  formula = Ru
  name = G4_Ru
  specific = 4
FEATURE [App::DocumentObjectGroupPython] Rh_element001  label="Rh_element : 1"  # scripted group (container) (typed FeaturePython)
  n = 1
  ref = Rh_element
FEATURE [App::DocumentObjectGroupPython] G4_Rh  # scripted group (container) (typed FeaturePython)
  Dunit = g/cm3
  Dvalue = 12.41
  Group = -> [Rh_element001]
  conduct = 2
  density = 1
  expand = 3
  formula = Rh
  name = G4_Rh
  specific = 4
FEATURE [App::DocumentObjectGroupPython] Pd_element001  label="Pd_element : 1"  # scripted group (container) (typed FeaturePython)
  n = 1
  ref = Pd_element
FEATURE [App::DocumentObjectGroupPython] G4_Pd  # scripted group (container) (typed FeaturePython)
  Dunit = g/cm3
  Dvalue = 12.02
  Group = -> [Pd_element001]
  conduct = 2
  density = 1
  expand = 3
  formula = Pd
  name = G4_Pd
  specific = 4
FEATURE [App::DocumentObjectGroupPython] Ag_element006  label="Ag_element : 004"  # scripted group (container) (typed FeaturePython)
  n = 1
  ref = Ag_element
FEATURE [App::DocumentObjectGroupPython] G4_Ag  # scripted group (container) (typed FeaturePython)
  Dunit = g/cm3
  Dvalue = 10.5
  Group = -> [Ag_element006]
  conduct = 2
  density = 1
  expand = 3
  formula = Ag
  name = G4_Ag
  specific = 4
FEATURE [App::DocumentObjectGroupPython] Cd_element003  label="Cd_element : 003"  # scripted group (container) (typed FeaturePython)
  n = 1
  ref = Cd_element
FEATURE [App::DocumentObjectGroupPython] G4_Cd  # scripted group (container) (typed FeaturePython)
  Dunit = g/cm3
  Dvalue = 8.65
  Group = -> [Cd_element003]
  conduct = 2
  density = 1
  expand = 3
  formula = Cd
  name = G4_Cd
  specific = 4
FEATURE [App::DocumentObjectGroupPython] In_element001  label="In_element : 1"  # scripted group (container) (typed FeaturePython)
  n = 1
  ref = In_element
FEATURE [App::DocumentObjectGroupPython] G4_In  # scripted group (container) (typed FeaturePython)
  Dunit = g/cm3
  Dvalue = 7.31
  Group = -> [In_element001]
  conduct = 2
  density = 1
  expand = 3
  formula = In
  name = G4_In
  specific = 4
FEATURE [App::DocumentObjectGroupPython] Sn_element001  label="Sn_element : 1"  # scripted group (container) (typed FeaturePython)
  n = 1
  ref = Sn_element
FEATURE [App::DocumentObjectGroupPython] G4_Sn  # scripted group (container) (typed FeaturePython)
  Dunit = g/cm3
  Dvalue = 7.31
  Group = -> [Sn_element001]
  conduct = 2
  density = 1
  expand = 3
  formula = Sn
  name = G4_Sn
  specific = 4
FEATURE [App::DocumentObjectGroupPython] Sb_element001  label="Sb_element : 1"  # scripted group (container) (typed FeaturePython)
  n = 1
  ref = Sb_element
FEATURE [App::DocumentObjectGroupPython] G4_Sb  # scripted group (container) (typed FeaturePython)
  Dunit = g/cm3
  Dvalue = 6.691
  Group = -> [Sb_element001]
  conduct = 2
  density = 1
  expand = 3
  formula = Sb
  name = G4_Sb
  specific = 4
FEATURE [App::DocumentObjectGroupPython] Te_element002  label="Te_element : 002"  # scripted group (container) (typed FeaturePython)
  n = 1
  ref = Te_element
FEATURE [App::DocumentObjectGroupPython] G4_Te  # scripted group (container) (typed FeaturePython)
  Dunit = g/cm3
  Dvalue = 6.24
  Group = -> [Te_element002]
  conduct = 2
  density = 1
  expand = 3
  formula = Te
  name = G4_Te
  specific = 4
FEATURE [App::DocumentObjectGroupPython] I_element010  label="I_element : 006"  # scripted group (container) (typed FeaturePython)
  n = 1
  ref = I_element
FEATURE [App::DocumentObjectGroupPython] G4_I  # scripted group (container) (typed FeaturePython)
  Dunit = g/cm3
  Dvalue = 4.93
  Group = -> [I_element010]
  conduct = 2
  density = 1
  expand = 3
  formula = I
  name = G4_I
  specific = 4
FEATURE [App::DocumentObjectGroupPython] Xe_element001  label="Xe_element : 1"  # scripted group (container) (typed FeaturePython)
  n = 1
  ref = Xe_element
FEATURE [App::DocumentObjectGroupPython] G4_Xe  # scripted group (container) (typed FeaturePython)
  Dunit = g/cm3
  Dvalue = 0.00548536
  Group = -> [Xe_element001]
  conduct = 2
  density = 1
  expand = 3
  formula = Xe
  name = G4_Xe
  specific = 4
FEATURE [App::DocumentObjectGroupPython] Cs_element003  label="Cs_element : 003"  # scripted group (container) (typed FeaturePython)
  n = 1
  ref = Cs_element
FEATURE [App::DocumentObjectGroupPython] G4_Cs  # scripted group (container) (typed FeaturePython)
  Dunit = g/cm3
  Dvalue = 1.873
  Group = -> [Cs_element003]
  conduct = 2
  density = 1
  expand = 3
  formula = Cs
  name = G4_Cs
  specific = 4
FEATURE [App::DocumentObjectGroupPython] Ba_element003  label="Ba_element : 003"  # scripted group (container) (typed FeaturePython)
  n = 1
  ref = Ba_element
FEATURE [App::DocumentObjectGroupPython] G4_Ba  # scripted group (container) (typed FeaturePython)
  Dunit = g/cm3
  Dvalue = 3.5
  Group = -> [Ba_element003]
  conduct = 2
  density = 1
  expand = 3
  formula = Ba
  name = G4_Ba
  specific = 4
FEATURE [App::DocumentObjectGroupPython] La_element003  label="La_element : 003"  # scripted group (container) (typed FeaturePython)
  n = 1
  ref = La_element
FEATURE [App::DocumentObjectGroupPython] G4_La  # scripted group (container) (typed FeaturePython)
  Dunit = g/cm3
  Dvalue = 6.154
  Group = -> [La_element003]
  conduct = 2
  density = 1
  expand = 3
  formula = La
  name = G4_La
  specific = 4
FEATURE [App::DocumentObjectGroupPython] Ce_element002  label="Ce_element : 1"  # scripted group (container) (typed FeaturePython)
  n = 1
  ref = Ce_element
FEATURE [App::DocumentObjectGroupPython] G4_Ce  # scripted group (container) (typed FeaturePython)
  Dunit = g/cm3
  Dvalue = 6.657
  Group = -> [Ce_element002]
  conduct = 2
  density = 1
  expand = 3
  formula = Ce
  name = G4_Ce
  specific = 4
FEATURE [App::DocumentObjectGroupPython] Pr_element001  label="Pr_element : 1"  # scripted group (container) (typed FeaturePython)
  n = 1
  ref = Pr_element
FEATURE [App::DocumentObjectGroupPython] G4_Pr  # scripted group (container) (typed FeaturePython)
  Dunit = g/cm3
  Dvalue = 6.71
  Group = -> [Pr_element001]
  conduct = 2
  density = 1
  expand = 3
  formula = Pr
  name = G4_Pr
  specific = 4
FEATURE [App::DocumentObjectGroupPython] Nd_element001  label="Nd_element : 1"  # scripted group (container) (typed FeaturePython)
  n = 1
  ref = Nd_element
FEATURE [App::DocumentObjectGroupPython] G4_Nd  # scripted group (container) (typed FeaturePython)
  Dunit = g/cm3
  Dvalue = 6.9
  Group = -> [Nd_element001]
  conduct = 2
  density = 1
  expand = 3
  formula = Nd
  name = G4_Nd
  specific = 4
FEATURE [App::DocumentObjectGroupPython] Pm_element001  label="Pm_element : 1"  # scripted group (container) (typed FeaturePython)
  n = 1
  ref = Pm_element
FEATURE [App::DocumentObjectGroupPython] G4_Pm  # scripted group (container) (typed FeaturePython)
  Dunit = g/cm3
  Dvalue = 7.22
  Group = -> [Pm_element001]
  conduct = 2
  density = 1
  expand = 3
  formula = Pm
  name = G4_Pm
  specific = 4
FEATURE [App::DocumentObjectGroupPython] Sm_element001  label="Sm_element : 1"  # scripted group (container) (typed FeaturePython)
  n = 1
  ref = Sm_element
FEATURE [App::DocumentObjectGroupPython] G4_Sm  # scripted group (container) (typed FeaturePython)
  Dunit = g/cm3
  Dvalue = 7.46
  Group = -> [Sm_element001]
  conduct = 2
  density = 1
  expand = 3
  formula = Sm
  name = G4_Sm
  specific = 4
FEATURE [App::DocumentObjectGroupPython] Eu_element001  label="Eu_element : 1"  # scripted group (container) (typed FeaturePython)
  n = 1
  ref = Eu_element
FEATURE [App::DocumentObjectGroupPython] G4_Eu  # scripted group (container) (typed FeaturePython)
  Dunit = g/cm3
  Dvalue = 5.243
  Group = -> [Eu_element001]
  conduct = 2
  density = 1
  expand = 3
  formula = Eu
  name = G4_Eu
  specific = 4
FEATURE [App::DocumentObjectGroupPython] Gd_element002  label="Gd_element : 1"  # scripted group (container) (typed FeaturePython)
  n = 1
  ref = Gd_element
FEATURE [App::DocumentObjectGroupPython] G4_Gd  # scripted group (container) (typed FeaturePython)
  Dunit = g/cm3
  Dvalue = 7.9004
  Group = -> [Gd_element002]
  conduct = 2
  density = 1
  expand = 3
  formula = Gd
  name = G4_Gd
  specific = 4
FEATURE [App::DocumentObjectGroupPython] Tb_element001  label="Tb_element : 1"  # scripted group (container) (typed FeaturePython)
  n = 1
  ref = Tb_element
FEATURE [App::DocumentObjectGroupPython] G4_Tb  # scripted group (container) (typed FeaturePython)
  Dunit = g/cm3
  Dvalue = 8.229
  Group = -> [Tb_element001]
  conduct = 2
  density = 1
  expand = 3
  formula = Tb
  name = G4_Tb
  specific = 4
FEATURE [App::DocumentObjectGroupPython] Dy_element001  label="Dy_element : 1"  # scripted group (container) (typed FeaturePython)
  n = 1
  ref = Dy_element
FEATURE [App::DocumentObjectGroupPython] G4_Dy  # scripted group (container) (typed FeaturePython)
  Dunit = g/cm3
  Dvalue = 8.55
  Group = -> [Dy_element001]
  conduct = 2
  density = 1
  expand = 3
  formula = Dy
  name = G4_Dy
  specific = 4
FEATURE [App::DocumentObjectGroupPython] Ho_element001  label="Ho_element : 1"  # scripted group (container) (typed FeaturePython)
  n = 1
  ref = Ho_element
FEATURE [App::DocumentObjectGroupPython] G4_Ho  # scripted group (container) (typed FeaturePython)
  Dunit = g/cm3
  Dvalue = 8.795
  Group = -> [Ho_element001]
  conduct = 2
  density = 1
  expand = 3
  formula = Ho
  name = G4_Ho
  specific = 4
FEATURE [App::DocumentObjectGroupPython] Er_element001  label="Er_element : 1"  # scripted group (container) (typed FeaturePython)
  n = 1
  ref = Er_element
FEATURE [App::DocumentObjectGroupPython] G4_Er  # scripted group (container) (typed FeaturePython)
  Dunit = g/cm3
  Dvalue = 9.066
  Group = -> [Er_element001]
  conduct = 2
  density = 1
  expand = 3
  formula = Er
  name = G4_Er
  specific = 4
FEATURE [App::DocumentObjectGroupPython] Tm_element001  label="Tm_element : 1"  # scripted group (container) (typed FeaturePython)
  n = 1
  ref = Tm_element
FEATURE [App::DocumentObjectGroupPython] G4_Tm  # scripted group (container) (typed FeaturePython)
  Dunit = g/cm3
  Dvalue = 9.321
  Group = -> [Tm_element001]
  conduct = 2
  density = 1
  expand = 3
  formula = Tm
  name = G4_Tm
  specific = 4
FEATURE [App::DocumentObjectGroupPython] Yb_element001  label="Yb_element : 1"  # scripted group (container) (typed FeaturePython)
  n = 1
  ref = Yb_element
FEATURE [App::DocumentObjectGroupPython] G4_Yb  # scripted group (container) (typed FeaturePython)
  Dunit = g/cm3
  Dvalue = 6.73
  Group = -> [Yb_element001]
  conduct = 2
  density = 1
  expand = 3
  formula = Yb
  name = G4_Yb
  specific = 4
FEATURE [App::DocumentObjectGroupPython] Lu_element001  label="Lu_element : 1"  # scripted group (container) (typed FeaturePython)
  n = 1
  ref = Lu_element
FEATURE [App::DocumentObjectGroupPython] G4_Lu  # scripted group (container) (typed FeaturePython)
  Dunit = g/cm3
  Dvalue = 9.84
  Group = -> [Lu_element001]
  conduct = 2
  density = 1
  expand = 3
  formula = Lu
  name = G4_Lu
  specific = 4
FEATURE [App::DocumentObjectGroupPython] Hf_element001  label="Hf_element : 1"  # scripted group (container) (typed FeaturePython)
  n = 1
  ref = Hf_element
FEATURE [App::DocumentObjectGroupPython] G4_Hf  # scripted group (container) (typed FeaturePython)
  Dunit = g/cm3
  Dvalue = 13.31
  Group = -> [Hf_element001]
  conduct = 2
  density = 1
  expand = 3
  formula = Hf
  name = G4_Hf
  specific = 4
FEATURE [App::DocumentObjectGroupPython] Ta_element001  label="Ta_element : 1"  # scripted group (container) (typed FeaturePython)
  n = 1
  ref = Ta_element
FEATURE [App::DocumentObjectGroupPython] G4_Ta  # scripted group (container) (typed FeaturePython)
  Dunit = g/cm3
  Dvalue = 16.654
  Group = -> [Ta_element001]
  conduct = 2
  density = 1
  expand = 3
  formula = Ta
  name = G4_Ta
  specific = 4
FEATURE [App::DocumentObjectGroupPython] W_element004  label="W_element : 004"  # scripted group (container) (typed FeaturePython)
  n = 1
  ref = W_element
FEATURE [App::DocumentObjectGroupPython] G4_W  # scripted group (container) (typed FeaturePython)
  Dunit = g/cm3
  Dvalue = 19.3
  Group = -> [W_element004]
  conduct = 2
  density = 1
  expand = 3
  formula = W
  name = G4_W
  specific = 4
FEATURE [App::DocumentObjectGroupPython] Re_element001  label="Re_element : 1"  # scripted group (container) (typed FeaturePython)
  n = 1
  ref = Re_element
FEATURE [App::DocumentObjectGroupPython] G4_Re  # scripted group (container) (typed FeaturePython)
  Dunit = g/cm3
  Dvalue = 21.02
  Group = -> [Re_element001]
  conduct = 2
  density = 1
  expand = 3
  formula = Re
  name = G4_Re
  specific = 4
FEATURE [App::DocumentObjectGroupPython] Os_element001  label="Os_element : 1"  # scripted group (container) (typed FeaturePython)
  n = 1
  ref = Os_element
FEATURE [App::DocumentObjectGroupPython] G4_Os  # scripted group (container) (typed FeaturePython)
  Dunit = g/cm3
  Dvalue = 22.57
  Group = -> [Os_element001]
  conduct = 2
  density = 1
  expand = 3
  formula = Os
  name = G4_Os
  specific = 4
FEATURE [App::DocumentObjectGroupPython] Ir_element001  label="Ir_element : 1"  # scripted group (container) (typed FeaturePython)
  n = 1
  ref = Ir_element
FEATURE [App::DocumentObjectGroupPython] G4_Ir  # scripted group (container) (typed FeaturePython)
  Dunit = g/cm3
  Dvalue = 22.42
  Group = -> [Ir_element001]
  conduct = 2
  density = 1
  expand = 3
  formula = Ir
  name = G4_Ir
  specific = 4
FEATURE [App::DocumentObjectGroupPython] Pt_element001  label="Pt_element : 1"  # scripted group (container) (typed FeaturePython)
  n = 1
  ref = Pt_element
FEATURE [App::DocumentObjectGroupPython] G4_Pt  # scripted group (container) (typed FeaturePython)
  Dunit = g/cm3
  Dvalue = 21.45
  Group = -> [Pt_element001]
  conduct = 2
  density = 1
  expand = 3
  formula = Pt
  name = G4_Pt
  specific = 4
FEATURE [App::DocumentObjectGroupPython] Au_element001  label="Au_element : 1"  # scripted group (container) (typed FeaturePython)
  n = 1
  ref = Au_element
FEATURE [App::DocumentObjectGroupPython] G4_Au  # scripted group (container) (typed FeaturePython)
  Dunit = g/cm3
  Dvalue = 19.32
  Group = -> [Au_element001]
  conduct = 2
  density = 1
  expand = 3
  formula = Au
  name = G4_Au
  specific = 4
FEATURE [App::DocumentObjectGroupPython] Hg_element002  label="Hg_element : 002"  # scripted group (container) (typed FeaturePython)
  n = 1
  ref = Hg_element
FEATURE [App::DocumentObjectGroupPython] G4_Hg  # scripted group (container) (typed FeaturePython)
  Dunit = g/cm3
  Dvalue = 13.546
  Group = -> [Hg_element002]
  conduct = 2
  density = 1
  expand = 3
  formula = Hg
  name = G4_Hg
  specific = 4
FEATURE [App::DocumentObjectGroupPython] Tl_element002  label="Tl_element : 002"  # scripted group (container) (typed FeaturePython)
  n = 1
  ref = Tl_element
FEATURE [App::DocumentObjectGroupPython] G4_Tl  # scripted group (container) (typed FeaturePython)
  Dunit = g/cm3
  Dvalue = 11.72
  Group = -> [Tl_element002]
  conduct = 2
  density = 1
  expand = 3
  formula = Tl
  name = G4_Tl
  specific = 4
FEATURE [App::DocumentObjectGroupPython] Pb_element003  label="Pb_element : 1"  # scripted group (container) (typed FeaturePython)
  n = 1
  ref = Pb_element
FEATURE [App::DocumentObjectGroupPython] G4_Pb  # scripted group (container) (typed FeaturePython)
  Dunit = g/cm3
  Dvalue = 11.35
  Group = -> [Pb_element003]
  conduct = 2
  density = 1
  expand = 3
  formula = Pb
  name = G4_Pb
  specific = 4
FEATURE [App::DocumentObjectGroupPython] Bi_element002  label="Bi_element : 1"  # scripted group (container) (typed FeaturePython)
  n = 1
  ref = Bi_element
FEATURE [App::DocumentObjectGroupPython] G4_Bi  # scripted group (container) (typed FeaturePython)
  Dunit = g/cm3
  Dvalue = 9.747
  Group = -> [Bi_element002]
  conduct = 2
  density = 1
  expand = 3
  formula = Bi
  name = G4_Bi
  specific = 4
FEATURE [App::DocumentObjectGroupPython] Po_element001  label="Po_element : 1"  # scripted group (container) (typed FeaturePython)
  n = 1
  ref = Po_element
FEATURE [App::DocumentObjectGroupPython] G4_Po  # scripted group (container) (typed FeaturePython)
  Dunit = g/cm3
  Dvalue = 9.32
  Group = -> [Po_element001]
  conduct = 2
  density = 1
  expand = 3
  formula = Po
  name = G4_Po
  specific = 4
FEATURE [App::DocumentObjectGroupPython] At_element001  label="At_element : 1"  # scripted group (container) (typed FeaturePython)
  n = 1
  ref = At_element
FEATURE [App::DocumentObjectGroupPython] G4_At  # scripted group (container) (typed FeaturePython)
  Dunit = g/cm3
  Dvalue = 9.32
  Group = -> [At_element001]
  conduct = 2
  density = 1
  expand = 3
  formula = At
  name = G4_At
  specific = 4
FEATURE [App::DocumentObjectGroupPython] Rn_element001  label="Rn_element : 1"  # scripted group (container) (typed FeaturePython)
  n = 1
  ref = Rn_element
FEATURE [App::DocumentObjectGroupPython] G4_Rn  # scripted group (container) (typed FeaturePython)
  Dunit = g/cm3
  Dvalue = 0.00900662
  Group = -> [Rn_element001]
  conduct = 2
  density = 1
  expand = 3
  formula = Rn
  name = G4_Rn
  specific = 4
FEATURE [App::DocumentObjectGroupPython] Fr_element001  label="Fr_element : 1"  # scripted group (container) (typed FeaturePython)
  n = 1
  ref = Fr_element
FEATURE [App::DocumentObjectGroupPython] G4_Fr  # scripted group (container) (typed FeaturePython)
  Dunit = g/cm3
  Dvalue = 1
  Group = -> [Fr_element001]
  conduct = 2
  density = 1
  expand = 3
  formula = Fr
  name = G4_Fr
  specific = 4
FEATURE [App::DocumentObjectGroupPython] Ra_element001  label="Ra_element : 1"  # scripted group (container) (typed FeaturePython)
  n = 1
  ref = Ra_element
FEATURE [App::DocumentObjectGroupPython] G4_Ra  # scripted group (container) (typed FeaturePython)
  Dunit = g/cm3
  Dvalue = 5
  Group = -> [Ra_element001]
  conduct = 2
  density = 1
  expand = 3
  formula = Ra
  name = G4_Ra
  specific = 4
FEATURE [App::DocumentObjectGroupPython] Ac_element001  label="Ac_element : 1"  # scripted group (container) (typed FeaturePython)
  n = 1
  ref = Ac_element
FEATURE [App::DocumentObjectGroupPython] G4_Ac  # scripted group (container) (typed FeaturePython)
  Dunit = g/cm3
  Dvalue = 10.07
  Group = -> [Ac_element001]
  conduct = 2
  density = 1
  expand = 3
  formula = Ac
  name = G4_Ac
  specific = 4
FEATURE [App::DocumentObjectGroupPython] Th_element001  label="Th_element : 1"  # scripted group (container) (typed FeaturePython)
  n = 1
  ref = Th_element
FEATURE [App::DocumentObjectGroupPython] G4_Th  # scripted group (container) (typed FeaturePython)
  Dunit = g/cm3
  Dvalue = 11.72
  Group = -> [Th_element001]
  conduct = 2
  density = 1
  expand = 3
  formula = Th
  name = G4_Th
  specific = 4
FEATURE [App::DocumentObjectGroupPython] Pa_element001  label="Pa_element : 1"  # scripted group (container) (typed FeaturePython)
  n = 1
  ref = Pa_element
FEATURE [App::DocumentObjectGroupPython] G4_Pa  # scripted group (container) (typed FeaturePython)
  Dunit = g/cm3
  Dvalue = 15.37
  Group = -> [Pa_element001]
  conduct = 2
  density = 1
  expand = 3
  formula = Pa
  name = G4_Pa
  specific = 4
FEATURE [App::DocumentObjectGroupPython] U_element004  label="U_element : 004"  # scripted group (container) (typed FeaturePython)
  n = 1
  ref = U_element
FEATURE [App::DocumentObjectGroupPython] G4_U  # scripted group (container) (typed FeaturePython)
  Dunit = g/cm3
  Dvalue = 18.95
  Group = -> [U_element004]
  conduct = 2
  density = 1
  expand = 3
  formula = U
  name = G4_U
  specific = 4
FEATURE [App::DocumentObjectGroupPython] Np_element001  label="Np_element : 1"  # scripted group (container) (typed FeaturePython)
  n = 1
  ref = Np_element
FEATURE [App::DocumentObjectGroupPython] G4_Np  # scripted group (container) (typed FeaturePython)
  Dunit = g/cm3
  Dvalue = 20.25
  Group = -> [Np_element001]
  conduct = 2
  density = 1
  expand = 3
  formula = Np
  name = G4_Np
  specific = 4
FEATURE [App::DocumentObjectGroupPython] Pu_element002  label="Pu_element : 002"  # scripted group (container) (typed FeaturePython)
  n = 1
  ref = Pu_element
FEATURE [App::DocumentObjectGroupPython] G4_Pu  # scripted group (container) (typed FeaturePython)
  Dunit = g/cm3
  Dvalue = 19.84
  Group = -> [Pu_element002]
  conduct = 2
  density = 1
  expand = 3
  formula = Pu
  name = G4_Pu
  specific = 4
FEATURE [App::DocumentObjectGroupPython] Am_element001  label="Am_element : 1"  # scripted group (container) (typed FeaturePython)
  n = 1
  ref = Am_element
FEATURE [App::DocumentObjectGroupPython] G4_Am  # scripted group (container) (typed FeaturePython)
  Dunit = g/cm3
  Dvalue = 13.67
  Group = -> [Am_element001]
  conduct = 2
  density = 1
  expand = 3
  formula = Am
  name = G4_Am
  specific = 4
FEATURE [App::DocumentObjectGroupPython] Cm_element001  label="Cm_element : 1"  # scripted group (container) (typed FeaturePython)
  n = 1
  ref = Cm_element
FEATURE [App::DocumentObjectGroupPython] G4_Cm  # scripted group (container) (typed FeaturePython)
  Dunit = g/cm3
  Dvalue = 13.51
  Group = -> [Cm_element001]
  conduct = 2
  density = 1
  expand = 3
  formula = Cm
  name = G4_Cm
  specific = 4
FEATURE [App::DocumentObjectGroupPython] Bk_element001  label="Bk_element : 1"  # scripted group (container) (typed FeaturePython)
  n = 1
  ref = Bk_element
FEATURE [App::DocumentObjectGroupPython] G4_Bk  # scripted group (container) (typed FeaturePython)
  Dunit = g/cm3
  Dvalue = 14
  Group = -> [Bk_element001]
  conduct = 2
  density = 1
  expand = 3
  formula = Bk
  name = G4_Bk
  specific = 4
FEATURE [App::DocumentObjectGroupPython] Cf_element001  label="Cf_element : 1"  # scripted group (container) (typed FeaturePython)
  n = 1
  ref = Cf_element
FEATURE [App::DocumentObjectGroupPython] G4_Cf  # scripted group (container) (typed FeaturePython)
  Dunit = g/cm3
  Dvalue = 10
  Group = -> [Cf_element001]
  conduct = 2
  density = 1
  expand = 3
  formula = Cf
  name = G4_Cf
  specific = 4
FEATURE [App::DocumentObjectGroupPython] Element  # scripted group (container) (typed FeaturePython)
  Group = -> [G4_H,G4_He,G4_Li,G4_Be,G4_B,G4_C,G4_N,G4_O,G4_F,G4_Ne,G4_Na,G4_Mg,G4_Al,G4_Si,G4_P,G4_S,G4_Cl,G4_Ar,G4_K,G4_Ca,G4_Sc,G4_Ti,G4_V,G4_Cr,G4_Mn,G4_Fe,G4_Co,G4_Ni,G4_Cu,G4_Zn,G4_Ga,G4_Ge,G4_As,G4_Se,G4_Br,G4_Kr,G4_Rb,G4_Sr,G4_Y,G4_Zr,G4_Nb,G4_Mo,G4_Tc,G4_Ru,G4_Rh,G4_Pd,G4_Ag,G4_Cd,G4_In,G4_Sn,G4_Sb,G4_Te,G4_I,G4_Xe,G4_Cs,G4_Ba,G4_La,G4_Ce,G4_Pr,G4_Nd,G4_Pm,G4_Sm,G4_Eu,G4_Gd,G4_Tb,G4_Dy,G4_Ho,G4_Er,+30 more]
FEATURE [App::DocumentObjectGroupPython] H_element114  label="H_element : 063"  # scripted group (container) (typed FeaturePython)
  n = 2
  ref = H_element
FEATURE [App::DocumentObjectGroupPython] G4_lH2  # scripted group (container) (typed FeaturePython)
  Dunit = g/cm3
  Dvalue = 0.0708
  Group = -> [H_element114]
  conduct = 2
  density = 1
  expand = 3
  formula = G4_lH2
  name = G4_lH2
  specific = 4
FEATURE [App::DocumentObjectGroupPython] N_element049  label="N_element : 022"  # scripted group (container) (typed FeaturePython)
  n = 2
  ref = N_element
FEATURE [App::DocumentObjectGroupPython] G4_lN2  # scripted group (container) (typed FeaturePython)
  Dunit = g/cm3
  Dvalue = 0.807
  Group = -> [N_element049]
  conduct = 2
  density = 1
  expand = 3
  formula = G4_lN2
  name = G4_lN2
  specific = 4
FEATURE [App::DocumentObjectGroupPython] O_element106  label="O_element : 060"  # scripted group (container) (typed FeaturePython)
  n = 2
  ref = O_element
FEATURE [App::DocumentObjectGroupPython] G4_lO2  # scripted group (container) (typed FeaturePython)
  Dunit = g/cm3
  Dvalue = 1.141
  Group = -> [O_element106]
  conduct = 2
  density = 1
  expand = 3
  formula = G4_lO2
  name = G4_lO2
  specific = 4
FEATURE [App::DocumentObjectGroupPython] Ar  label="Ar : 1"  # scripted group (container) (typed FeaturePython)
  n = 1
  ref = Ar
FEATURE [App::DocumentObjectGroupPython] G4_lAr  # scripted group (container) (typed FeaturePython)
  Dunit = g/cm3
  Dvalue = 1.396
  Group = -> [Ar]
  conduct = 2
  density = 1
  expand = 3
  formula = G4_lAr
  name = G4_lAr
  specific = 4
FEATURE [App::DocumentObjectGroupPython] Br  label="Br : 1"  # scripted group (container) (typed FeaturePython)
  n = 1
  ref = Br
FEATURE [App::DocumentObjectGroupPython] G4_lBr  # scripted group (container) (typed FeaturePython)
  Dunit = g/cm3
  Dvalue = 3.1028
  Group = -> [Br]
  conduct = 2
  density = 1
  expand = 3
  formula = G4_lBr
  name = G4_lBr
  specific = 4
FEATURE [App::DocumentObjectGroupPython] Kr  label="Kr : 1"  # scripted group (container) (typed FeaturePython)
  n = 1
  ref = Kr
FEATURE [App::DocumentObjectGroupPython] G4_lKr  # scripted group (container) (typed FeaturePython)
  Dunit = g/cm3
  Dvalue = 2.418
  Group = -> [Kr]
  conduct = 2
  density = 1
  expand = 3
  formula = G4_lKr
  name = G4_lKr
  specific = 4
FEATURE [App::DocumentObjectGroupPython] Xe  label="Xe : 1"  # scripted group (container) (typed FeaturePython)
  n = 1
  ref = Xe
FEATURE [App::DocumentObjectGroupPython] G4_lXe  # scripted group (container) (typed FeaturePython)
  Dunit = g/cm3
  Dvalue = 2.953
  Group = -> [Xe]
  conduct = 2
  density = 1
  expand = 3
  formula = G4_lXe
  name = G4_lXe
  specific = 4
FEATURE [App::DocumentObjectGroupPython] O_element107  label="O_element : 061"  # scripted group (container) (typed FeaturePython)
  n = 4
  ref = O_element
FEATURE [App::DocumentObjectGroupPython] Pb_element004  label="Pb_element : 002"  # scripted group (container) (typed FeaturePython)
  n = 1
  ref = Pb_element
FEATURE [App::DocumentObjectGroupPython] W_element005  label="W_element : 005"  # scripted group (container) (typed FeaturePython)
  n = 1
  ref = W_element
FEATURE [App::DocumentObjectGroupPython] G4_PbWO4  # scripted group (container) (typed FeaturePython)
  Dunit = g/cm3
  Dvalue = 8.28
  Group = -> [O_element107,Pb_element004,W_element005]
  conduct = 2
  density = 1
  expand = 3
  formula = G4_PbWO4
  name = G4_PbWO4
  specific = 4
FEATURE [App::DocumentObjectGroupPython] alactic  label="alactic : 1"  # scripted group (container) (typed FeaturePython)
  n = 1
  ref = alactic
FEATURE [App::DocumentObjectGroupPython] G4_Galactic  # scripted group (container) (typed FeaturePython)
  Dunit = g/cm3
  Dvalue = 0
  Group = -> [alactic]
  conduct = 2
  density = 1
  expand = 3
  formula = G4_Galactic
  name = G4_Galactic
  specific = 4
FEATURE [App::DocumentObjectGroupPython] RAPHITE_POROUS  label="RAPHITE_POROUS : 1"  # scripted group (container) (typed FeaturePython)
  n = 1
  ref = RAPHITE_POROUS
FEATURE [App::DocumentObjectGroupPython] G4_GRAPHITE_POROUS  # scripted group (container) (typed FeaturePython)
  Dunit = g/cm3
  Dvalue = 1.7
  Group = -> [RAPHITE_POROUS]
  conduct = 2
  density = 1
  expand = 3
  formula = G4_GRAPHITE_POROUS
  name = G4_GRAPHITE_POROUS
  specific = 4
FEATURE [App::DocumentObjectGroupPython] H_element115  label="H_element : 0.150"  # scripted group (container) (typed FeaturePython)
  n = 0.080538
FEATURE [App::DocumentObjectGroupPython] C_element125  label="C_element : 0.600"  # scripted group (container) (typed FeaturePython)
  n = 0.599848
FEATURE [App::DocumentObjectGroupPython] O_element108  label="O_element : 0.320"  # scripted group (container) (typed FeaturePython)
  n = 0.319614
FEATURE [App::DocumentObjectGroupPython] G4_LUCITE  # scripted group (container) (typed FeaturePython)
  Dunit = g/cm3
  Dvalue = 1.19
  Group = -> [H_element115,C_element125,O_element108]
  conduct = 2
  density = 1
  expand = 3
  formula = G4_LUCITE
  name = G4_LUCITE
  specific = 4
FEATURE [App::DocumentObjectGroupPython] Cu_element002  label="Cu_element : 62"  # scripted group (container) (typed FeaturePython)
  n = 62
  ref = Cu_element
FEATURE [App::DocumentObjectGroupPython] Zn_element002  label="Zn_element : 35"  # scripted group (container) (typed FeaturePython)
  n = 35
  ref = Zn_element
FEATURE [App::DocumentObjectGroupPython] Pb_element005  label="Pb_element : 3"  # scripted group (container) (typed FeaturePython)
  n = 3
  ref = Pb_element
FEATURE [App::DocumentObjectGroupPython] G4_BRASS  # scripted group (container) (typed FeaturePython)
  Dunit = g/cm3
  Dvalue = 8.52
  Group = -> [Cu_element002,Zn_element002,Pb_element005]
  conduct = 2
  density = 1
  expand = 3
  formula = G4_BRASS
  name = G4_BRASS
  specific = 4
FEATURE [App::DocumentObjectGroupPython] Cu_element003  label="Cu_element : 89"  # scripted group (container) (typed FeaturePython)
  n = 89
  ref = Cu_element
FEATURE [App::DocumentObjectGroupPython] Zn_element003  label="Zn_element : 9"  # scripted group (container) (typed FeaturePython)
  n = 9
  ref = Zn_element
FEATURE [App::DocumentObjectGroupPython] Pb_element006  label="Pb_element : 2"  # scripted group (container) (typed FeaturePython)
  n = 2
  ref = Pb_element
FEATURE [App::DocumentObjectGroupPython] G4_BRONZE  # scripted group (container) (typed FeaturePython)
  Dunit = g/cm3
  Dvalue = 8.82
  Group = -> [Cu_element003,Zn_element003,Pb_element006]
  conduct = 2
  density = 1
  expand = 3
  formula = G4_BRONZE
  name = G4_BRONZE
  specific = 4
FEATURE [App::DocumentObjectGroupPython] Fe_element008  label="Fe_element : 74"  # scripted group (container) (typed FeaturePython)
  n = 74
  ref = Fe_element
FEATURE [App::DocumentObjectGroupPython] Cr_element002  label="Cr_element : 18"  # scripted group (container) (typed FeaturePython)
  n = 18
  ref = Cr_element
FEATURE [App::DocumentObjectGroupPython] Ni_element002  label="Ni_element : 8"  # scripted group (container) (typed FeaturePython)
  n = 8
  ref = Ni_element
FEATURE [App::DocumentObjectGroupPython] G4_STAINLESS_STEEL  label="G4_STAINLESS-STEEL"  # scripted group (container) (typed FeaturePython)
  Dunit = g/cm3
  Dvalue = 8
  Group = -> [Fe_element008,Cr_element002,Ni_element002]
  conduct = 2
  density = 1
  expand = 3
  formula = G4_STAINLESS-STEEL
  name = G4_STAINLESS-STEEL
  specific = 4
FEATURE [App::DocumentObjectGroupPython] H_element116  label="H_element : 064"  # scripted group (container) (typed FeaturePython)
  n = 18
  ref = H_element
FEATURE [App::DocumentObjectGroupPython] C_element126  label="C_element : 071"  # scripted group (container) (typed FeaturePython)
  n = 12
  ref = C_element
FEATURE [App::DocumentObjectGroupPython] O_element109  label="O_element : 062"  # scripted group (container) (typed FeaturePython)
  n = 7
  ref = O_element
FEATURE [App::DocumentObjectGroupPython] G4_CR39  # scripted group (container) (typed FeaturePython)
  Dunit = g/cm3
  Dvalue = 1.32
  Group = -> [H_element116,C_element126,O_element109]
  conduct = 2
  density = 1
  expand = 3
  formula = G4_CR39
  name = G4_CR39
  specific = 4
FEATURE [App::DocumentObjectGroupPython] H_element117  label="H_element : 38"  # scripted group (container) (typed FeaturePython)
  n = 38
  ref = H_element
FEATURE [App::DocumentObjectGroupPython] C_element127  label="C_element : 072"  # scripted group (container) (typed FeaturePython)
  n = 18
  ref = C_element
FEATURE [App::DocumentObjectGroupPython] O_element110  label="O_element : 063"  # scripted group (container) (typed FeaturePython)
  n = 1
  ref = O_element
FEATURE [App::DocumentObjectGroupPython] G4_OCTADECANOL  # scripted group (container) (typed FeaturePython)
  Dunit = g/cm3
  Dvalue = 0.812
  Group = -> [H_element117,C_element127,O_element110]
  conduct = 2
  density = 1
  expand = 3
  formula = G4_OCTADECANOL
  name = G4_OCTADECANOL
  specific = 4
FEATURE [App::DocumentObjectGroupPython] HEP  # scripted group (container) (typed FeaturePython)
  Group = -> [G4_lH2,G4_lN2,G4_lO2,G4_lAr,G4_lBr,G4_lKr,G4_lXe,G4_PbWO4,G4_Galactic,G4_GRAPHITE_POROUS,G4_LUCITE,G4_BRASS,G4_BRONZE,G4_STAINLESS_STEEL,G4_CR39,G4_OCTADECANOL]
FEATURE [App::DocumentObjectGroupPython] C_element128  label="C_element : 073"  # scripted group (container) (typed FeaturePython)
  n = 14
  ref = C_element
FEATURE [App::DocumentObjectGroupPython] H_element118  label="H_element : 065"  # scripted group (container) (typed FeaturePython)
  n = 10
  ref = H_element
FEATURE [App::DocumentObjectGroupPython] O_element111  label="O_element : 064"  # scripted group (container) (typed FeaturePython)
  n = 2
  ref = O_element
FEATURE [App::DocumentObjectGroupPython] N_element050  label="N_element : 023"  # scripted group (container) (typed FeaturePython)
  n = 2
  ref = N_element
FEATURE [App::DocumentObjectGroupPython] G4_KEVLAR  # scripted group (container) (typed FeaturePython)
  Dunit = g/cm3
  Dvalue = 1.44
  Group = -> [C_element128,H_element118,O_element111,N_element050]
  conduct = 2
  density = 1
  expand = 3
  formula = G4_KEVLAR
  name = G4_KEVLAR
  specific = 4
FEATURE [App::DocumentObjectGroupPython] C_element129  label="C_element : 074"  # scripted group (container) (typed FeaturePython)
  n = 10
  ref = C_element
FEATURE [App::DocumentObjectGroupPython] H_element119  label="H_element : 066"  # scripted group (container) (typed FeaturePython)
  n = 8
  ref = H_element
FEATURE [App::DocumentObjectGroupPython] O_element112  label="O_element : 065"  # scripted group (container) (typed FeaturePython)
  n = 4
  ref = O_element
FEATURE [App::DocumentObjectGroupPython] G4_DACRON  # scripted group (container) (typed FeaturePython)
  Dunit = g/cm3
  Dvalue = 1.4
  Group = -> [C_element129,H_element119,O_element112]
  conduct = 2
  density = 1
  expand = 3
  formula = G4_DACRON
  name = G4_DACRON
  specific = 4
FEATURE [App::DocumentObjectGroupPython] C_element130  label="C_element : 075"  # scripted group (container) (typed FeaturePython)
  n = 4
  ref = C_element
FEATURE [App::DocumentObjectGroupPython] H_element120  label="H_element : 067"  # scripted group (container) (typed FeaturePython)
  n = 5
  ref = H_element
FEATURE [App::DocumentObjectGroupPython] Cl_element030  label="Cl_element : 016"  # scripted group (container) (typed FeaturePython)
  n = 1
  ref = Cl_element
FEATURE [App::DocumentObjectGroupPython] G4_NEOPRENE  # scripted group (container) (typed FeaturePython)
  Dunit = g/cm3
  Dvalue = 1.23
  Group = -> [C_element130,H_element120,Cl_element030]
  conduct = 2
  density = 1
  expand = 3
  formula = G4_NEOPRENE
  name = G4_NEOPRENE
  specific = 4
FEATURE [App::DocumentObjectGroupPython] Space  # scripted group (container) (typed FeaturePython)
  Group = -> [G4_KEVLAR,G4_DACRON,G4_NEOPRENE]
FEATURE [App::DocumentObjectGroupPython] H_element121  label="H_element : 068"  # scripted group (container) (typed FeaturePython)
  n = 5
  ref = H_element
FEATURE [App::DocumentObjectGroupPython] C_element131  label="C_element : 076"  # scripted group (container) (typed FeaturePython)
  n = 4
  ref = C_element
FEATURE [App::DocumentObjectGroupPython] N_element051  label="N_element : 3"  # scripted group (container) (typed FeaturePython)
  n = 3
  ref = N_element
FEATURE [App::DocumentObjectGroupPython] O_element113  label="O_element : 066"  # scripted group (container) (typed FeaturePython)
  n = 1
  ref = O_element
FEATURE [App::DocumentObjectGroupPython] G4_CYTOSINE  # scripted group (container) (typed FeaturePython)
  Dunit = g/cm3
  Dvalue = 1.55
  Group = -> [H_element121,C_element131,N_element051,O_element113]
  conduct = 2
  density = 1
  expand = 3
  formula = G4_CYTOSINE
  name = G4_CYTOSINE
  specific = 4
FEATURE [App::DocumentObjectGroupPython] H_element122  label="H_element : 069"  # scripted group (container) (typed FeaturePython)
  n = 6
  ref = H_element
FEATURE [App::DocumentObjectGroupPython] C_element132  label="C_element : 077"  # scripted group (container) (typed FeaturePython)
  n = 5
  ref = C_element
FEATURE [App::DocumentObjectGroupPython] N_element052  label="N_element : 024"  # scripted group (container) (typed FeaturePython)
  n = 2
  ref = N_element
FEATURE [App::DocumentObjectGroupPython] O_element114  label="O_element : 067"  # scripted group (container) (typed FeaturePython)
  n = 2
  ref = O_element
FEATURE [App::DocumentObjectGroupPython] G4_THYMINE  # scripted group (container) (typed FeaturePython)
  Dunit = g/cm3
  Dvalue = 1.23
  Group = -> [H_element122,C_element132,N_element052,O_element114]
  conduct = 2
  density = 1
  expand = 3
  formula = G4_THYMINE
  name = G4_THYMINE
  specific = 4
FEATURE [App::DocumentObjectGroupPython] H_element123  label="H_element : 070"  # scripted group (container) (typed FeaturePython)
  n = 4
  ref = H_element
FEATURE [App::DocumentObjectGroupPython] C_element133  label="C_element : 078"  # scripted group (container) (typed FeaturePython)
  n = 4
  ref = C_element
FEATURE [App::DocumentObjectGroupPython] N_element053  label="N_element : 025"  # scripted group (container) (typed FeaturePython)
  n = 2
  ref = N_element
FEATURE [App::DocumentObjectGroupPython] O_element115  label="O_element : 068"  # scripted group (container) (typed FeaturePython)
  n = 2
  ref = O_element
FEATURE [App::DocumentObjectGroupPython] G4_URACIL  # scripted group (container) (typed FeaturePython)
  Dunit = g/cm3
  Dvalue = 1.32
  Group = -> [H_element123,C_element133,N_element053,O_element115]
  conduct = 2
  density = 1
  expand = 3
  formula = G4_URACIL
  name = G4_URACIL
  specific = 4
FEATURE [App::DocumentObjectGroupPython] H_element124  label="H_element : 071"  # scripted group (container) (typed FeaturePython)
  n = 4
  ref = H_element
FEATURE [App::DocumentObjectGroupPython] C_element134  label="C_element : 079"  # scripted group (container) (typed FeaturePython)
  n = 5
  ref = C_element
FEATURE [App::DocumentObjectGroupPython] N_element054  label="N_element : 026"  # scripted group (container) (typed FeaturePython)
  n = 5
  ref = N_element
FEATURE [App::DocumentObjectGroupPython] G4_DNA_ADENINE  # scripted group (container) (typed FeaturePython)
  Dunit = g/cm3
  Dvalue = 1
  Group = -> [H_element124,C_element134,N_element054]
  conduct = 2
  density = 1
  expand = 3
  formula = G4_DNA_ADENINE
  name = G4_DNA_ADENINE
  specific = 4
FEATURE [App::DocumentObjectGroupPython] H_element125  label="H_element : 072"  # scripted group (container) (typed FeaturePython)
  n = 4
  ref = H_element
FEATURE [App::DocumentObjectGroupPython] C_element135  label="C_element : 080"  # scripted group (container) (typed FeaturePython)
  n = 5
  ref = C_element
FEATURE [App::DocumentObjectGroupPython] N_element055  label="N_element : 027"  # scripted group (container) (typed FeaturePython)
  n = 5
  ref = N_element
FEATURE [App::DocumentObjectGroupPython] O_element116  label="O_element : 069"  # scripted group (container) (typed FeaturePython)
  n = 1
  ref = O_element
FEATURE [App::DocumentObjectGroupPython] G4_DNA_GUANINE  # scripted group (container) (typed FeaturePython)
  Dunit = g/cm3
  Dvalue = 1
  Group = -> [H_element125,C_element135,N_element055,O_element116]
  conduct = 2
  density = 1
  expand = 3
  formula = G4_DNA_GUANINE
  name = G4_DNA_GUANINE
  specific = 4
FEATURE [App::DocumentObjectGroupPython] H_element126  label="H_element : 073"  # scripted group (container) (typed FeaturePython)
  n = 4
  ref = H_element
FEATURE [App::DocumentObjectGroupPython] C_element136  label="C_element : 081"  # scripted group (container) (typed FeaturePython)
  n = 4
  ref = C_element
FEATURE [App::DocumentObjectGroupPython] N_element056  label="N_element : 028"  # scripted group (container) (typed FeaturePython)
  n = 3
  ref = N_element
FEATURE [App::DocumentObjectGroupPython] O_element117  label="O_element : 070"  # scripted group (container) (typed FeaturePython)
  n = 1
  ref = O_element
FEATURE [App::DocumentObjectGroupPython] G4_DNA_CYTOSINE  # scripted group (container) (typed FeaturePython)
  Dunit = g/cm3
  Dvalue = 1
  Group = -> [H_element126,C_element136,N_element056,O_element117]
  conduct = 2
  density = 1
  expand = 3
  formula = G4_DNA_CYTOSINE
  name = G4_DNA_CYTOSINE
  specific = 4
FEATURE [App::DocumentObjectGroupPython] H_element127  label="H_element : 074"  # scripted group (container) (typed FeaturePython)
  n = 5
  ref = H_element
FEATURE [App::DocumentObjectGroupPython] C_element137  label="C_element : 082"  # scripted group (container) (typed FeaturePython)
  n = 5
  ref = C_element
FEATURE [App::DocumentObjectGroupPython] N_element057  label="N_element : 029"  # scripted group (container) (typed FeaturePython)
  n = 2
  ref = N_element
FEATURE [App::DocumentObjectGroupPython] O_element118  label="O_element : 071"  # scripted group (container) (typed FeaturePython)
  n = 2
  ref = O_element
FEATURE [App::DocumentObjectGroupPython] G4_DNA_THYMINE  # scripted group (container) (typed FeaturePython)
  Dunit = g/cm3
  Dvalue = 1
  Group = -> [H_element127,C_element137,N_element057,O_element118]
  conduct = 2
  density = 1
  expand = 3
  formula = G4_DNA_THYMINE
  name = G4_DNA_THYMINE
  specific = 4
FEATURE [App::DocumentObjectGroupPython] H_element128  label="H_element : 075"  # scripted group (container) (typed FeaturePython)
  n = 3
  ref = H_element
FEATURE [App::DocumentObjectGroupPython] C_element138  label="C_element : 083"  # scripted group (container) (typed FeaturePython)
  n = 4
  ref = C_element
FEATURE [App::DocumentObjectGroupPython] N_element058  label="N_element : 030"  # scripted group (container) (typed FeaturePython)
  n = 2
  ref = N_element
FEATURE [App::DocumentObjectGroupPython] O_element119  label="O_element : 072"  # scripted group (container) (typed FeaturePython)
  n = 2
  ref = O_element
FEATURE [App::DocumentObjectGroupPython] G4_DNA_URACIL  # scripted group (container) (typed FeaturePython)
  Dunit = g/cm3
  Dvalue = 1
  Group = -> [H_element128,C_element138,N_element058,O_element119]
  conduct = 2
  density = 1
  expand = 3
  formula = G4_DNA_URACIL
  name = G4_DNA_URACIL
  specific = 4
FEATURE [App::DocumentObjectGroupPython] H_element129  label="H_element : 076"  # scripted group (container) (typed FeaturePython)
  n = 10
  ref = H_element
FEATURE [App::DocumentObjectGroupPython] C_element139  label="C_element : 084"  # scripted group (container) (typed FeaturePython)
  n = 10
  ref = C_element
FEATURE [App::DocumentObjectGroupPython] N_element059  label="N_element : 031"  # scripted group (container) (typed FeaturePython)
  n = 5
  ref = N_element
FEATURE [App::DocumentObjectGroupPython] O_element120  label="O_element : 073"  # scripted group (container) (typed FeaturePython)
  n = 4
  ref = O_element
FEATURE [App::DocumentObjectGroupPython] G4_DNA_ADENOSINE  # scripted group (container) (typed FeaturePython)
  Dunit = g/cm3
  Dvalue = 1
  Group = -> [H_element129,C_element139,N_element059,O_element120]
  conduct = 2
  density = 1
  expand = 3
  formula = G4_DNA_ADENOSINE
  name = G4_DNA_ADENOSINE
  specific = 4
FEATURE [App::DocumentObjectGroupPython] H_element130  label="H_element : 077"  # scripted group (container) (typed FeaturePython)
  n = 10
  ref = H_element
FEATURE [App::DocumentObjectGroupPython] C_element140  label="C_element : 085"  # scripted group (container) (typed FeaturePython)
  n = 10
  ref = C_element
FEATURE [App::DocumentObjectGroupPython] N_element060  label="N_element : 032"  # scripted group (container) (typed FeaturePython)
  n = 5
  ref = N_element
FEATURE [App::DocumentObjectGroupPython] O_element121  label="O_element : 074"  # scripted group (container) (typed FeaturePython)
  n = 5
  ref = O_element
FEATURE [App::DocumentObjectGroupPython] G4_DNA_GUANOSINE  # scripted group (container) (typed FeaturePython)
  Dunit = g/cm3
  Dvalue = 1
  Group = -> [H_element130,C_element140,N_element060,O_element121]
  conduct = 2
  density = 1
  expand = 3
  formula = G4_DNA_GUANOSINE
  name = G4_DNA_GUANOSINE
  specific = 4
FEATURE [App::DocumentObjectGroupPython] H_element131  label="H_element : 078"  # scripted group (container) (typed FeaturePython)
  n = 10
  ref = H_element
FEATURE [App::DocumentObjectGroupPython] C_element141  label="C_element : 086"  # scripted group (container) (typed FeaturePython)
  n = 9
  ref = C_element
FEATURE [App::DocumentObjectGroupPython] N_element061  label="N_element : 033"  # scripted group (container) (typed FeaturePython)
  n = 3
  ref = N_element
FEATURE [App::DocumentObjectGroupPython] O_element122  label="O_element : 075"  # scripted group (container) (typed FeaturePython)
  n = 5
  ref = O_element
FEATURE [App::DocumentObjectGroupPython] G4_DNA_CYTIDINE  # scripted group (container) (typed FeaturePython)
  Dunit = g/cm3
  Dvalue = 1
  Group = -> [H_element131,C_element141,N_element061,O_element122]
  conduct = 2
  density = 1
  expand = 3
  formula = G4_DNA_CYTIDINE
  name = G4_DNA_CYTIDINE
  specific = 4
FEATURE [App::DocumentObjectGroupPython] H_element132  label="H_element : 079"  # scripted group (container) (typed FeaturePython)
  n = 9
  ref = H_element
FEATURE [App::DocumentObjectGroupPython] C_element142  label="C_element : 087"  # scripted group (container) (typed FeaturePython)
  n = 9
  ref = C_element
FEATURE [App::DocumentObjectGroupPython] N_element062  label="N_element : 034"  # scripted group (container) (typed FeaturePython)
  n = 2
  ref = N_element
FEATURE [App::DocumentObjectGroupPython] O_element123  label="O_element : 076"  # scripted group (container) (typed FeaturePython)
  n = 6
  ref = O_element
FEATURE [App::DocumentObjectGroupPython] G4_DNA_URIDINE  # scripted group (container) (typed FeaturePython)
  Dunit = g/cm3
  Dvalue = 1
  Group = -> [H_element132,C_element142,N_element062,O_element123]
  conduct = 2
  density = 1
  expand = 3
  formula = G4_DNA_URIDINE
  name = G4_DNA_URIDINE
  specific = 4
FEATURE [App::DocumentObjectGroupPython] H_element133  label="H_element : 080"  # scripted group (container) (typed FeaturePython)
  n = 11
  ref = H_element
FEATURE [App::DocumentObjectGroupPython] C_element143  label="C_element : 088"  # scripted group (container) (typed FeaturePython)
  n = 10
  ref = C_element
FEATURE [App::DocumentObjectGroupPython] N_element063  label="N_element : 035"  # scripted group (container) (typed FeaturePython)
  n = 2
  ref = N_element
FEATURE [App::DocumentObjectGroupPython] O_element124  label="O_element : 077"  # scripted group (container) (typed FeaturePython)
  n = 6
  ref = O_element
FEATURE [App::DocumentObjectGroupPython] G4_DNA_METHYLURIDINE  # scripted group (container) (typed FeaturePython)
  Dunit = g/cm3
  Dvalue = 1
  Group = -> [H_element133,C_element143,N_element063,O_element124]
  conduct = 2
  density = 1
  expand = 3
  formula = G4_DNA_METHYLURIDINE
  name = G4_DNA_METHYLURIDINE
  specific = 4
FEATURE [App::DocumentObjectGroupPython] P_element014  label="P_element : 003"  # scripted group (container) (typed FeaturePython)
  n = 1
  ref = P_element
FEATURE [App::DocumentObjectGroupPython] O_element125  label="O_element : 078"  # scripted group (container) (typed FeaturePython)
  n = 3
  ref = O_element
FEATURE [App::DocumentObjectGroupPython] G4_DNA_MONOPHOSPHATE  # scripted group (container) (typed FeaturePython)
  Dunit = g/cm3
  Dvalue = 1
  Group = -> [P_element014,O_element125]
  conduct = 2
  density = 1
  expand = 3
  formula = G4_DNA_MONOPHOSPHATE
  name = G4_DNA_MONOPHOSPHATE
  specific = 4
FEATURE [App::DocumentObjectGroupPython] H_element134  label="H_element : 081"  # scripted group (container) (typed FeaturePython)
  n = 10
  ref = H_element
FEATURE [App::DocumentObjectGroupPython] C_element144  label="C_element : 089"  # scripted group (container) (typed FeaturePython)
  n = 10
  ref = C_element
FEATURE [App::DocumentObjectGroupPython] N_element064  label="N_element : 036"  # scripted group (container) (typed FeaturePython)
  n = 5
  ref = N_element
FEATURE [App::DocumentObjectGroupPython] O_element126  label="O_element : 079"  # scripted group (container) (typed FeaturePython)
  n = 7
  ref = O_element
FEATURE [App::DocumentObjectGroupPython] P_element015  label="P_element : 004"  # scripted group (container) (typed FeaturePython)
  n = 1
  ref = P_element
FEATURE [App::DocumentObjectGroupPython] G4_DNA_A  # scripted group (container) (typed FeaturePython)
  Dunit = g/cm3
  Dvalue = 1
  Group = -> [H_element134,C_element144,N_element064,O_element126,P_element015]
  conduct = 2
  density = 1
  expand = 3
  formula = G4_DNA_A
  name = G4_DNA_A
  specific = 4
FEATURE [App::DocumentObjectGroupPython] H_element135  label="H_element : 082"  # scripted group (container) (typed FeaturePython)
  n = 10
  ref = H_element
FEATURE [App::DocumentObjectGroupPython] C_element145  label="C_element : 090"  # scripted group (container) (typed FeaturePython)
  n = 10
  ref = C_element
FEATURE [App::DocumentObjectGroupPython] N_element065  label="N_element : 037"  # scripted group (container) (typed FeaturePython)
  n = 5
  ref = N_element
FEATURE [App::DocumentObjectGroupPython] O_element127  label="O_element : 8"  # scripted group (container) (typed FeaturePython)
  n = 8
  ref = O_element
FEATURE [App::DocumentObjectGroupPython] P_element016  label="P_element : 005"  # scripted group (container) (typed FeaturePython)
  n = 1
  ref = P_element
FEATURE [App::DocumentObjectGroupPython] G4_DNA_G  # scripted group (container) (typed FeaturePython)
  Dunit = g/cm3
  Dvalue = 1
  Group = -> [H_element135,C_element145,N_element065,O_element127,P_element016]
  conduct = 2
  density = 1
  expand = 3
  formula = G4_DNA_G
  name = G4_DNA_G
  specific = 4
FEATURE [App::DocumentObjectGroupPython] H_element136  label="H_element : 083"  # scripted group (container) (typed FeaturePython)
  n = 10
  ref = H_element
FEATURE [App::DocumentObjectGroupPython] C_element146  label="C_element : 091"  # scripted group (container) (typed FeaturePython)
  n = 9
  ref = C_element
FEATURE [App::DocumentObjectGroupPython] N_element066  label="N_element : 038"  # scripted group (container) (typed FeaturePython)
  n = 3
  ref = N_element
FEATURE [App::DocumentObjectGroupPython] O_element128  label="O_element : 080"  # scripted group (container) (typed FeaturePython)
  n = 8
  ref = O_element
FEATURE [App::DocumentObjectGroupPython] P_element017  label="P_element : 006"  # scripted group (container) (typed FeaturePython)
  n = 1
  ref = P_element
FEATURE [App::DocumentObjectGroupPython] G4_DNA_C  # scripted group (container) (typed FeaturePython)
  Dunit = g/cm3
  Dvalue = 1
  Group = -> [H_element136,C_element146,N_element066,O_element128,P_element017]
  conduct = 2
  density = 1
  expand = 3
  formula = G4_DNA_C
  name = G4_DNA_C
  specific = 4
FEATURE [App::DocumentObjectGroupPython] H_element137  label="H_element : 084"  # scripted group (container) (typed FeaturePython)
  n = 9
  ref = H_element
FEATURE [App::DocumentObjectGroupPython] C_element147  label="C_element : 092"  # scripted group (container) (typed FeaturePython)
  n = 9
  ref = C_element
FEATURE [App::DocumentObjectGroupPython] N_element067  label="N_element : 039"  # scripted group (container) (typed FeaturePython)
  n = 2
  ref = N_element
FEATURE [App::DocumentObjectGroupPython] O_element129  label="O_element : 9"  # scripted group (container) (typed FeaturePython)
  n = 9
  ref = O_element
FEATURE [App::DocumentObjectGroupPython] P_element018  label="P_element : 007"  # scripted group (container) (typed FeaturePython)
  n = 1
  ref = P_element
FEATURE [App::DocumentObjectGroupPython] G4_DNA_U  # scripted group (container) (typed FeaturePython)
  Dunit = g/cm3
  Dvalue = 1
  Group = -> [H_element137,C_element147,N_element067,O_element129,P_element018]
  conduct = 2
  density = 1
  expand = 3
  formula = G4_DNA_U
  name = G4_DNA_U
  specific = 4
FEATURE [App::DocumentObjectGroupPython] H_element138  label="H_element : 085"  # scripted group (container) (typed FeaturePython)
  n = 11
  ref = H_element
FEATURE [App::DocumentObjectGroupPython] C_element148  label="C_element : 093"  # scripted group (container) (typed FeaturePython)
  n = 10
  ref = C_element
FEATURE [App::DocumentObjectGroupPython] N_element068  label="N_element : 040"  # scripted group (container) (typed FeaturePython)
  n = 2
  ref = N_element
FEATURE [App::DocumentObjectGroupPython] O_element130  label="O_element : 081"  # scripted group (container) (typed FeaturePython)
  n = 9
  ref = O_element
FEATURE [App::DocumentObjectGroupPython] P_element019  label="P_element : 008"  # scripted group (container) (typed FeaturePython)
  n = 1
  ref = P_element
FEATURE [App::DocumentObjectGroupPython] G4_DNA_MU  # scripted group (container) (typed FeaturePython)
  Dunit = g/cm3
  Dvalue = 1
  Group = -> [H_element138,C_element148,N_element068,O_element130,P_element019]
  conduct = 2
  density = 1
  expand = 3
  formula = G4_DNA_MU
  name = G4_DNA_MU
  specific = 4
FEATURE [App::DocumentObjectGroupPython] BioChemical  # scripted group (container) (typed FeaturePython)
  Group = -> [G4_CYTOSINE,G4_THYMINE,G4_URACIL,G4_DNA_ADENINE,G4_DNA_GUANINE,G4_DNA_CYTOSINE,G4_DNA_THYMINE,G4_DNA_URACIL,G4_DNA_ADENOSINE,G4_DNA_GUANOSINE,G4_DNA_CYTIDINE,G4_DNA_URIDINE,G4_DNA_METHYLURIDINE,G4_DNA_MONOPHOSPHATE,G4_DNA_A,G4_DNA_G,G4_DNA_C,G4_DNA_U,G4_DNA_MU]
FEATURE [App::DocumentObjectGroupPython] G4Materials  # scripted group (container) (typed FeaturePython)
  Group = -> [NIST,Element,HEP,Space,BioChemical]
  version = 1
FEATURE [App::DocumentObjectGroupPython] Geant4  # scripted group (container) (typed FeaturePython)
  Group = -> [G4Isotopes,G4Elements,G4Materials]
FEATURE [App::DocumentObjectGroupPython] Materials  # scripted group (container) (typed FeaturePython)
  Group = -> [Geant4]
FEATURE [Part::FeaturePython] GDMLBox_WorldBox  # WARN: FeaturePython — macro-defined, semantics opaque (R4)
  lunit = 2
  material = 5
  x = 100
  y = 100
  z = 100
FEATURE [Sketcher::SketchObject] Sketch
  ArcFitTolerance = 0
  FullyConstrained = false
  MakeInternals = false
  sketch-geometry (15):
    g0-g5: Circle [constr] x6 (B-spline internal-alignment scaffolding for g6; pole/knot coordinates omitted)
    g6: BSplineCurve PolesCount=7 KnotsCount=5 Degree=3 IsPeriodic=0
    g7-g10: GeomPoint [constr] x4 (B-spline internal-alignment scaffolding for g6; pole/knot coordinates omitted)
    g11: LineSegment StartX=-4.39557 StartY=8.39124 StartZ=0 EndX=-5.2662 EndY=10.5884 EndZ=0
    g12: LineSegment StartX=-5.2662 StartY=10.5884 StartZ=0 EndX=-7.82152 EndY=9.89481 EndZ=0
    g13: LineSegment StartX=-7.82152 StartY=9.89481 StartZ=0 EndX=-9.50073 EndY=7.63152 EndZ=0
    g14: ArcOfCircle CenterX=-7.8377 CenterY=5.34547 CenterZ=0 NormalX=0 NormalY=0 NormalZ=1 AngleXU=0 Radius=2.82696 StartAngle=4.84147 EndAngle=8.48291
  constraints (9):
    c: Weight(g0) = 1
    c: Equal(g0, g1-g5) x5
    c: InternalAlignment(g0-g5 -> g6) x6
    c: InternalAlignment(g7-g10 -> g6) x4
    c: Coincident(g11,g6)
    c: Coincident(g11,g12)
    c: Coincident(g12,g13)
    c: Coincident(g14,g13)
    c: Coincident(g14,g6)
FEATURE [Part::Extrusion] Extrude
  Base = -> Sketch
  Dir = (0,0,1)
  DirMode = 2
  FaceMakerClass = Part::FaceMakerBullseye
  FaceMakerMode = 3
  LengthFwd = 10
  LengthRev = 0
  Placement = pos=(13,9,0) rot=(0,0,1;0rad)
  Solid = true
  Symmetric = false
  material = 1
FEATURE [Part::Mirroring] Part__Mirroring  label="Extrude_mirror"
  Base = (0,0,0)
  Normal = (0.83205,0.5547,0)
  Source = -> Extrude
  material = 261
FEATURE [App::Part] Part
  Group = -> [Sketch,Extrude,Part__Mirroring]
  Origin = -> Origin001
FEATURE [App::Part] worldVOL
  Group = -> [GDMLBox_WorldBox,Part]
  Origin = -> Origin
